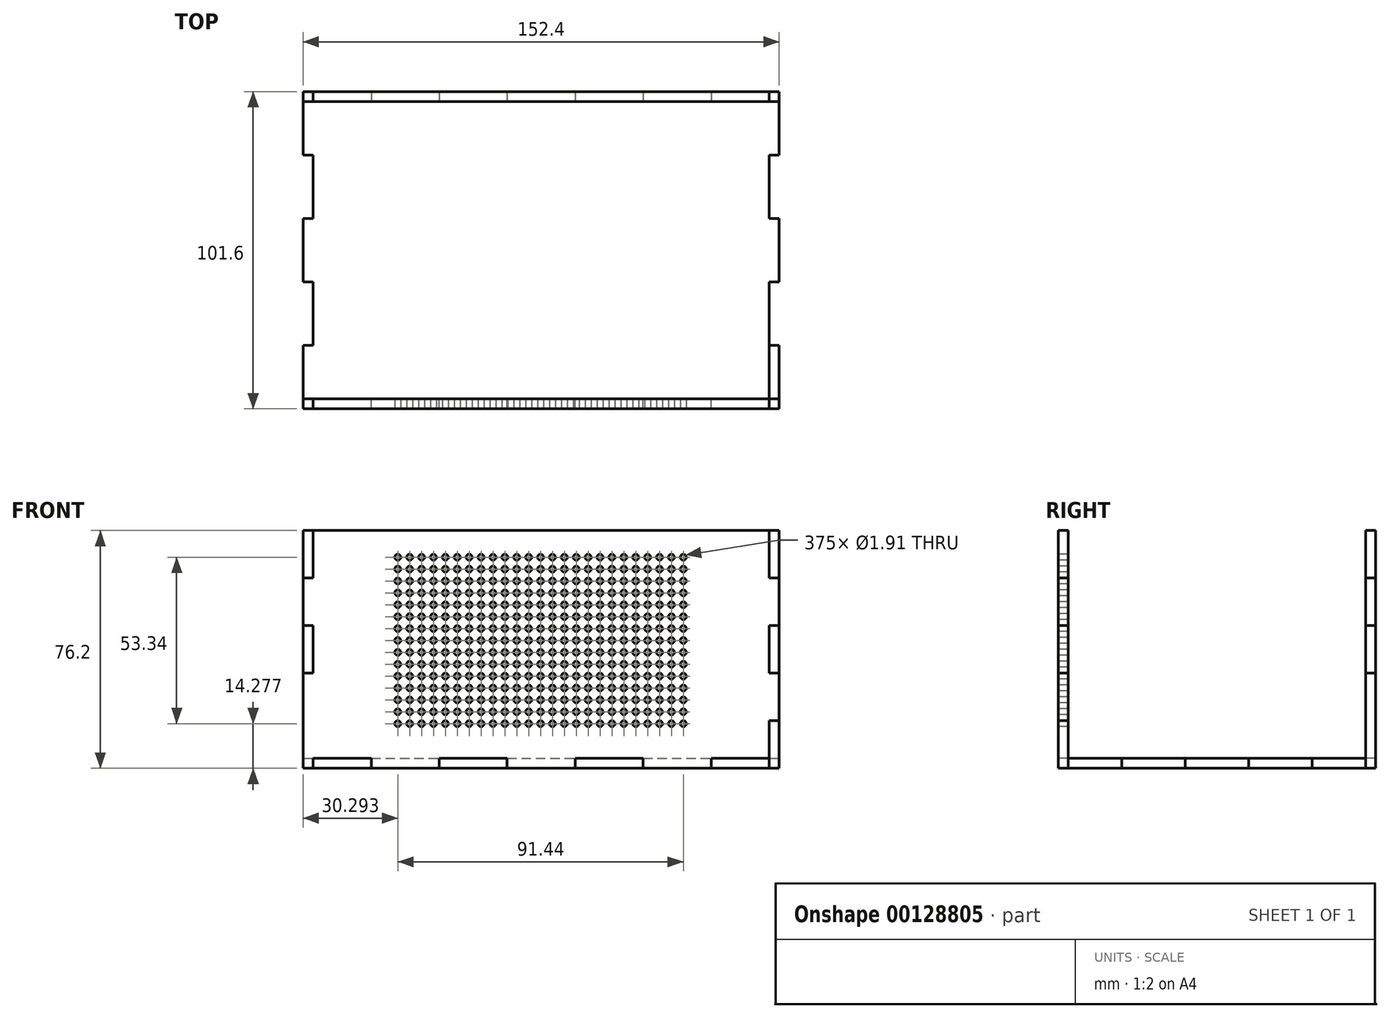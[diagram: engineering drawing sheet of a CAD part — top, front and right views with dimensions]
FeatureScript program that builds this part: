
annotation { "Feature Type Name" : "Feature", "Feature Type Description" : "" }
export const myFeature = defineFeature(function(context is Context, id is Id, definition is map)
    precondition{}
    {
        {
            var Q0;
            Q0=qCreatedBy(makeId("Top.planeOp"),FACE);
            var sketch = newSketch(context, id + "F0", { "sketchPlane" : qUnion([Q0])});
            skLineSegment(sketch, "E0.bottom", {"start": v(76.2, 50.8) * mm, "end": v(-76.2, 50.8) * mm});
            skLineSegment(sketch, "E0.top", {"start": v(76.2, -50.8) * mm, "end": v(-76.2, -50.8) * mm});
            skLineSegment(sketch, "E0.left", {"start": v(76.2, 50.8) * mm, "end": v(76.2, -50.8) * mm});
            skLineSegment(sketch, "E0.right", {"start": v(-76.2, 50.8) * mm, "end": v(-76.2, -50.8) * mm});
            skPoint(sketch, "E0.middle", {"position": v(0, 0) * mm});
            skLineSegment(sketch, "E1", {"start": v(-76.2, 50.8) * mm, "end": v(-76.2, 47.62) * mm});
            skLineSegment(sketch, "E2.1.0.0", {"start": v(-54.43, 50.8) * mm, "end": v(-54.43, 47.62) * mm});
            skLineSegment(sketch, "E2.2.0.0", {"start": v(-32.66, 50.8) * mm, "end": v(-32.66, 47.63) * mm});
            skLineSegment(sketch, "E2.3.0.0", {"start": v(-10.89, 50.8) * mm, "end": v(-10.89, 47.63) * mm});
            skLineSegment(sketch, "E2.4.0.0", {"start": v(10.89, 50.8) * mm, "end": v(10.89, 47.63) * mm});
            skLineSegment(sketch, "E2.5.0.0", {"start": v(32.66, 50.8) * mm, "end": v(32.66, 47.63) * mm});
            skLineSegment(sketch, "E2.6.0.0", {"start": v(54.43, 50.8) * mm, "end": v(54.43, 47.63) * mm});
            skLineSegment(sketch, "E2.7.0.0", {"start": v(76.2, 50.8) * mm, "end": v(76.2, 47.63) * mm});
            skLineSegment(sketch, "E2.direction1", {"start": v(-76.2, 47.63) * mm, "end": v(-54.43, 47.63) * mm, "construction": true});
            skLineSegment(sketch, "E3", {"start": v(-76.2, 47.63) * mm, "end": v(76.2, 47.63) * mm});
            skLineSegment(sketch, "E4.MirrorCS", {"start": v(-76.2, -50.8) * mm, "end": v(-76.2, -47.62) * mm});
            skLineSegment(sketch, "E5.MirrorCS", {"start": v(76.2, -50.8) * mm, "end": v(76.2, -47.63) * mm});
            skLineSegment(sketch, "E6.MirrorCS", {"start": v(54.43, -50.8) * mm, "end": v(54.43, -47.63) * mm});
            skLineSegment(sketch, "E7.MirrorCS", {"start": v(32.66, -50.8) * mm, "end": v(32.66, -47.63) * mm});
            skLineSegment(sketch, "E8.MirrorCS", {"start": v(10.89, -50.8) * mm, "end": v(10.89, -47.63) * mm});
            skLineSegment(sketch, "E9.MirrorCS", {"start": v(-54.43, -50.8) * mm, "end": v(-54.43, -47.62) * mm});
            skLineSegment(sketch, "E10.MirrorCS", {"start": v(-10.89, -50.8) * mm, "end": v(-10.89, -47.63) * mm});
            skLineSegment(sketch, "E11.MirrorCS", {"start": v(-32.66, -50.8) * mm, "end": v(-32.66, -47.63) * mm});
            skLineSegment(sketch, "E12.MirrorCS", {"start": v(-76.2, -47.63) * mm, "end": v(76.2, -47.63) * mm});
            skLineSegment(sketch, "E13.MirrorCS", {"start": v(-76.2, -47.63) * mm, "end": v(-54.43, -47.63) * mm, "construction": true});
            skLineSegment(sketch, "E14", {"start": v(-76.2, 50.8) * mm, "end": v(-73.03, 50.8) * mm});
            skLineSegment(sketch, "E15.0.1.0", {"start": v(-76.2, 30.48) * mm, "end": v(-73.03, 30.48) * mm});
            skLineSegment(sketch, "E15.0.2.0", {"start": v(-76.2, 10.16) * mm, "end": v(-73.03, 10.16) * mm});
            skLineSegment(sketch, "E15.0.3.0", {"start": v(-76.2, -10.16) * mm, "end": v(-73.03, -10.16) * mm});
            skLineSegment(sketch, "E15.0.4.0", {"start": v(-76.2, -30.48) * mm, "end": v(-73.03, -30.48) * mm});
            skLineSegment(sketch, "E15.0.5.0", {"start": v(-76.2, -50.8) * mm, "end": v(-73.03, -50.8) * mm});
            skLineSegment(sketch, "E15.direction1", {"start": v(-76.2, 50.8) * mm, "end": v(-59.4, 50.8) * mm, "construction": true});
            skLineSegment(sketch, "E15.direction2", {"start": v(-76.2, 50.8) * mm, "end": v(-76.2, 30.48) * mm, "construction": true});
            skLineSegment(sketch, "E16", {"start": v(-73.03, 50.8) * mm, "end": v(-73.03, -50.8) * mm});
            skLineSegment(sketch, "E17.MirrorCS", {"start": v(76.2, -50.8) * mm, "end": v(76.2, -47.62) * mm});
            skLineSegment(sketch, "E18.MirrorCS", {"start": v(76.2, 50.8) * mm, "end": v(76.2, 47.62) * mm});
            skLineSegment(sketch, "E19.MirrorCS", {"start": v(76.2, 50.8) * mm, "end": v(73.03, 50.8) * mm});
            skLineSegment(sketch, "E20.MirrorCS", {"start": v(76.2, -50.8) * mm, "end": v(73.03, -50.8) * mm});
            skLineSegment(sketch, "E21.MirrorCS", {"start": v(76.2, -10.16) * mm, "end": v(73.03, -10.16) * mm});
            skLineSegment(sketch, "E22.MirrorCS", {"start": v(76.2, 30.48) * mm, "end": v(73.03, 30.48) * mm});
            skLineSegment(sketch, "E23.MirrorCS", {"start": v(76.2, -30.48) * mm, "end": v(73.03, -30.48) * mm});
            skLineSegment(sketch, "E24.MirrorCS", {"start": v(76.2, 10.16) * mm, "end": v(73.03, 10.16) * mm});
            skLineSegment(sketch, "E25.MirrorCS", {"start": v(73.03, 50.8) * mm, "end": v(73.03, -50.8) * mm});
            skLineSegment(sketch, "E26.MirrorCS", {"start": v(76.2, 50.8) * mm, "end": v(76.2, 30.48) * mm, "construction": true});
            skSolve(sketch);
        }
        {
            var Q0;
            {var subQ3=sQuery(id+"F0.wireOp",EDGE,"E3");var subQ22=makeQuery(id+"F0.imprint","INTERSECT",VERTEX,{"derivedFrom":[sQuery(id+"F0.wireOp",EDGE,"E2.1.0.0"),subQ3]});Q0=makeQuery(id+"F0.imprint","IMPRINT",FACE,{"disambiguationData":[TD([[makeQuery(id+"F0.imprint","IMPRINT",EDGE,{"disambiguationData":[TD([[subQ22,1.0]])],"derivedFrom":subQ3}),-1.0]])]});}
            var Q1;
            {var subQ3=sQuery(id+"F0.wireOp",EDGE,"E2.1.0.0");Q1=makeQuery(id+"F0.imprint","IMPRINT",FACE,{"disambiguationData":[TD([[makeQuery(id+"F0.imprint","IMPRINT",EDGE,{"derivedFrom":subQ3}),-1.0]])]});}
            var Q2;
            {var subQ0=sQuery(id+"F0.wireOp",EDGE,"E1");Q2=makeQuery(id+"F0.imprint","IMPRINT",FACE,{"disambiguationData":[TD([[makeQuery(id+"F0.imprint","IMPRINT",EDGE,{"derivedFrom":subQ0}),1.0]])]});}
            var Q3;
            {var subQ3=sQuery(id+"F0.wireOp",EDGE,"E15.0.1.0");Q3=makeQuery(id+"F0.imprint","IMPRINT",FACE,{"disambiguationData":[TD([[makeQuery(id+"F0.imprint","IMPRINT",EDGE,{"derivedFrom":subQ3}),1.0]])]});}
            var Q4;
            {var subQ0=sQuery(id+"F0.wireOp",EDGE,"E15.0.2.0");Q4=makeQuery(id+"F0.imprint","IMPRINT",FACE,{"disambiguationData":[TD([[makeQuery(id+"F0.imprint","IMPRINT",EDGE,{"derivedFrom":subQ0}),-1.0]])]});}
            var Q5;
            {var subQ3=sQuery(id+"F0.wireOp",EDGE,"E15.0.4.0");Q5=makeQuery(id+"F0.imprint","IMPRINT",FACE,{"disambiguationData":[TD([[makeQuery(id+"F0.imprint","IMPRINT",EDGE,{"derivedFrom":subQ3}),-1.0]])]});}
            var Q6;
            {var subQ0=sQuery(id+"F0.wireOp",EDGE,"E4.MirrorCS");Q6=makeQuery(id+"F0.imprint","IMPRINT",FACE,{"disambiguationData":[TD([[makeQuery(id+"F0.imprint","IMPRINT",EDGE,{"derivedFrom":subQ0}),-1.0]])]});}
            var Q7;
            {var subQ0=sQuery(id+"F0.wireOp",EDGE,"E9.MirrorCS");Q7=makeQuery(id+"F0.imprint","IMPRINT",FACE,{"disambiguationData":[TD([[makeQuery(id+"F0.imprint","IMPRINT",EDGE,{"derivedFrom":subQ0}),1.0]])]});}
            var Q8;
            {var subQ0=sQuery(id+"F0.wireOp",EDGE,"E10.MirrorCS");Q8=makeQuery(id+"F0.imprint","IMPRINT",FACE,{"disambiguationData":[TD([[makeQuery(id+"F0.imprint","IMPRINT",EDGE,{"derivedFrom":subQ0}),1.0]])]});}
            var Q9;
            {var subQ0=sQuery(id+"F0.wireOp",EDGE,"E7.MirrorCS");Q9=makeQuery(id+"F0.imprint","IMPRINT",FACE,{"disambiguationData":[TD([[makeQuery(id+"F0.imprint","IMPRINT",EDGE,{"derivedFrom":subQ0}),1.0]])]});}
            var Q10;
            {var subQ0=sQuery(id+"F0.wireOp",EDGE,"E6.MirrorCS");Q10=makeQuery(id+"F0.imprint","IMPRINT",FACE,{"disambiguationData":[TD([[makeQuery(id+"F0.imprint","IMPRINT",EDGE,{"derivedFrom":subQ0}),-1.0]])]});}
            var Q11;
            {var subQ5=sQuery(id+"F0.wireOp",EDGE,"E20.MirrorCS");Q11=makeQuery(id+"F0.imprint","IMPRINT",FACE,{"disambiguationData":[TD([[makeQuery(id+"F0.imprint","IMPRINT",EDGE,{"derivedFrom":subQ5}),-1.0]])]});}
            var Q12;
            {var subQ5=sQuery(id+"F0.wireOp",EDGE,"E23.MirrorCS");Q12=makeQuery(id+"F0.imprint","IMPRINT",FACE,{"disambiguationData":[TD([[makeQuery(id+"F0.imprint","IMPRINT",EDGE,{"derivedFrom":subQ5}),1.0]])]});}
            var Q13;
            {var subQ0=sQuery(id+"F0.wireOp",EDGE,"E21.MirrorCS");Q13=makeQuery(id+"F0.imprint","IMPRINT",FACE,{"disambiguationData":[TD([[makeQuery(id+"F0.imprint","IMPRINT",EDGE,{"derivedFrom":subQ0}),-1.0]])]});}
            var Q14;
            {var subQ5=sQuery(id+"F0.wireOp",EDGE,"E22.MirrorCS");Q14=makeQuery(id+"F0.imprint","IMPRINT",FACE,{"disambiguationData":[TD([[makeQuery(id+"F0.imprint","IMPRINT",EDGE,{"derivedFrom":subQ5}),-1.0]])]});}
            var Q15;
            {var subQ5=sQuery(id+"F0.wireOp",EDGE,"E19.MirrorCS");Q15=makeQuery(id+"F0.imprint","IMPRINT",FACE,{"disambiguationData":[TD([[makeQuery(id+"F0.imprint","IMPRINT",EDGE,{"derivedFrom":subQ5}),1.0]])]});}
            var Q16;
            {var subQ3=sQuery(id+"F0.wireOp",EDGE,"E2.6.0.0");Q16=makeQuery(id+"F0.imprint","IMPRINT",FACE,{"disambiguationData":[TD([[makeQuery(id+"F0.imprint","IMPRINT",EDGE,{"derivedFrom":subQ3}),1.0]])]});}
            var Q17;
            {var subQ0=sQuery(id+"F0.wireOp",EDGE,"E2.4.0.0");Q17=makeQuery(id+"F0.imprint","IMPRINT",FACE,{"disambiguationData":[TD([[makeQuery(id+"F0.imprint","IMPRINT",EDGE,{"derivedFrom":subQ0}),1.0]])]});}
            var Q18;
            {var subQ0=sQuery(id+"F0.wireOp",EDGE,"E2.2.0.0");Q18=makeQuery(id+"F0.imprint","IMPRINT",FACE,{"disambiguationData":[TD([[makeQuery(id+"F0.imprint","IMPRINT",EDGE,{"derivedFrom":subQ0}),1.0]])]});}
            extrude(context, id + "F1", {"entities" : qUnion([Q0, Q1, Q2, Q3, Q4, Q5, Q6, Q7, Q8, Q9, Q10, Q11, Q12, Q13, Q14, Q15, Q16, Q17, Q18]), "depth" : 3.17 * mm});
        }
        {
            var Q0;
            {var subQ0=sQuery(id+"F0.wireOp",EDGE,"E0.left");var subQ1=makeQuery(id+"F0.imprint","INTERSECT",VERTEX,{"derivedFrom":[sQuery(id+"F0.wireOp",EDGE,"E12.MirrorCS"),subQ0]});Q0=makeQuery(id+"F1.opExtrude","SWEPT_FACE",FACE,{"disambiguationData":[OSD([subQ0]),TDD([makeQuery(id+"F0.imprint","IMPRINT",EDGE,{"disambiguationData":[TD([[subQ1,1.0]])],"derivedFrom":subQ0}),makeQuery(id+"F0.imprint","IMPRINT",EDGE,{"disambiguationData":[TD([[subQ1,-1.0]])],"derivedFrom":subQ0})])]});}
            var sketch = newSketch(context, id + "F2", { "sketchPlane" : qUnion([Q0])});
            skLineSegment(sketch, "E27.bottom", {"start": v(-50.8, 0) * mm, "end": v(50.8, 0) * mm});
            skLineSegment(sketch, "E27.top", {"start": v(-50.8, 76.2) * mm, "end": v(50.8, 76.2) * mm});
            skLineSegment(sketch, "E27.left", {"start": v(-50.8, 0) * mm, "end": v(-50.8, 76.2) * mm});
            skLineSegment(sketch, "E27.right", {"start": v(50.8, 0) * mm, "end": v(50.8, 76.2) * mm});
            skLineSegment(sketch, "E28", {"start": v(-50.8, 76.2) * mm, "end": v(-47.63, 76.2) * mm});
            skLineSegment(sketch, "E29.0.1.0", {"start": v(-50.8, 60.96) * mm, "end": v(-47.63, 60.96) * mm});
            skLineSegment(sketch, "E29.0.2.0", {"start": v(-50.8, 45.72) * mm, "end": v(-47.63, 45.72) * mm});
            skLineSegment(sketch, "E29.0.3.0", {"start": v(-50.8, 30.48) * mm, "end": v(-47.63, 30.48) * mm});
            skLineSegment(sketch, "E29.0.4.0", {"start": v(-50.8, 15.24) * mm, "end": v(-47.63, 15.24) * mm});
            skLineSegment(sketch, "E29.0.5.0", {"start": v(-50.8, 0) * mm, "end": v(-47.63, 0) * mm});
            skLineSegment(sketch, "E29.direction1", {"start": v(-50.8, 76.2) * mm, "end": v(-25.4, 76.2) * mm, "construction": true});
            skLineSegment(sketch, "E29.direction2", {"start": v(-50.8, 76.2) * mm, "end": v(-50.8, 60.96) * mm, "construction": true});
            skLineSegment(sketch, "E30", {"start": v(-47.63, 76.2) * mm, "end": v(-47.63, 0) * mm});
            skLineSegment(sketch, "E31.MirrorCS", {"start": v(50.8, 76.2) * mm, "end": v(47.63, 76.2) * mm});
            skLineSegment(sketch, "E32.MirrorCS", {"start": v(50.8, 0) * mm, "end": v(47.63, 0) * mm});
            skLineSegment(sketch, "E33.MirrorCS", {"start": v(50.8, 45.72) * mm, "end": v(47.63, 45.72) * mm});
            skLineSegment(sketch, "E34.MirrorCS", {"start": v(50.8, 60.96) * mm, "end": v(47.63, 60.96) * mm});
            skLineSegment(sketch, "E35.MirrorCS", {"start": v(50.8, 30.48) * mm, "end": v(47.63, 30.48) * mm});
            skLineSegment(sketch, "E36.MirrorCS", {"start": v(50.8, 15.24) * mm, "end": v(47.63, 15.24) * mm});
            skLineSegment(sketch, "E37.MirrorCS", {"start": v(50.8, 76.2) * mm, "end": v(50.8, 60.96) * mm, "construction": true});
            skLineSegment(sketch, "E38.MirrorCS", {"start": v(47.63, 76.2) * mm, "end": v(47.63, 0) * mm});
            skSolve(sketch);
        }
        {
            var Q0;
            {var subQ3=sQuery(id+"F2.wireOp",EDGE,"E27.top");Q0=makeQuery(id+"F2.imprint","IMPRINT",FACE,{"disambiguationData":[TD([[makeQuery(id+"F2.imprint","IMPRINT",EDGE,{"derivedFrom":subQ3}),-1.0]])]});}
            var Q1;
            {var subQ0=sQuery(id+"F2.wireOp",EDGE,"E28");Q1=makeQuery(id+"F2.imprint","IMPRINT",FACE,{"disambiguationData":[TD([[makeQuery(id+"F2.imprint","IMPRINT",EDGE,{"derivedFrom":subQ0}),-1.0]])]});}
            var Q2;
            {var subQ0=sQuery(id+"F2.wireOp",EDGE,"E29.0.2.0");Q2=makeQuery(id+"F2.imprint","IMPRINT",FACE,{"disambiguationData":[TD([[makeQuery(id+"F2.imprint","IMPRINT",EDGE,{"derivedFrom":subQ0}),-1.0]])]});}
            var Q3;
            {var subQ5=sQuery(id+"F2.wireOp",EDGE,"E29.0.4.0");Q3=makeQuery(id+"F2.imprint","IMPRINT",FACE,{"disambiguationData":[TD([[makeQuery(id+"F2.imprint","IMPRINT",EDGE,{"derivedFrom":subQ5}),-1.0]])]});}
            var Q4;
            {var subQ0=sQuery(id+"F2.wireOp",EDGE,"E32.MirrorCS");Q4=makeQuery(id+"F2.imprint","IMPRINT",FACE,{"disambiguationData":[TD([[makeQuery(id+"F2.imprint","IMPRINT",EDGE,{"derivedFrom":subQ0}),-1.0]])]});}
            var Q5;
            {var subQ0=sQuery(id+"F2.wireOp",EDGE,"E33.MirrorCS");Q5=makeQuery(id+"F2.imprint","IMPRINT",FACE,{"disambiguationData":[TD([[makeQuery(id+"F2.imprint","IMPRINT",EDGE,{"derivedFrom":subQ0}),1.0]])]});}
            var Q6;
            {var subQ0=sQuery(id+"F2.wireOp",EDGE,"E31.MirrorCS");Q6=makeQuery(id+"F2.imprint","IMPRINT",FACE,{"disambiguationData":[TD([[makeQuery(id+"F2.imprint","IMPRINT",EDGE,{"derivedFrom":subQ0}),1.0]])]});}
            var Q7;
            {var subQ1=sQuery(id+"F0.wireOp",EDGE,"E0.left");var subQ2=sQuery(id+"F0.wireOp",EDGE,"E23.MirrorCS");var subQ3=makeQuery(id+"F1.opExtrude","SWEPT_EDGE",EDGE,{"disambiguationData":[OSD([subQ2,subQ1])]});Q7=makeQuery(id+"F2.imprint","IMPRINT",FACE,{"disambiguationData":[TD([[makeQuery(id+"F2.imprint","IMPRINT",EDGE,{"derivedFrom":subQ3}),-1.0]])]});}
            var Q8;
            {var subQ0=sQuery(id+"F2.wireOp",EDGE,"E29.0.5.0");Q8=makeQuery(id+"F2.imprint","IMPRINT",FACE,{"disambiguationData":[TD([[makeQuery(id+"F2.imprint","IMPRINT",EDGE,{"derivedFrom":subQ0}),-1.0]])]});}
            extrude(context, id + "F3", {"entities" : qUnion([Q0, Q1, Q2, Q3, Q4, Q5, Q6, Q7, Q8]), "oppositeDirection" : true, "depth" : 3.17 * mm});
        }
        {
            var Q0;
            Q0=makeQuery(id+"F1.opExtrude","SWEPT_BODY",BODY,{"disambiguationData":[OSD([sQuery(id+"F0.wireOp",EDGE,"E0.bottom"),sQuery(id+"F0.wireOp",EDGE,"E0.right"),sQuery(id+"F0.wireOp",EDGE,"E1"),sQuery(id+"F0.wireOp",EDGE,"E2.1.0.0"),sQuery(id+"F0.wireOp",EDGE,"E2.2.0.0"),sQuery(id+"F0.wireOp",EDGE,"E2.3.0.0"),sQuery(id+"F0.wireOp",EDGE,"E2.4.0.0"),sQuery(id+"F0.wireOp",EDGE,"E2.5.0.0"),sQuery(id+"F0.wireOp",EDGE,"E2.6.0.0"),sQuery(id+"F0.wireOp",EDGE,"E3"),sQuery(id+"F0.wireOp",EDGE,"E4.MirrorCS"),sQuery(id+"F0.wireOp",EDGE,"E6.MirrorCS"),sQuery(id+"F0.wireOp",EDGE,"E7.MirrorCS"),sQuery(id+"F0.wireOp",EDGE,"E8.MirrorCS"),sQuery(id+"F0.wireOp",EDGE,"E9.MirrorCS"),sQuery(id+"F0.wireOp",EDGE,"E10.MirrorCS"),sQuery(id+"F0.wireOp",EDGE,"E11.MirrorCS"),sQuery(id+"F0.wireOp",EDGE,"E12.MirrorCS"),sQuery(id+"F0.wireOp",EDGE,"E0.top"),sQuery(id+"F0.wireOp",EDGE,"E14"),sQuery(id+"F0.wireOp",EDGE,"E15.0.1.0"),sQuery(id+"F0.wireOp",EDGE,"E15.0.2.0"),sQuery(id+"F0.wireOp",EDGE,"E15.0.3.0"),sQuery(id+"F0.wireOp",EDGE,"E15.0.4.0"),sQuery(id+"F0.wireOp",EDGE,"E15.0.5.0"),sQuery(id+"F0.wireOp",EDGE,"E16"),sQuery(id+"F0.wireOp",EDGE,"E19.MirrorCS"),sQuery(id+"F0.wireOp",EDGE,"E20.MirrorCS"),sQuery(id+"F0.wireOp",EDGE,"E21.MirrorCS"),sQuery(id+"F0.wireOp",EDGE,"E22.MirrorCS"),sQuery(id+"F0.wireOp",EDGE,"E23.MirrorCS"),sQuery(id+"F0.wireOp",EDGE,"E24.MirrorCS"),sQuery(id+"F0.wireOp",EDGE,"E25.MirrorCS"),sQuery(id+"F0.wireOp",EDGE,"E0.left")])]});
            var Q1;
            Q1=makeQuery(id+"F3.opExtrude","SWEPT_BODY",BODY,{"disambiguationData":[OSD([sQuery(id+"F2.wireOp",EDGE,"E27.bottom"),sQuery(id+"F2.wireOp",EDGE,"E27.top"),sQuery(id+"F2.wireOp",EDGE,"E27.left"),sQuery(id+"F2.wireOp",EDGE,"E28"),sQuery(id+"F2.wireOp",EDGE,"E29.0.1.0"),sQuery(id+"F2.wireOp",EDGE,"E29.0.2.0"),sQuery(id+"F2.wireOp",EDGE,"E29.0.3.0"),sQuery(id+"F2.wireOp",EDGE,"E29.0.4.0"),sQuery(id+"F2.wireOp",EDGE,"E29.0.5.0"),sQuery(id+"F2.wireOp",EDGE,"E30"),sQuery(id+"F2.wireOp",EDGE,"E31.MirrorCS"),sQuery(id+"F2.wireOp",EDGE,"E32.MirrorCS"),sQuery(id+"F2.wireOp",EDGE,"E33.MirrorCS"),sQuery(id+"F2.wireOp",EDGE,"E34.MirrorCS"),sQuery(id+"F2.wireOp",EDGE,"E35.MirrorCS"),sQuery(id+"F2.wireOp",EDGE,"E36.MirrorCS"),sQuery(id+"F2.wireOp",EDGE,"E38.MirrorCS"),sQuery(id+"F2.wireOp",EDGE,"E27.right")])]});
            booleanBodies(context, id + "F4", {"operationType" : BooleanOperationType.SUBTRACTION, "tools" : qUnion([Q0]), "targets" : qUnion([Q1]), "keepTools" : true});
        }
        {
            var Q0;
            Q0=makeQuery(id+"F3.opExtrude","SWEPT_BODY",BODY,{"disambiguationData":[OSD([sQuery(id+"F2.wireOp",EDGE,"E27.bottom"),sQuery(id+"F2.wireOp",EDGE,"E27.top"),sQuery(id+"F2.wireOp",EDGE,"E27.left"),sQuery(id+"F2.wireOp",EDGE,"E28"),sQuery(id+"F2.wireOp",EDGE,"E29.0.1.0"),sQuery(id+"F2.wireOp",EDGE,"E29.0.2.0"),sQuery(id+"F2.wireOp",EDGE,"E29.0.3.0"),sQuery(id+"F2.wireOp",EDGE,"E29.0.4.0"),sQuery(id+"F2.wireOp",EDGE,"E29.0.5.0"),sQuery(id+"F2.wireOp",EDGE,"E30"),sQuery(id+"F2.wireOp",EDGE,"E31.MirrorCS"),sQuery(id+"F2.wireOp",EDGE,"E32.MirrorCS"),sQuery(id+"F2.wireOp",EDGE,"E33.MirrorCS"),sQuery(id+"F2.wireOp",EDGE,"E34.MirrorCS"),sQuery(id+"F2.wireOp",EDGE,"E35.MirrorCS"),sQuery(id+"F2.wireOp",EDGE,"E36.MirrorCS"),sQuery(id+"F2.wireOp",EDGE,"E38.MirrorCS"),sQuery(id+"F2.wireOp",EDGE,"E27.right")])]});
            var Q1;
            Q1=qCreatedBy(makeId("Right.planeOp"),FACE);
            mirror(context, id + "F5", {"entities" : qUnion([Q0]), "mirrorPlane" : qUnion([Q1])});
        }
        {
            var Q0;
            Q0=makeQuery(id+"F1.opExtrude","SWEPT_FACE",FACE,{"disambiguationData":[OSD([sQuery(id+"F0.wireOp",EDGE,"E0.bottom"),sQuery(id+"F0.wireOp",EDGE,"E19.MirrorCS")])]});
            var sketch = newSketch(context, id + "F6", { "sketchPlane" : qUnion([Q0])});
            skLineSegment(sketch, "E39.bottom", {"start": v(-76.2, 0) * mm, "end": v(76.2, 0) * mm});
            skLineSegment(sketch, "E39.top", {"start": v(-76.2, 76.2) * mm, "end": v(76.2, 76.2) * mm});
            skLineSegment(sketch, "E39.left", {"start": v(-76.2, 0) * mm, "end": v(-76.2, 76.2) * mm});
            skLineSegment(sketch, "E39.right", {"start": v(76.2, 0) * mm, "end": v(76.2, 76.2) * mm});
            skSolve(sketch);
        }
        {
            var Q0;
            {var subQ4=sQuery(id+"F6.wireOp",EDGE,"E39.top");Q0=makeQuery(id+"F6.imprint","IMPRINT",FACE,{"disambiguationData":[TD([[makeQuery(id+"F6.imprint","IMPRINT",EDGE,{"derivedFrom":subQ4}),-1.0]])]});}
            extrude(context, id + "F7", {"entities" : qUnion([Q0]), "oppositeDirection" : true, "depth" : 3.17 * mm});
        }
        {
            var Q0;
            Q0=makeQuery(id+"F5.opPattern","COPY",BODY,{"derivedFrom":makeQuery(id+"F3.opExtrude","SWEPT_BODY",BODY,{"disambiguationData":[OSD([sQuery(id+"F2.wireOp",EDGE,"E27.bottom"),sQuery(id+"F2.wireOp",EDGE,"E27.top"),sQuery(id+"F2.wireOp",EDGE,"E27.left"),sQuery(id+"F2.wireOp",EDGE,"E28"),sQuery(id+"F2.wireOp",EDGE,"E29.0.1.0"),sQuery(id+"F2.wireOp",EDGE,"E29.0.2.0"),sQuery(id+"F2.wireOp",EDGE,"E29.0.3.0"),sQuery(id+"F2.wireOp",EDGE,"E29.0.4.0"),sQuery(id+"F2.wireOp",EDGE,"E29.0.5.0"),sQuery(id+"F2.wireOp",EDGE,"E30"),sQuery(id+"F2.wireOp",EDGE,"E31.MirrorCS"),sQuery(id+"F2.wireOp",EDGE,"E32.MirrorCS"),sQuery(id+"F2.wireOp",EDGE,"E33.MirrorCS"),sQuery(id+"F2.wireOp",EDGE,"E34.MirrorCS"),sQuery(id+"F2.wireOp",EDGE,"E35.MirrorCS"),sQuery(id+"F2.wireOp",EDGE,"E36.MirrorCS"),sQuery(id+"F2.wireOp",EDGE,"E38.MirrorCS"),sQuery(id+"F2.wireOp",EDGE,"E27.right")])]}),"instanceName":"1"});
            var Q1;
            Q1=makeQuery(id+"F1.opExtrude","SWEPT_BODY",BODY,{"disambiguationData":[OSD([sQuery(id+"F0.wireOp",EDGE,"E0.bottom"),sQuery(id+"F0.wireOp",EDGE,"E0.right"),sQuery(id+"F0.wireOp",EDGE,"E1"),sQuery(id+"F0.wireOp",EDGE,"E2.1.0.0"),sQuery(id+"F0.wireOp",EDGE,"E2.2.0.0"),sQuery(id+"F0.wireOp",EDGE,"E2.3.0.0"),sQuery(id+"F0.wireOp",EDGE,"E2.4.0.0"),sQuery(id+"F0.wireOp",EDGE,"E2.5.0.0"),sQuery(id+"F0.wireOp",EDGE,"E2.6.0.0"),sQuery(id+"F0.wireOp",EDGE,"E3"),sQuery(id+"F0.wireOp",EDGE,"E4.MirrorCS"),sQuery(id+"F0.wireOp",EDGE,"E6.MirrorCS"),sQuery(id+"F0.wireOp",EDGE,"E7.MirrorCS"),sQuery(id+"F0.wireOp",EDGE,"E8.MirrorCS"),sQuery(id+"F0.wireOp",EDGE,"E9.MirrorCS"),sQuery(id+"F0.wireOp",EDGE,"E10.MirrorCS"),sQuery(id+"F0.wireOp",EDGE,"E11.MirrorCS"),sQuery(id+"F0.wireOp",EDGE,"E12.MirrorCS"),sQuery(id+"F0.wireOp",EDGE,"E0.top"),sQuery(id+"F0.wireOp",EDGE,"E14"),sQuery(id+"F0.wireOp",EDGE,"E15.0.1.0"),sQuery(id+"F0.wireOp",EDGE,"E15.0.2.0"),sQuery(id+"F0.wireOp",EDGE,"E15.0.3.0"),sQuery(id+"F0.wireOp",EDGE,"E15.0.4.0"),sQuery(id+"F0.wireOp",EDGE,"E15.0.5.0"),sQuery(id+"F0.wireOp",EDGE,"E16"),sQuery(id+"F0.wireOp",EDGE,"E19.MirrorCS"),sQuery(id+"F0.wireOp",EDGE,"E20.MirrorCS"),sQuery(id+"F0.wireOp",EDGE,"E21.MirrorCS"),sQuery(id+"F0.wireOp",EDGE,"E22.MirrorCS"),sQuery(id+"F0.wireOp",EDGE,"E23.MirrorCS"),sQuery(id+"F0.wireOp",EDGE,"E24.MirrorCS"),sQuery(id+"F0.wireOp",EDGE,"E25.MirrorCS"),sQuery(id+"F0.wireOp",EDGE,"E0.left")])]});
            var Q2;
            Q2=makeQuery(id+"F3.opExtrude","SWEPT_BODY",BODY,{"disambiguationData":[OSD([sQuery(id+"F2.wireOp",EDGE,"E27.bottom"),sQuery(id+"F2.wireOp",EDGE,"E27.top"),sQuery(id+"F2.wireOp",EDGE,"E27.left"),sQuery(id+"F2.wireOp",EDGE,"E28"),sQuery(id+"F2.wireOp",EDGE,"E29.0.1.0"),sQuery(id+"F2.wireOp",EDGE,"E29.0.2.0"),sQuery(id+"F2.wireOp",EDGE,"E29.0.3.0"),sQuery(id+"F2.wireOp",EDGE,"E29.0.4.0"),sQuery(id+"F2.wireOp",EDGE,"E29.0.5.0"),sQuery(id+"F2.wireOp",EDGE,"E30"),sQuery(id+"F2.wireOp",EDGE,"E31.MirrorCS"),sQuery(id+"F2.wireOp",EDGE,"E32.MirrorCS"),sQuery(id+"F2.wireOp",EDGE,"E33.MirrorCS"),sQuery(id+"F2.wireOp",EDGE,"E34.MirrorCS"),sQuery(id+"F2.wireOp",EDGE,"E35.MirrorCS"),sQuery(id+"F2.wireOp",EDGE,"E36.MirrorCS"),sQuery(id+"F2.wireOp",EDGE,"E38.MirrorCS"),sQuery(id+"F2.wireOp",EDGE,"E27.right")])]});
            var Q3;
            Q3=makeQuery(id+"F7.opExtrude","SWEPT_BODY",BODY,{"disambiguationData":[OSD([sQuery(id+"F0.wireOp",EDGE,"E0.bottom"),sQuery(id+"F0.wireOp",EDGE,"E2.6.0.0"),sQuery(id+"F0.wireOp",EDGE,"E19.MirrorCS"),sQuery(id+"F6.wireOp",EDGE,"E39.bottom"),sQuery(id+"F6.wireOp",EDGE,"E39.top"),sQuery(id+"F6.wireOp",EDGE,"E39.left"),sQuery(id+"F6.wireOp",EDGE,"E39.right")])]});
            booleanBodies(context, id + "F8", {"operationType" : BooleanOperationType.SUBTRACTION, "tools" : qUnion([Q0, Q1, Q2]), "targets" : qUnion([Q3]), "keepTools" : true});
        }
        {
            var Q0;
            Q0=makeQuery(id+"F7.opExtrude","SWEPT_BODY",BODY,{"disambiguationData":[OSD([sQuery(id+"F0.wireOp",EDGE,"E0.bottom"),sQuery(id+"F0.wireOp",EDGE,"E2.6.0.0"),sQuery(id+"F0.wireOp",EDGE,"E19.MirrorCS"),sQuery(id+"F6.wireOp",EDGE,"E39.bottom"),sQuery(id+"F6.wireOp",EDGE,"E39.top"),sQuery(id+"F6.wireOp",EDGE,"E39.left"),sQuery(id+"F6.wireOp",EDGE,"E39.right")])]});
            var Q1;
            Q1=qCreatedBy(makeId("Front.planeOp"),FACE);
            mirror(context, id + "F9", {"entities" : qUnion([Q0]), "mirrorPlane" : qUnion([Q1])});
        }
        {
            var Q0;
            Q0=makeQuery(id+"F9.opPattern","COPY",FACE,{"derivedFrom":makeQuery(id+"F7.opExtrude","CAP_FACE",FACE,{"disambiguationData":[OSD([sQuery(id+"F0.wireOp",EDGE,"E0.bottom"),sQuery(id+"F0.wireOp",EDGE,"E2.6.0.0"),sQuery(id+"F0.wireOp",EDGE,"E19.MirrorCS"),sQuery(id+"F6.wireOp",EDGE,"E39.bottom"),sQuery(id+"F6.wireOp",EDGE,"E39.top"),sQuery(id+"F6.wireOp",EDGE,"E39.left"),sQuery(id+"F6.wireOp",EDGE,"E39.right")])],"isStart":true}),"instanceName":"1"});
            var sketch = newSketch(context, id + "F10", { "sketchPlane" : qUnion([Q0])});
            skCircle(sketch, "E40", {"center": v(-45.9, 67.62) * mm, "radius": 0.95 * mm});
            skCircle(sketch, "E41.0.1.0", {"center": v(-45.9, 63.8) * mm, "radius": 0.95 * mm});
            skCircle(sketch, "E41.0.2.0", {"center": v(-45.9, 60) * mm, "radius": 0.95 * mm});
            skCircle(sketch, "E41.0.3.0", {"center": v(-45.9, 56.19) * mm, "radius": 0.95 * mm});
            skCircle(sketch, "E41.0.4.0", {"center": v(-45.9, 52.38) * mm, "radius": 0.95 * mm});
            skCircle(sketch, "E41.0.5.0", {"center": v(-45.9, 48.57) * mm, "radius": 0.95 * mm});
            skCircle(sketch, "E41.0.6.0", {"center": v(-45.9, 44.76) * mm, "radius": 0.95 * mm});
            skCircle(sketch, "E41.0.7.0", {"center": v(-45.9, 40.95) * mm, "radius": 0.95 * mm});
            skCircle(sketch, "E41.0.8.0", {"center": v(-45.9, 37.14) * mm, "radius": 0.95 * mm});
            skCircle(sketch, "E41.0.9.0", {"center": v(-45.9, 33.33) * mm, "radius": 0.95 * mm});
            skCircle(sketch, "E41.0.10.0", {"center": v(-45.9, 29.52) * mm, "radius": 0.95 * mm});
            skCircle(sketch, "E41.0.11.0", {"center": v(-45.9, 25.7) * mm, "radius": 0.95 * mm});
            skCircle(sketch, "E41.0.12.0", {"center": v(-45.9, 21.9) * mm, "radius": 0.95 * mm});
            skCircle(sketch, "E41.0.13.0", {"center": v(-45.9, 18.09) * mm, "radius": 0.95 * mm});
            skCircle(sketch, "E41.0.14.0", {"center": v(-45.9, 14.28) * mm, "radius": 0.95 * mm});
            skCircle(sketch, "E41.1.0.0", {"center": v(-42.1, 67.62) * mm, "radius": 0.95 * mm});
            skCircle(sketch, "E41.1.1.0", {"center": v(-42.1, 63.8) * mm, "radius": 0.95 * mm});
            skCircle(sketch, "E41.1.2.0", {"center": v(-42.1, 60) * mm, "radius": 0.95 * mm});
            skCircle(sketch, "E41.1.3.0", {"center": v(-42.1, 56.19) * mm, "radius": 0.95 * mm});
            skCircle(sketch, "E41.1.4.0", {"center": v(-42.1, 52.38) * mm, "radius": 0.95 * mm});
            skCircle(sketch, "E41.1.5.0", {"center": v(-42.1, 48.57) * mm, "radius": 0.95 * mm});
            skCircle(sketch, "E41.1.6.0", {"center": v(-42.1, 44.76) * mm, "radius": 0.95 * mm});
            skCircle(sketch, "E41.1.7.0", {"center": v(-42.1, 40.95) * mm, "radius": 0.95 * mm});
            skCircle(sketch, "E41.1.8.0", {"center": v(-42.1, 37.14) * mm, "radius": 0.95 * mm});
            skCircle(sketch, "E41.1.9.0", {"center": v(-42.1, 33.33) * mm, "radius": 0.95 * mm});
            skCircle(sketch, "E41.1.10.0", {"center": v(-42.1, 29.52) * mm, "radius": 0.95 * mm});
            skCircle(sketch, "E41.1.11.0", {"center": v(-42.1, 25.7) * mm, "radius": 0.95 * mm});
            skCircle(sketch, "E41.1.12.0", {"center": v(-42.1, 21.9) * mm, "radius": 0.95 * mm});
            skCircle(sketch, "E41.1.13.0", {"center": v(-42.1, 18.09) * mm, "radius": 0.95 * mm});
            skCircle(sketch, "E41.1.14.0", {"center": v(-42.1, 14.28) * mm, "radius": 0.95 * mm});
            skCircle(sketch, "E41.2.0.0", {"center": v(-38.29, 67.62) * mm, "radius": 0.95 * mm});
            skCircle(sketch, "E41.2.1.0", {"center": v(-38.29, 63.8) * mm, "radius": 0.95 * mm});
            skCircle(sketch, "E41.2.2.0", {"center": v(-38.29, 60) * mm, "radius": 0.95 * mm});
            skCircle(sketch, "E41.2.3.0", {"center": v(-38.29, 56.19) * mm, "radius": 0.95 * mm});
            skCircle(sketch, "E41.2.4.0", {"center": v(-38.29, 52.38) * mm, "radius": 0.95 * mm});
            skCircle(sketch, "E41.2.5.0", {"center": v(-38.29, 48.57) * mm, "radius": 0.95 * mm});
            skCircle(sketch, "E41.2.6.0", {"center": v(-38.29, 44.76) * mm, "radius": 0.95 * mm});
            skCircle(sketch, "E41.2.7.0", {"center": v(-38.29, 40.95) * mm, "radius": 0.95 * mm});
            skCircle(sketch, "E41.2.8.0", {"center": v(-38.29, 37.14) * mm, "radius": 0.95 * mm});
            skCircle(sketch, "E41.2.9.0", {"center": v(-38.29, 33.33) * mm, "radius": 0.95 * mm});
            skCircle(sketch, "E41.2.10.0", {"center": v(-38.29, 29.52) * mm, "radius": 0.95 * mm});
            skCircle(sketch, "E41.2.11.0", {"center": v(-38.29, 25.7) * mm, "radius": 0.95 * mm});
            skCircle(sketch, "E41.2.12.0", {"center": v(-38.29, 21.9) * mm, "radius": 0.95 * mm});
            skCircle(sketch, "E41.2.13.0", {"center": v(-38.29, 18.09) * mm, "radius": 0.95 * mm});
            skCircle(sketch, "E41.2.14.0", {"center": v(-38.29, 14.28) * mm, "radius": 0.95 * mm});
            skCircle(sketch, "E41.3.0.0", {"center": v(-34.48, 67.62) * mm, "radius": 0.95 * mm});
            skCircle(sketch, "E41.3.1.0", {"center": v(-34.48, 63.8) * mm, "radius": 0.95 * mm});
            skCircle(sketch, "E41.3.2.0", {"center": v(-34.48, 60) * mm, "radius": 0.95 * mm});
            skCircle(sketch, "E41.3.3.0", {"center": v(-34.48, 56.19) * mm, "radius": 0.95 * mm});
            skCircle(sketch, "E41.3.4.0", {"center": v(-34.48, 52.38) * mm, "radius": 0.95 * mm});
            skCircle(sketch, "E41.3.5.0", {"center": v(-34.48, 48.57) * mm, "radius": 0.95 * mm});
            skCircle(sketch, "E41.3.6.0", {"center": v(-34.48, 44.76) * mm, "radius": 0.95 * mm});
            skCircle(sketch, "E41.3.7.0", {"center": v(-34.48, 40.95) * mm, "radius": 0.95 * mm});
            skCircle(sketch, "E41.3.8.0", {"center": v(-34.48, 37.14) * mm, "radius": 0.95 * mm});
            skCircle(sketch, "E41.3.9.0", {"center": v(-34.48, 33.33) * mm, "radius": 0.95 * mm});
            skCircle(sketch, "E41.3.10.0", {"center": v(-34.48, 29.52) * mm, "radius": 0.95 * mm});
            skCircle(sketch, "E41.3.11.0", {"center": v(-34.48, 25.7) * mm, "radius": 0.95 * mm});
            skCircle(sketch, "E41.3.12.0", {"center": v(-34.48, 21.9) * mm, "radius": 0.95 * mm});
            skCircle(sketch, "E41.3.13.0", {"center": v(-34.48, 18.09) * mm, "radius": 0.95 * mm});
            skCircle(sketch, "E41.3.14.0", {"center": v(-34.48, 14.28) * mm, "radius": 0.95 * mm});
            skCircle(sketch, "E41.4.0.0", {"center": v(-30.67, 67.62) * mm, "radius": 0.95 * mm});
            skCircle(sketch, "E41.4.1.0", {"center": v(-30.67, 63.8) * mm, "radius": 0.95 * mm});
            skCircle(sketch, "E41.4.2.0", {"center": v(-30.67, 60) * mm, "radius": 0.95 * mm});
            skCircle(sketch, "E41.4.3.0", {"center": v(-30.67, 56.19) * mm, "radius": 0.95 * mm});
            skCircle(sketch, "E41.4.4.0", {"center": v(-30.67, 52.38) * mm, "radius": 0.95 * mm});
            skCircle(sketch, "E41.4.5.0", {"center": v(-30.67, 48.57) * mm, "radius": 0.95 * mm});
            skCircle(sketch, "E41.4.6.0", {"center": v(-30.67, 44.76) * mm, "radius": 0.95 * mm});
            skCircle(sketch, "E41.4.7.0", {"center": v(-30.67, 40.95) * mm, "radius": 0.95 * mm});
            skCircle(sketch, "E41.4.8.0", {"center": v(-30.67, 37.14) * mm, "radius": 0.95 * mm});
            skCircle(sketch, "E41.4.9.0", {"center": v(-30.67, 33.33) * mm, "radius": 0.95 * mm});
            skCircle(sketch, "E41.4.10.0", {"center": v(-30.67, 29.52) * mm, "radius": 0.95 * mm});
            skCircle(sketch, "E41.4.11.0", {"center": v(-30.67, 25.7) * mm, "radius": 0.95 * mm});
            skCircle(sketch, "E41.4.12.0", {"center": v(-30.67, 21.9) * mm, "radius": 0.95 * mm});
            skCircle(sketch, "E41.4.13.0", {"center": v(-30.67, 18.09) * mm, "radius": 0.95 * mm});
            skCircle(sketch, "E41.4.14.0", {"center": v(-30.67, 14.28) * mm, "radius": 0.95 * mm});
            skCircle(sketch, "E41.5.0.0", {"center": v(-26.86, 67.62) * mm, "radius": 0.95 * mm});
            skCircle(sketch, "E41.5.1.0", {"center": v(-26.86, 63.8) * mm, "radius": 0.95 * mm});
            skCircle(sketch, "E41.5.2.0", {"center": v(-26.86, 60) * mm, "radius": 0.95 * mm});
            skCircle(sketch, "E41.5.3.0", {"center": v(-26.86, 56.19) * mm, "radius": 0.95 * mm});
            skCircle(sketch, "E41.5.4.0", {"center": v(-26.86, 52.38) * mm, "radius": 0.95 * mm});
            skCircle(sketch, "E41.5.5.0", {"center": v(-26.86, 48.57) * mm, "radius": 0.95 * mm});
            skCircle(sketch, "E41.5.6.0", {"center": v(-26.86, 44.76) * mm, "radius": 0.95 * mm});
            skCircle(sketch, "E41.5.7.0", {"center": v(-26.86, 40.95) * mm, "radius": 0.95 * mm});
            skCircle(sketch, "E41.5.8.0", {"center": v(-26.86, 37.14) * mm, "radius": 0.95 * mm});
            skCircle(sketch, "E41.5.9.0", {"center": v(-26.86, 33.33) * mm, "radius": 0.95 * mm});
            skCircle(sketch, "E41.5.10.0", {"center": v(-26.86, 29.52) * mm, "radius": 0.95 * mm});
            skCircle(sketch, "E41.5.11.0", {"center": v(-26.86, 25.7) * mm, "radius": 0.95 * mm});
            skCircle(sketch, "E41.5.12.0", {"center": v(-26.86, 21.9) * mm, "radius": 0.95 * mm});
            skCircle(sketch, "E41.5.13.0", {"center": v(-26.86, 18.09) * mm, "radius": 0.95 * mm});
            skCircle(sketch, "E41.5.14.0", {"center": v(-26.86, 14.28) * mm, "radius": 0.95 * mm});
            skCircle(sketch, "E41.6.0.0", {"center": v(-23.05, 67.62) * mm, "radius": 0.95 * mm});
            skCircle(sketch, "E41.6.1.0", {"center": v(-23.05, 63.8) * mm, "radius": 0.95 * mm});
            skCircle(sketch, "E41.6.2.0", {"center": v(-23.05, 60) * mm, "radius": 0.95 * mm});
            skCircle(sketch, "E41.6.3.0", {"center": v(-23.05, 56.19) * mm, "radius": 0.95 * mm});
            skCircle(sketch, "E41.6.4.0", {"center": v(-23.05, 52.38) * mm, "radius": 0.95 * mm});
            skCircle(sketch, "E41.6.5.0", {"center": v(-23.05, 48.57) * mm, "radius": 0.95 * mm});
            skCircle(sketch, "E41.6.6.0", {"center": v(-23.05, 44.76) * mm, "radius": 0.95 * mm});
            skCircle(sketch, "E41.6.7.0", {"center": v(-23.05, 40.95) * mm, "radius": 0.95 * mm});
            skCircle(sketch, "E41.6.8.0", {"center": v(-23.05, 37.14) * mm, "radius": 0.95 * mm});
            skCircle(sketch, "E41.6.9.0", {"center": v(-23.05, 33.33) * mm, "radius": 0.95 * mm});
            skCircle(sketch, "E41.6.10.0", {"center": v(-23.05, 29.52) * mm, "radius": 0.95 * mm});
            skCircle(sketch, "E41.6.11.0", {"center": v(-23.05, 25.7) * mm, "radius": 0.95 * mm});
            skCircle(sketch, "E41.6.12.0", {"center": v(-23.05, 21.9) * mm, "radius": 0.95 * mm});
            skCircle(sketch, "E41.6.13.0", {"center": v(-23.05, 18.09) * mm, "radius": 0.95 * mm});
            skCircle(sketch, "E41.6.14.0", {"center": v(-23.05, 14.28) * mm, "radius": 0.95 * mm});
            skCircle(sketch, "E41.7.0.0", {"center": v(-19.24, 67.62) * mm, "radius": 0.95 * mm});
            skCircle(sketch, "E41.7.1.0", {"center": v(-19.24, 63.8) * mm, "radius": 0.95 * mm});
            skCircle(sketch, "E41.7.2.0", {"center": v(-19.24, 60) * mm, "radius": 0.95 * mm});
            skCircle(sketch, "E41.7.3.0", {"center": v(-19.24, 56.19) * mm, "radius": 0.95 * mm});
            skCircle(sketch, "E41.7.4.0", {"center": v(-19.24, 52.38) * mm, "radius": 0.95 * mm});
            skCircle(sketch, "E41.7.5.0", {"center": v(-19.24, 48.57) * mm, "radius": 0.95 * mm});
            skCircle(sketch, "E41.7.6.0", {"center": v(-19.24, 44.76) * mm, "radius": 0.95 * mm});
            skCircle(sketch, "E41.7.7.0", {"center": v(-19.24, 40.95) * mm, "radius": 0.95 * mm});
            skCircle(sketch, "E41.7.8.0", {"center": v(-19.24, 37.14) * mm, "radius": 0.95 * mm});
            skCircle(sketch, "E41.7.9.0", {"center": v(-19.24, 33.33) * mm, "radius": 0.95 * mm});
            skCircle(sketch, "E41.7.10.0", {"center": v(-19.24, 29.52) * mm, "radius": 0.95 * mm});
            skCircle(sketch, "E41.7.11.0", {"center": v(-19.24, 25.7) * mm, "radius": 0.95 * mm});
            skCircle(sketch, "E41.7.12.0", {"center": v(-19.24, 21.9) * mm, "radius": 0.95 * mm});
            skCircle(sketch, "E41.7.13.0", {"center": v(-19.24, 18.09) * mm, "radius": 0.95 * mm});
            skCircle(sketch, "E41.7.14.0", {"center": v(-19.24, 14.28) * mm, "radius": 0.95 * mm});
            skCircle(sketch, "E41.8.0.0", {"center": v(-15.43, 67.62) * mm, "radius": 0.95 * mm});
            skCircle(sketch, "E41.8.1.0", {"center": v(-15.43, 63.8) * mm, "radius": 0.95 * mm});
            skCircle(sketch, "E41.8.2.0", {"center": v(-15.43, 60) * mm, "radius": 0.95 * mm});
            skCircle(sketch, "E41.8.3.0", {"center": v(-15.43, 56.19) * mm, "radius": 0.95 * mm});
            skCircle(sketch, "E41.8.4.0", {"center": v(-15.43, 52.38) * mm, "radius": 0.95 * mm});
            skCircle(sketch, "E41.8.5.0", {"center": v(-15.43, 48.57) * mm, "radius": 0.95 * mm});
            skCircle(sketch, "E41.8.6.0", {"center": v(-15.43, 44.76) * mm, "radius": 0.95 * mm});
            skCircle(sketch, "E41.8.7.0", {"center": v(-15.43, 40.95) * mm, "radius": 0.95 * mm});
            skCircle(sketch, "E41.8.8.0", {"center": v(-15.43, 37.14) * mm, "radius": 0.95 * mm});
            skCircle(sketch, "E41.8.9.0", {"center": v(-15.43, 33.33) * mm, "radius": 0.95 * mm});
            skCircle(sketch, "E41.8.10.0", {"center": v(-15.43, 29.52) * mm, "radius": 0.95 * mm});
            skCircle(sketch, "E41.8.11.0", {"center": v(-15.43, 25.7) * mm, "radius": 0.95 * mm});
            skCircle(sketch, "E41.8.12.0", {"center": v(-15.43, 21.9) * mm, "radius": 0.95 * mm});
            skCircle(sketch, "E41.8.13.0", {"center": v(-15.43, 18.09) * mm, "radius": 0.95 * mm});
            skCircle(sketch, "E41.8.14.0", {"center": v(-15.43, 14.28) * mm, "radius": 0.95 * mm});
            skCircle(sketch, "E41.9.0.0", {"center": v(-11.62, 67.62) * mm, "radius": 0.95 * mm});
            skCircle(sketch, "E41.9.1.0", {"center": v(-11.62, 63.8) * mm, "radius": 0.95 * mm});
            skCircle(sketch, "E41.9.2.0", {"center": v(-11.62, 60) * mm, "radius": 0.95 * mm});
            skCircle(sketch, "E41.9.3.0", {"center": v(-11.62, 56.19) * mm, "radius": 0.95 * mm});
            skCircle(sketch, "E41.9.4.0", {"center": v(-11.62, 52.38) * mm, "radius": 0.95 * mm});
            skCircle(sketch, "E41.9.5.0", {"center": v(-11.62, 48.57) * mm, "radius": 0.95 * mm});
            skCircle(sketch, "E41.9.6.0", {"center": v(-11.62, 44.76) * mm, "radius": 0.95 * mm});
            skCircle(sketch, "E41.9.7.0", {"center": v(-11.62, 40.95) * mm, "radius": 0.95 * mm});
            skCircle(sketch, "E41.9.8.0", {"center": v(-11.62, 37.14) * mm, "radius": 0.95 * mm});
            skCircle(sketch, "E41.9.9.0", {"center": v(-11.62, 33.33) * mm, "radius": 0.95 * mm});
            skCircle(sketch, "E41.9.10.0", {"center": v(-11.62, 29.52) * mm, "radius": 0.95 * mm});
            skCircle(sketch, "E41.9.11.0", {"center": v(-11.62, 25.7) * mm, "radius": 0.95 * mm});
            skCircle(sketch, "E41.9.12.0", {"center": v(-11.62, 21.9) * mm, "radius": 0.95 * mm});
            skCircle(sketch, "E41.9.13.0", {"center": v(-11.62, 18.09) * mm, "radius": 0.95 * mm});
            skCircle(sketch, "E41.9.14.0", {"center": v(-11.62, 14.28) * mm, "radius": 0.95 * mm});
            skCircle(sketch, "E41.10.0.0", {"center": v(-7.8, 67.62) * mm, "radius": 0.95 * mm});
            skCircle(sketch, "E41.10.1.0", {"center": v(-7.8, 63.8) * mm, "radius": 0.95 * mm});
            skCircle(sketch, "E41.10.2.0", {"center": v(-7.8, 60) * mm, "radius": 0.95 * mm});
            skCircle(sketch, "E41.10.3.0", {"center": v(-7.8, 56.19) * mm, "radius": 0.95 * mm});
            skCircle(sketch, "E41.10.4.0", {"center": v(-7.8, 52.38) * mm, "radius": 0.95 * mm});
            skCircle(sketch, "E41.10.5.0", {"center": v(-7.8, 48.57) * mm, "radius": 0.95 * mm});
            skCircle(sketch, "E41.10.6.0", {"center": v(-7.8, 44.76) * mm, "radius": 0.95 * mm});
            skCircle(sketch, "E41.10.7.0", {"center": v(-7.8, 40.95) * mm, "radius": 0.95 * mm});
            skCircle(sketch, "E41.10.8.0", {"center": v(-7.8, 37.14) * mm, "radius": 0.95 * mm});
            skCircle(sketch, "E41.10.9.0", {"center": v(-7.8, 33.33) * mm, "radius": 0.95 * mm});
            skCircle(sketch, "E41.10.10.0", {"center": v(-7.8, 29.52) * mm, "radius": 0.95 * mm});
            skCircle(sketch, "E41.10.11.0", {"center": v(-7.8, 25.7) * mm, "radius": 0.95 * mm});
            skCircle(sketch, "E41.10.12.0", {"center": v(-7.8, 21.9) * mm, "radius": 0.95 * mm});
            skCircle(sketch, "E41.10.13.0", {"center": v(-7.8, 18.09) * mm, "radius": 0.95 * mm});
            skCircle(sketch, "E41.10.14.0", {"center": v(-7.8, 14.28) * mm, "radius": 0.95 * mm});
            skCircle(sketch, "E41.11.0.0", {"center": v(-4, 67.62) * mm, "radius": 0.95 * mm});
            skCircle(sketch, "E41.11.1.0", {"center": v(-4, 63.8) * mm, "radius": 0.95 * mm});
            skCircle(sketch, "E41.11.2.0", {"center": v(-4, 60) * mm, "radius": 0.95 * mm});
            skCircle(sketch, "E41.11.3.0", {"center": v(-4, 56.19) * mm, "radius": 0.95 * mm});
            skCircle(sketch, "E41.11.4.0", {"center": v(-4, 52.38) * mm, "radius": 0.95 * mm});
            skCircle(sketch, "E41.11.5.0", {"center": v(-4, 48.57) * mm, "radius": 0.95 * mm});
            skCircle(sketch, "E41.11.6.0", {"center": v(-4, 44.76) * mm, "radius": 0.95 * mm});
            skCircle(sketch, "E41.11.7.0", {"center": v(-4, 40.95) * mm, "radius": 0.95 * mm});
            skCircle(sketch, "E41.11.8.0", {"center": v(-4, 37.14) * mm, "radius": 0.95 * mm});
            skCircle(sketch, "E41.11.9.0", {"center": v(-4, 33.33) * mm, "radius": 0.95 * mm});
            skCircle(sketch, "E41.11.10.0", {"center": v(-4, 29.52) * mm, "radius": 0.95 * mm});
            skCircle(sketch, "E41.11.11.0", {"center": v(-4, 25.7) * mm, "radius": 0.95 * mm});
            skCircle(sketch, "E41.11.12.0", {"center": v(-4, 21.9) * mm, "radius": 0.95 * mm});
            skCircle(sketch, "E41.11.13.0", {"center": v(-4, 18.09) * mm, "radius": 0.95 * mm});
            skCircle(sketch, "E41.11.14.0", {"center": v(-4, 14.28) * mm, "radius": 0.95 * mm});
            skCircle(sketch, "E41.12.0.0", {"center": v(-0.19, 67.62) * mm, "radius": 0.95 * mm});
            skCircle(sketch, "E41.12.1.0", {"center": v(-0.19, 63.8) * mm, "radius": 0.95 * mm});
            skCircle(sketch, "E41.12.2.0", {"center": v(-0.19, 60) * mm, "radius": 0.95 * mm});
            skCircle(sketch, "E41.12.3.0", {"center": v(-0.19, 56.19) * mm, "radius": 0.95 * mm});
            skCircle(sketch, "E41.12.4.0", {"center": v(-0.19, 52.38) * mm, "radius": 0.95 * mm});
            skCircle(sketch, "E41.12.5.0", {"center": v(-0.19, 48.57) * mm, "radius": 0.95 * mm});
            skCircle(sketch, "E41.12.6.0", {"center": v(-0.19, 44.76) * mm, "radius": 0.95 * mm});
            skCircle(sketch, "E41.12.7.0", {"center": v(-0.19, 40.95) * mm, "radius": 0.95 * mm});
            skCircle(sketch, "E41.12.8.0", {"center": v(-0.19, 37.14) * mm, "radius": 0.95 * mm});
            skCircle(sketch, "E41.12.9.0", {"center": v(-0.19, 33.33) * mm, "radius": 0.95 * mm});
            skCircle(sketch, "E41.12.10.0", {"center": v(-0.19, 29.52) * mm, "radius": 0.95 * mm});
            skCircle(sketch, "E41.12.11.0", {"center": v(-0.19, 25.7) * mm, "radius": 0.95 * mm});
            skCircle(sketch, "E41.12.12.0", {"center": v(-0.19, 21.9) * mm, "radius": 0.95 * mm});
            skCircle(sketch, "E41.12.13.0", {"center": v(-0.19, 18.09) * mm, "radius": 0.95 * mm});
            skCircle(sketch, "E41.12.14.0", {"center": v(-0.19, 14.28) * mm, "radius": 0.95 * mm});
            skCircle(sketch, "E41.13.0.0", {"center": v(3.62, 67.62) * mm, "radius": 0.95 * mm});
            skCircle(sketch, "E41.13.1.0", {"center": v(3.62, 63.8) * mm, "radius": 0.95 * mm});
            skCircle(sketch, "E41.13.2.0", {"center": v(3.62, 60) * mm, "radius": 0.95 * mm});
            skCircle(sketch, "E41.13.3.0", {"center": v(3.62, 56.19) * mm, "radius": 0.95 * mm});
            skCircle(sketch, "E41.13.4.0", {"center": v(3.62, 52.38) * mm, "radius": 0.95 * mm});
            skCircle(sketch, "E41.13.5.0", {"center": v(3.62, 48.57) * mm, "radius": 0.95 * mm});
            skCircle(sketch, "E41.13.6.0", {"center": v(3.62, 44.76) * mm, "radius": 0.95 * mm});
            skCircle(sketch, "E41.13.7.0", {"center": v(3.62, 40.95) * mm, "radius": 0.95 * mm});
            skCircle(sketch, "E41.13.8.0", {"center": v(3.62, 37.14) * mm, "radius": 0.95 * mm});
            skCircle(sketch, "E41.13.9.0", {"center": v(3.62, 33.33) * mm, "radius": 0.95 * mm});
            skCircle(sketch, "E41.13.10.0", {"center": v(3.62, 29.52) * mm, "radius": 0.95 * mm});
            skCircle(sketch, "E41.13.11.0", {"center": v(3.62, 25.7) * mm, "radius": 0.95 * mm});
            skCircle(sketch, "E41.13.12.0", {"center": v(3.62, 21.9) * mm, "radius": 0.95 * mm});
            skCircle(sketch, "E41.13.13.0", {"center": v(3.62, 18.09) * mm, "radius": 0.95 * mm});
            skCircle(sketch, "E41.13.14.0", {"center": v(3.62, 14.28) * mm, "radius": 0.95 * mm});
            skCircle(sketch, "E41.14.0.0", {"center": v(7.43, 67.62) * mm, "radius": 0.95 * mm});
            skCircle(sketch, "E41.14.1.0", {"center": v(7.43, 63.8) * mm, "radius": 0.95 * mm});
            skCircle(sketch, "E41.14.2.0", {"center": v(7.43, 60) * mm, "radius": 0.95 * mm});
            skCircle(sketch, "E41.14.3.0", {"center": v(7.43, 56.19) * mm, "radius": 0.95 * mm});
            skCircle(sketch, "E41.14.4.0", {"center": v(7.43, 52.38) * mm, "radius": 0.95 * mm});
            skCircle(sketch, "E41.14.5.0", {"center": v(7.43, 48.57) * mm, "radius": 0.95 * mm});
            skCircle(sketch, "E41.14.6.0", {"center": v(7.43, 44.76) * mm, "radius": 0.95 * mm});
            skCircle(sketch, "E41.14.7.0", {"center": v(7.43, 40.95) * mm, "radius": 0.95 * mm});
            skCircle(sketch, "E41.14.8.0", {"center": v(7.43, 37.14) * mm, "radius": 0.95 * mm});
            skCircle(sketch, "E41.14.9.0", {"center": v(7.43, 33.33) * mm, "radius": 0.95 * mm});
            skCircle(sketch, "E41.14.10.0", {"center": v(7.43, 29.52) * mm, "radius": 0.95 * mm});
            skCircle(sketch, "E41.14.11.0", {"center": v(7.43, 25.7) * mm, "radius": 0.95 * mm});
            skCircle(sketch, "E41.14.12.0", {"center": v(7.43, 21.9) * mm, "radius": 0.95 * mm});
            skCircle(sketch, "E41.14.13.0", {"center": v(7.43, 18.09) * mm, "radius": 0.95 * mm});
            skCircle(sketch, "E41.14.14.0", {"center": v(7.43, 14.28) * mm, "radius": 0.95 * mm});
            skCircle(sketch, "E41.15.0.0", {"center": v(11.24, 67.62) * mm, "radius": 0.95 * mm});
            skCircle(sketch, "E41.15.1.0", {"center": v(11.24, 63.8) * mm, "radius": 0.95 * mm});
            skCircle(sketch, "E41.15.2.0", {"center": v(11.24, 60) * mm, "radius": 0.95 * mm});
            skCircle(sketch, "E41.15.3.0", {"center": v(11.24, 56.19) * mm, "radius": 0.95 * mm});
            skCircle(sketch, "E41.15.4.0", {"center": v(11.24, 52.38) * mm, "radius": 0.95 * mm});
            skCircle(sketch, "E41.15.5.0", {"center": v(11.24, 48.57) * mm, "radius": 0.95 * mm});
            skCircle(sketch, "E41.15.6.0", {"center": v(11.24, 44.76) * mm, "radius": 0.95 * mm});
            skCircle(sketch, "E41.15.7.0", {"center": v(11.24, 40.95) * mm, "radius": 0.95 * mm});
            skCircle(sketch, "E41.15.8.0", {"center": v(11.24, 37.14) * mm, "radius": 0.95 * mm});
            skCircle(sketch, "E41.15.9.0", {"center": v(11.24, 33.33) * mm, "radius": 0.95 * mm});
            skCircle(sketch, "E41.15.10.0", {"center": v(11.24, 29.52) * mm, "radius": 0.95 * mm});
            skCircle(sketch, "E41.15.11.0", {"center": v(11.24, 25.7) * mm, "radius": 0.95 * mm});
            skCircle(sketch, "E41.15.12.0", {"center": v(11.24, 21.9) * mm, "radius": 0.95 * mm});
            skCircle(sketch, "E41.15.13.0", {"center": v(11.24, 18.09) * mm, "radius": 0.95 * mm});
            skCircle(sketch, "E41.15.14.0", {"center": v(11.24, 14.28) * mm, "radius": 0.95 * mm});
            skCircle(sketch, "E41.16.0.0", {"center": v(15.05, 67.62) * mm, "radius": 0.95 * mm});
            skCircle(sketch, "E41.16.1.0", {"center": v(15.05, 63.8) * mm, "radius": 0.95 * mm});
            skCircle(sketch, "E41.16.2.0", {"center": v(15.05, 60) * mm, "radius": 0.95 * mm});
            skCircle(sketch, "E41.16.3.0", {"center": v(15.05, 56.19) * mm, "radius": 0.95 * mm});
            skCircle(sketch, "E41.16.4.0", {"center": v(15.05, 52.38) * mm, "radius": 0.95 * mm});
            skCircle(sketch, "E41.16.5.0", {"center": v(15.05, 48.57) * mm, "radius": 0.95 * mm});
            skCircle(sketch, "E41.16.6.0", {"center": v(15.05, 44.76) * mm, "radius": 0.95 * mm});
            skCircle(sketch, "E41.16.7.0", {"center": v(15.05, 40.95) * mm, "radius": 0.95 * mm});
            skCircle(sketch, "E41.16.8.0", {"center": v(15.05, 37.14) * mm, "radius": 0.95 * mm});
            skCircle(sketch, "E41.16.9.0", {"center": v(15.05, 33.33) * mm, "radius": 0.95 * mm});
            skCircle(sketch, "E41.16.10.0", {"center": v(15.05, 29.52) * mm, "radius": 0.95 * mm});
            skCircle(sketch, "E41.16.11.0", {"center": v(15.05, 25.7) * mm, "radius": 0.95 * mm});
            skCircle(sketch, "E41.16.12.0", {"center": v(15.05, 21.9) * mm, "radius": 0.95 * mm});
            skCircle(sketch, "E41.16.13.0", {"center": v(15.05, 18.09) * mm, "radius": 0.95 * mm});
            skCircle(sketch, "E41.16.14.0", {"center": v(15.05, 14.28) * mm, "radius": 0.95 * mm});
            skCircle(sketch, "E41.17.0.0", {"center": v(18.86, 67.62) * mm, "radius": 0.95 * mm});
            skCircle(sketch, "E41.17.1.0", {"center": v(18.86, 63.8) * mm, "radius": 0.95 * mm});
            skCircle(sketch, "E41.17.2.0", {"center": v(18.86, 60) * mm, "radius": 0.95 * mm});
            skCircle(sketch, "E41.17.3.0", {"center": v(18.86, 56.19) * mm, "radius": 0.95 * mm});
            skCircle(sketch, "E41.17.4.0", {"center": v(18.86, 52.38) * mm, "radius": 0.95 * mm});
            skCircle(sketch, "E41.17.5.0", {"center": v(18.86, 48.57) * mm, "radius": 0.95 * mm});
            skCircle(sketch, "E41.17.6.0", {"center": v(18.86, 44.76) * mm, "radius": 0.95 * mm});
            skCircle(sketch, "E41.17.7.0", {"center": v(18.86, 40.95) * mm, "radius": 0.95 * mm});
            skCircle(sketch, "E41.17.8.0", {"center": v(18.86, 37.14) * mm, "radius": 0.95 * mm});
            skCircle(sketch, "E41.17.9.0", {"center": v(18.86, 33.33) * mm, "radius": 0.95 * mm});
            skCircle(sketch, "E41.17.10.0", {"center": v(18.86, 29.52) * mm, "radius": 0.95 * mm});
            skCircle(sketch, "E41.17.11.0", {"center": v(18.86, 25.7) * mm, "radius": 0.95 * mm});
            skCircle(sketch, "E41.17.12.0", {"center": v(18.86, 21.9) * mm, "radius": 0.95 * mm});
            skCircle(sketch, "E41.17.13.0", {"center": v(18.86, 18.09) * mm, "radius": 0.95 * mm});
            skCircle(sketch, "E41.17.14.0", {"center": v(18.86, 14.28) * mm, "radius": 0.95 * mm});
            skCircle(sketch, "E41.18.0.0", {"center": v(22.67, 67.62) * mm, "radius": 0.95 * mm});
            skCircle(sketch, "E41.18.1.0", {"center": v(22.67, 63.8) * mm, "radius": 0.95 * mm});
            skCircle(sketch, "E41.18.2.0", {"center": v(22.67, 60) * mm, "radius": 0.95 * mm});
            skCircle(sketch, "E41.18.3.0", {"center": v(22.67, 56.19) * mm, "radius": 0.95 * mm});
            skCircle(sketch, "E41.18.4.0", {"center": v(22.67, 52.38) * mm, "radius": 0.95 * mm});
            skCircle(sketch, "E41.18.5.0", {"center": v(22.67, 48.57) * mm, "radius": 0.95 * mm});
            skCircle(sketch, "E41.18.6.0", {"center": v(22.67, 44.76) * mm, "radius": 0.95 * mm});
            skCircle(sketch, "E41.18.7.0", {"center": v(22.67, 40.95) * mm, "radius": 0.95 * mm});
            skCircle(sketch, "E41.18.8.0", {"center": v(22.67, 37.14) * mm, "radius": 0.95 * mm});
            skCircle(sketch, "E41.18.9.0", {"center": v(22.67, 33.33) * mm, "radius": 0.95 * mm});
            skCircle(sketch, "E41.18.10.0", {"center": v(22.67, 29.52) * mm, "radius": 0.95 * mm});
            skCircle(sketch, "E41.18.11.0", {"center": v(22.67, 25.7) * mm, "radius": 0.95 * mm});
            skCircle(sketch, "E41.18.12.0", {"center": v(22.67, 21.9) * mm, "radius": 0.95 * mm});
            skCircle(sketch, "E41.18.13.0", {"center": v(22.67, 18.09) * mm, "radius": 0.95 * mm});
            skCircle(sketch, "E41.18.14.0", {"center": v(22.67, 14.28) * mm, "radius": 0.95 * mm});
            skCircle(sketch, "E41.19.0.0", {"center": v(26.48, 67.62) * mm, "radius": 0.95 * mm});
            skCircle(sketch, "E41.19.1.0", {"center": v(26.48, 63.8) * mm, "radius": 0.95 * mm});
            skCircle(sketch, "E41.19.2.0", {"center": v(26.48, 60) * mm, "radius": 0.95 * mm});
            skCircle(sketch, "E41.19.3.0", {"center": v(26.48, 56.19) * mm, "radius": 0.95 * mm});
            skCircle(sketch, "E41.19.4.0", {"center": v(26.48, 52.38) * mm, "radius": 0.95 * mm});
            skCircle(sketch, "E41.19.5.0", {"center": v(26.48, 48.57) * mm, "radius": 0.95 * mm});
            skCircle(sketch, "E41.19.6.0", {"center": v(26.48, 44.76) * mm, "radius": 0.95 * mm});
            skCircle(sketch, "E41.19.7.0", {"center": v(26.48, 40.95) * mm, "radius": 0.95 * mm});
            skCircle(sketch, "E41.19.8.0", {"center": v(26.48, 37.14) * mm, "radius": 0.95 * mm});
            skCircle(sketch, "E41.19.9.0", {"center": v(26.48, 33.33) * mm, "radius": 0.95 * mm});
            skCircle(sketch, "E41.19.10.0", {"center": v(26.48, 29.52) * mm, "radius": 0.95 * mm});
            skCircle(sketch, "E41.19.11.0", {"center": v(26.48, 25.7) * mm, "radius": 0.95 * mm});
            skCircle(sketch, "E41.19.12.0", {"center": v(26.48, 21.9) * mm, "radius": 0.95 * mm});
            skCircle(sketch, "E41.19.13.0", {"center": v(26.48, 18.09) * mm, "radius": 0.95 * mm});
            skCircle(sketch, "E41.19.14.0", {"center": v(26.48, 14.28) * mm, "radius": 0.95 * mm});
            skCircle(sketch, "E41.20.0.0", {"center": v(30.3, 67.62) * mm, "radius": 0.95 * mm});
            skCircle(sketch, "E41.20.1.0", {"center": v(30.3, 63.8) * mm, "radius": 0.95 * mm});
            skCircle(sketch, "E41.20.2.0", {"center": v(30.3, 60) * mm, "radius": 0.95 * mm});
            skCircle(sketch, "E41.20.3.0", {"center": v(30.3, 56.19) * mm, "radius": 0.95 * mm});
            skCircle(sketch, "E41.20.4.0", {"center": v(30.3, 52.38) * mm, "radius": 0.95 * mm});
            skCircle(sketch, "E41.20.5.0", {"center": v(30.3, 48.57) * mm, "radius": 0.95 * mm});
            skCircle(sketch, "E41.20.6.0", {"center": v(30.3, 44.76) * mm, "radius": 0.95 * mm});
            skCircle(sketch, "E41.20.7.0", {"center": v(30.3, 40.95) * mm, "radius": 0.95 * mm});
            skCircle(sketch, "E41.20.8.0", {"center": v(30.3, 37.14) * mm, "radius": 0.95 * mm});
            skCircle(sketch, "E41.20.9.0", {"center": v(30.3, 33.33) * mm, "radius": 0.95 * mm});
            skCircle(sketch, "E41.20.10.0", {"center": v(30.3, 29.52) * mm, "radius": 0.95 * mm});
            skCircle(sketch, "E41.20.11.0", {"center": v(30.3, 25.7) * mm, "radius": 0.95 * mm});
            skCircle(sketch, "E41.20.12.0", {"center": v(30.3, 21.9) * mm, "radius": 0.95 * mm});
            skCircle(sketch, "E41.20.13.0", {"center": v(30.3, 18.09) * mm, "radius": 0.95 * mm});
            skCircle(sketch, "E41.20.14.0", {"center": v(30.3, 14.28) * mm, "radius": 0.95 * mm});
            skCircle(sketch, "E41.21.0.0", {"center": v(34.1, 67.62) * mm, "radius": 0.95 * mm});
            skCircle(sketch, "E41.21.1.0", {"center": v(34.1, 63.8) * mm, "radius": 0.95 * mm});
            skCircle(sketch, "E41.21.2.0", {"center": v(34.1, 60) * mm, "radius": 0.95 * mm});
            skCircle(sketch, "E41.21.3.0", {"center": v(34.1, 56.19) * mm, "radius": 0.95 * mm});
            skCircle(sketch, "E41.21.4.0", {"center": v(34.1, 52.38) * mm, "radius": 0.95 * mm});
            skCircle(sketch, "E41.21.5.0", {"center": v(34.1, 48.57) * mm, "radius": 0.95 * mm});
            skCircle(sketch, "E41.21.6.0", {"center": v(34.1, 44.76) * mm, "radius": 0.95 * mm});
            skCircle(sketch, "E41.21.7.0", {"center": v(34.1, 40.95) * mm, "radius": 0.95 * mm});
            skCircle(sketch, "E41.21.8.0", {"center": v(34.1, 37.14) * mm, "radius": 0.95 * mm});
            skCircle(sketch, "E41.21.9.0", {"center": v(34.1, 33.33) * mm, "radius": 0.95 * mm});
            skCircle(sketch, "E41.21.10.0", {"center": v(34.1, 29.52) * mm, "radius": 0.95 * mm});
            skCircle(sketch, "E41.21.11.0", {"center": v(34.1, 25.7) * mm, "radius": 0.95 * mm});
            skCircle(sketch, "E41.21.12.0", {"center": v(34.1, 21.9) * mm, "radius": 0.95 * mm});
            skCircle(sketch, "E41.21.13.0", {"center": v(34.1, 18.09) * mm, "radius": 0.95 * mm});
            skCircle(sketch, "E41.21.14.0", {"center": v(34.1, 14.28) * mm, "radius": 0.95 * mm});
            skCircle(sketch, "E41.22.0.0", {"center": v(37.91, 67.62) * mm, "radius": 0.95 * mm});
            skCircle(sketch, "E41.22.1.0", {"center": v(37.91, 63.8) * mm, "radius": 0.95 * mm});
            skCircle(sketch, "E41.22.2.0", {"center": v(37.91, 60) * mm, "radius": 0.95 * mm});
            skCircle(sketch, "E41.22.3.0", {"center": v(37.91, 56.19) * mm, "radius": 0.95 * mm});
            skCircle(sketch, "E41.22.4.0", {"center": v(37.91, 52.38) * mm, "radius": 0.95 * mm});
            skCircle(sketch, "E41.22.5.0", {"center": v(37.91, 48.57) * mm, "radius": 0.95 * mm});
            skCircle(sketch, "E41.22.6.0", {"center": v(37.91, 44.76) * mm, "radius": 0.95 * mm});
            skCircle(sketch, "E41.22.7.0", {"center": v(37.91, 40.95) * mm, "radius": 0.95 * mm});
            skCircle(sketch, "E41.22.8.0", {"center": v(37.91, 37.14) * mm, "radius": 0.95 * mm});
            skCircle(sketch, "E41.22.9.0", {"center": v(37.91, 33.33) * mm, "radius": 0.95 * mm});
            skCircle(sketch, "E41.22.10.0", {"center": v(37.91, 29.52) * mm, "radius": 0.95 * mm});
            skCircle(sketch, "E41.22.11.0", {"center": v(37.91, 25.7) * mm, "radius": 0.95 * mm});
            skCircle(sketch, "E41.22.12.0", {"center": v(37.91, 21.9) * mm, "radius": 0.95 * mm});
            skCircle(sketch, "E41.22.13.0", {"center": v(37.91, 18.09) * mm, "radius": 0.95 * mm});
            skCircle(sketch, "E41.22.14.0", {"center": v(37.91, 14.28) * mm, "radius": 0.95 * mm});
            skCircle(sketch, "E41.23.0.0", {"center": v(41.72, 67.62) * mm, "radius": 0.95 * mm});
            skCircle(sketch, "E41.23.1.0", {"center": v(41.72, 63.8) * mm, "radius": 0.95 * mm});
            skCircle(sketch, "E41.23.2.0", {"center": v(41.72, 60) * mm, "radius": 0.95 * mm});
            skCircle(sketch, "E41.23.3.0", {"center": v(41.72, 56.19) * mm, "radius": 0.95 * mm});
            skCircle(sketch, "E41.23.4.0", {"center": v(41.72, 52.38) * mm, "radius": 0.95 * mm});
            skCircle(sketch, "E41.23.5.0", {"center": v(41.72, 48.57) * mm, "radius": 0.95 * mm});
            skCircle(sketch, "E41.23.6.0", {"center": v(41.72, 44.76) * mm, "radius": 0.95 * mm});
            skCircle(sketch, "E41.23.7.0", {"center": v(41.72, 40.95) * mm, "radius": 0.95 * mm});
            skCircle(sketch, "E41.23.8.0", {"center": v(41.72, 37.14) * mm, "radius": 0.95 * mm});
            skCircle(sketch, "E41.23.9.0", {"center": v(41.72, 33.33) * mm, "radius": 0.95 * mm});
            skCircle(sketch, "E41.23.10.0", {"center": v(41.72, 29.52) * mm, "radius": 0.95 * mm});
            skCircle(sketch, "E41.23.11.0", {"center": v(41.72, 25.7) * mm, "radius": 0.95 * mm});
            skCircle(sketch, "E41.23.12.0", {"center": v(41.72, 21.9) * mm, "radius": 0.95 * mm});
            skCircle(sketch, "E41.23.13.0", {"center": v(41.72, 18.09) * mm, "radius": 0.95 * mm});
            skCircle(sketch, "E41.23.14.0", {"center": v(41.72, 14.28) * mm, "radius": 0.95 * mm});
            skCircle(sketch, "E41.24.0.0", {"center": v(45.53, 67.62) * mm, "radius": 0.95 * mm});
            skCircle(sketch, "E41.24.1.0", {"center": v(45.53, 63.8) * mm, "radius": 0.95 * mm});
            skCircle(sketch, "E41.24.2.0", {"center": v(45.53, 60) * mm, "radius": 0.95 * mm});
            skCircle(sketch, "E41.24.3.0", {"center": v(45.53, 56.19) * mm, "radius": 0.95 * mm});
            skCircle(sketch, "E41.24.4.0", {"center": v(45.53, 52.38) * mm, "radius": 0.95 * mm});
            skCircle(sketch, "E41.24.5.0", {"center": v(45.53, 48.57) * mm, "radius": 0.95 * mm});
            skCircle(sketch, "E41.24.6.0", {"center": v(45.53, 44.76) * mm, "radius": 0.95 * mm});
            skCircle(sketch, "E41.24.7.0", {"center": v(45.53, 40.95) * mm, "radius": 0.95 * mm});
            skCircle(sketch, "E41.24.8.0", {"center": v(45.53, 37.14) * mm, "radius": 0.95 * mm});
            skCircle(sketch, "E41.24.9.0", {"center": v(45.53, 33.33) * mm, "radius": 0.95 * mm});
            skCircle(sketch, "E41.24.10.0", {"center": v(45.53, 29.52) * mm, "radius": 0.95 * mm});
            skCircle(sketch, "E41.24.11.0", {"center": v(45.53, 25.7) * mm, "radius": 0.95 * mm});
            skCircle(sketch, "E41.24.12.0", {"center": v(45.53, 21.9) * mm, "radius": 0.95 * mm});
            skCircle(sketch, "E41.24.13.0", {"center": v(45.53, 18.09) * mm, "radius": 0.95 * mm});
            skCircle(sketch, "E41.24.14.0", {"center": v(45.53, 14.28) * mm, "radius": 0.95 * mm});
            skLineSegment(sketch, "E41.direction1", {"start": v(-45.9, 67.62) * mm, "end": v(-42.1, 67.62) * mm, "construction": true});
            skLineSegment(sketch, "E41.direction2", {"start": v(-45.9, 67.62) * mm, "end": v(-45.9, 63.8) * mm, "construction": true});
            skSolve(sketch);
        }
        {
            var Q0;
            Q0=makeQuery(id+"F10.imprint","IMPRINT",FACE,{"disambiguationData":[TD([[makeQuery(id+"F10.imprint","IMPRINT",EDGE,{"derivedFrom":sQuery(id+"F10.wireOp",EDGE,"E41.5.13.0")}),1.0]])]});
            var Q1;
            Q1=makeQuery(id+"F10.imprint","IMPRINT",FACE,{"disambiguationData":[TD([[makeQuery(id+"F10.imprint","IMPRINT",EDGE,{"derivedFrom":sQuery(id+"F10.wireOp",EDGE,"E41.4.12.0")}),1.0]])]});
            var Q2;
            Q2=makeQuery(id+"F10.imprint","IMPRINT",FACE,{"disambiguationData":[TD([[makeQuery(id+"F10.imprint","IMPRINT",EDGE,{"derivedFrom":sQuery(id+"F10.wireOp",EDGE,"E41.3.11.0")}),1.0]])]});
            var Q3;
            Q3=makeQuery(id+"F10.imprint","IMPRINT",FACE,{"disambiguationData":[TD([[makeQuery(id+"F10.imprint","IMPRINT",EDGE,{"derivedFrom":sQuery(id+"F10.wireOp",EDGE,"E41.11.3.0")}),1.0]])]});
            var Q4;
            Q4=makeQuery(id+"F10.imprint","IMPRINT",FACE,{"disambiguationData":[TD([[makeQuery(id+"F10.imprint","IMPRINT",EDGE,{"derivedFrom":sQuery(id+"F10.wireOp",EDGE,"E41.10.2.0")}),1.0]])]});
            var Q5;
            Q5=makeQuery(id+"F10.imprint","IMPRINT",FACE,{"disambiguationData":[TD([[makeQuery(id+"F10.imprint","IMPRINT",EDGE,{"derivedFrom":sQuery(id+"F10.wireOp",EDGE,"E41.9.1.0")}),1.0]])]});
            var Q6;
            Q6=makeQuery(id+"F10.imprint","IMPRINT",FACE,{"disambiguationData":[TD([[makeQuery(id+"F10.imprint","IMPRINT",EDGE,{"derivedFrom":sQuery(id+"F10.wireOp",EDGE,"E41.8.0.0")}),1.0]])]});
            var Q7;
            Q7=makeQuery(id+"F10.imprint","IMPRINT",FACE,{"disambiguationData":[TD([[makeQuery(id+"F10.imprint","IMPRINT",EDGE,{"derivedFrom":sQuery(id+"F10.wireOp",EDGE,"E41.15.7.0")}),1.0]])]});
            var Q8;
            Q8=makeQuery(id+"F10.imprint","IMPRINT",FACE,{"disambiguationData":[TD([[makeQuery(id+"F10.imprint","IMPRINT",EDGE,{"derivedFrom":sQuery(id+"F10.wireOp",EDGE,"E41.14.6.0")}),1.0]])]});
            var Q9;
            Q9=makeQuery(id+"F10.imprint","IMPRINT",FACE,{"disambiguationData":[TD([[makeQuery(id+"F10.imprint","IMPRINT",EDGE,{"derivedFrom":sQuery(id+"F10.wireOp",EDGE,"E41.13.5.0")}),1.0]])]});
            var Q10;
            Q10=makeQuery(id+"F10.imprint","IMPRINT",FACE,{"disambiguationData":[TD([[makeQuery(id+"F10.imprint","IMPRINT",EDGE,{"derivedFrom":sQuery(id+"F10.wireOp",EDGE,"E41.12.4.0")}),1.0]])]});
            var Q11;
            Q11=makeQuery(id+"F10.imprint","IMPRINT",FACE,{"disambiguationData":[TD([[makeQuery(id+"F10.imprint","IMPRINT",EDGE,{"derivedFrom":sQuery(id+"F10.wireOp",EDGE,"E41.19.11.0")}),1.0]])]});
            var Q12;
            Q12=makeQuery(id+"F10.imprint","IMPRINT",FACE,{"disambiguationData":[TD([[makeQuery(id+"F10.imprint","IMPRINT",EDGE,{"derivedFrom":sQuery(id+"F10.wireOp",EDGE,"E41.18.10.0")}),1.0]])]});
            var Q13;
            Q13=makeQuery(id+"F10.imprint","IMPRINT",FACE,{"disambiguationData":[TD([[makeQuery(id+"F10.imprint","IMPRINT",EDGE,{"derivedFrom":sQuery(id+"F10.wireOp",EDGE,"E41.16.8.0")}),1.0]])]});
            var Q14;
            Q14=makeQuery(id+"F10.imprint","IMPRINT",FACE,{"disambiguationData":[TD([[makeQuery(id+"F10.imprint","IMPRINT",EDGE,{"derivedFrom":sQuery(id+"F10.wireOp",EDGE,"E41.24.0.0")}),1.0]])]});
            var Q15;
            Q15=makeQuery(id+"F10.imprint","IMPRINT",FACE,{"disambiguationData":[TD([[makeQuery(id+"F10.imprint","IMPRINT",EDGE,{"derivedFrom":sQuery(id+"F10.wireOp",EDGE,"E41.21.13.0")}),1.0]])]});
            var Q16;
            Q16=makeQuery(id+"F10.imprint","IMPRINT",FACE,{"disambiguationData":[TD([[makeQuery(id+"F10.imprint","IMPRINT",EDGE,{"derivedFrom":sQuery(id+"F10.wireOp",EDGE,"E41.20.12.0")}),1.0]])]});
            var Q17;
            Q17=makeQuery(id+"F10.imprint","IMPRINT",FACE,{"disambiguationData":[TD([[makeQuery(id+"F10.imprint","IMPRINT",EDGE,{"derivedFrom":sQuery(id+"F10.wireOp",EDGE,"E41.0.13.0")}),1.0]])]});
            var Q18;
            Q18=makeQuery(id+"F10.imprint","IMPRINT",FACE,{"disambiguationData":[TD([[makeQuery(id+"F10.imprint","IMPRINT",EDGE,{"derivedFrom":sQuery(id+"F10.wireOp",EDGE,"E41.0.2.0")}),1.0]])]});
            var Q19;
            Q19=makeQuery(id+"F10.imprint","IMPRINT",FACE,{"disambiguationData":[TD([[makeQuery(id+"F10.imprint","IMPRINT",EDGE,{"derivedFrom":sQuery(id+"F10.wireOp",EDGE,"E41.0.3.0")}),1.0]])]});
            var Q20;
            Q20=makeQuery(id+"F10.imprint","IMPRINT",FACE,{"disambiguationData":[TD([[makeQuery(id+"F10.imprint","IMPRINT",EDGE,{"derivedFrom":sQuery(id+"F10.wireOp",EDGE,"E41.0.4.0")}),1.0]])]});
            var Q21;
            Q21=makeQuery(id+"F10.imprint","IMPRINT",FACE,{"disambiguationData":[TD([[makeQuery(id+"F10.imprint","IMPRINT",EDGE,{"derivedFrom":sQuery(id+"F10.wireOp",EDGE,"E41.0.7.0")}),1.0]])]});
            var Q22;
            Q22=makeQuery(id+"F10.imprint","IMPRINT",FACE,{"disambiguationData":[TD([[makeQuery(id+"F10.imprint","IMPRINT",EDGE,{"derivedFrom":sQuery(id+"F10.wireOp",EDGE,"E41.0.8.0")}),1.0]])]});
            var Q23;
            Q23=makeQuery(id+"F10.imprint","IMPRINT",FACE,{"disambiguationData":[TD([[makeQuery(id+"F10.imprint","IMPRINT",EDGE,{"derivedFrom":sQuery(id+"F10.wireOp",EDGE,"E41.0.12.0")}),1.0]])]});
            var Q24;
            Q24=makeQuery(id+"F10.imprint","IMPRINT",FACE,{"disambiguationData":[TD([[makeQuery(id+"F10.imprint","IMPRINT",EDGE,{"derivedFrom":sQuery(id+"F10.wireOp",EDGE,"E41.4.13.0")}),1.0]])]});
            var Q25;
            Q25=makeQuery(id+"F10.imprint","IMPRINT",FACE,{"disambiguationData":[TD([[makeQuery(id+"F10.imprint","IMPRINT",EDGE,{"derivedFrom":sQuery(id+"F10.wireOp",EDGE,"E41.3.12.0")}),1.0]])]});
            var Q26;
            Q26=makeQuery(id+"F10.imprint","IMPRINT",FACE,{"disambiguationData":[TD([[makeQuery(id+"F10.imprint","IMPRINT",EDGE,{"derivedFrom":sQuery(id+"F10.wireOp",EDGE,"E41.11.4.0")}),1.0]])]});
            var Q27;
            Q27=makeQuery(id+"F10.imprint","IMPRINT",FACE,{"disambiguationData":[TD([[makeQuery(id+"F10.imprint","IMPRINT",EDGE,{"derivedFrom":sQuery(id+"F10.wireOp",EDGE,"E41.10.3.0")}),1.0]])]});
            var Q28;
            Q28=makeQuery(id+"F10.imprint","IMPRINT",FACE,{"disambiguationData":[TD([[makeQuery(id+"F10.imprint","IMPRINT",EDGE,{"derivedFrom":sQuery(id+"F10.wireOp",EDGE,"E41.9.2.0")}),1.0]])]});
            var Q29;
            Q29=makeQuery(id+"F10.imprint","IMPRINT",FACE,{"disambiguationData":[TD([[makeQuery(id+"F10.imprint","IMPRINT",EDGE,{"derivedFrom":sQuery(id+"F10.wireOp",EDGE,"E41.8.1.0")}),1.0]])]});
            var Q30;
            Q30=makeQuery(id+"F10.imprint","IMPRINT",FACE,{"disambiguationData":[TD([[makeQuery(id+"F10.imprint","IMPRINT",EDGE,{"derivedFrom":sQuery(id+"F10.wireOp",EDGE,"E41.15.8.0")}),1.0]])]});
            var Q31;
            Q31=makeQuery(id+"F10.imprint","IMPRINT",FACE,{"disambiguationData":[TD([[makeQuery(id+"F10.imprint","IMPRINT",EDGE,{"derivedFrom":sQuery(id+"F10.wireOp",EDGE,"E41.14.7.0")}),1.0]])]});
            var Q32;
            Q32=makeQuery(id+"F10.imprint","IMPRINT",FACE,{"disambiguationData":[TD([[makeQuery(id+"F10.imprint","IMPRINT",EDGE,{"derivedFrom":sQuery(id+"F10.wireOp",EDGE,"E41.13.6.0")}),1.0]])]});
            var Q33;
            Q33=makeQuery(id+"F10.imprint","IMPRINT",FACE,{"disambiguationData":[TD([[makeQuery(id+"F10.imprint","IMPRINT",EDGE,{"derivedFrom":sQuery(id+"F10.wireOp",EDGE,"E41.19.12.0")}),1.0]])]});
            var Q34;
            Q34=makeQuery(id+"F10.imprint","IMPRINT",FACE,{"disambiguationData":[TD([[makeQuery(id+"F10.imprint","IMPRINT",EDGE,{"derivedFrom":sQuery(id+"F10.wireOp",EDGE,"E41.18.11.0")}),1.0]])]});
            var Q35;
            Q35=makeQuery(id+"F10.imprint","IMPRINT",FACE,{"disambiguationData":[TD([[makeQuery(id+"F10.imprint","IMPRINT",EDGE,{"derivedFrom":sQuery(id+"F10.wireOp",EDGE,"E41.24.1.0")}),1.0]])]});
            var Q36;
            Q36=makeQuery(id+"F10.imprint","IMPRINT",FACE,{"disambiguationData":[TD([[makeQuery(id+"F10.imprint","IMPRINT",EDGE,{"derivedFrom":sQuery(id+"F10.wireOp",EDGE,"E41.23.0.0")}),1.0]])]});
            var Q37;
            Q37=makeQuery(id+"F10.imprint","IMPRINT",FACE,{"disambiguationData":[TD([[makeQuery(id+"F10.imprint","IMPRINT",EDGE,{"derivedFrom":sQuery(id+"F10.wireOp",EDGE,"E41.20.13.0")}),1.0]])]});
            var Q38;
            Q38=makeQuery(id+"F10.imprint","IMPRINT",FACE,{"disambiguationData":[TD([[makeQuery(id+"F10.imprint","IMPRINT",EDGE,{"derivedFrom":sQuery(id+"F10.wireOp",EDGE,"E41.10.4.0")}),1.0]])]});
            var Q39;
            Q39=makeQuery(id+"F10.imprint","IMPRINT",FACE,{"disambiguationData":[TD([[makeQuery(id+"F10.imprint","IMPRINT",EDGE,{"derivedFrom":sQuery(id+"F10.wireOp",EDGE,"E41.9.3.0")}),1.0]])]});
            var Q40;
            Q40=makeQuery(id+"F10.imprint","IMPRINT",FACE,{"disambiguationData":[TD([[makeQuery(id+"F10.imprint","IMPRINT",EDGE,{"derivedFrom":sQuery(id+"F10.wireOp",EDGE,"E41.8.2.0")}),1.0]])]});
            var Q41;
            Q41=makeQuery(id+"F10.imprint","IMPRINT",FACE,{"disambiguationData":[TD([[makeQuery(id+"F10.imprint","IMPRINT",EDGE,{"derivedFrom":sQuery(id+"F10.wireOp",EDGE,"E41.14.8.0")}),1.0]])]});
            var Q42;
            Q42=makeQuery(id+"F10.imprint","IMPRINT",FACE,{"disambiguationData":[TD([[makeQuery(id+"F10.imprint","IMPRINT",EDGE,{"derivedFrom":sQuery(id+"F10.wireOp",EDGE,"E41.13.7.0")}),1.0]])]});
            var Q43;
            Q43=makeQuery(id+"F10.imprint","IMPRINT",FACE,{"disambiguationData":[TD([[makeQuery(id+"F10.imprint","IMPRINT",EDGE,{"derivedFrom":sQuery(id+"F10.wireOp",EDGE,"E41.19.13.0")}),1.0]])]});
            var Q44;
            Q44=makeQuery(id+"F10.imprint","IMPRINT",FACE,{"disambiguationData":[TD([[makeQuery(id+"F10.imprint","IMPRINT",EDGE,{"derivedFrom":sQuery(id+"F10.wireOp",EDGE,"E41.18.12.0")}),1.0]])]});
            var Q45;
            Q45=makeQuery(id+"F10.imprint","IMPRINT",FACE,{"disambiguationData":[TD([[makeQuery(id+"F10.imprint","IMPRINT",EDGE,{"derivedFrom":sQuery(id+"F10.wireOp",EDGE,"E41.24.2.0")}),1.0]])]});
            var Q46;
            Q46=makeQuery(id+"F10.imprint","IMPRINT",FACE,{"disambiguationData":[TD([[makeQuery(id+"F10.imprint","IMPRINT",EDGE,{"derivedFrom":sQuery(id+"F10.wireOp",EDGE,"E41.23.1.0")}),1.0]])]});
            var Q47;
            Q47=makeQuery(id+"F10.imprint","IMPRINT",FACE,{"disambiguationData":[TD([[makeQuery(id+"F10.imprint","IMPRINT",EDGE,{"derivedFrom":sQuery(id+"F10.wireOp",EDGE,"E41.2.12.0")}),1.0]])]});
            var Q48;
            Q48=makeQuery(id+"F10.imprint","IMPRINT",FACE,{"disambiguationData":[TD([[makeQuery(id+"F10.imprint","IMPRINT",EDGE,{"derivedFrom":sQuery(id+"F10.wireOp",EDGE,"E41.4.14.0")}),1.0]])]});
            var Q49;
            Q49=makeQuery(id+"F10.imprint","IMPRINT",FACE,{"disambiguationData":[TD([[makeQuery(id+"F10.imprint","IMPRINT",EDGE,{"derivedFrom":sQuery(id+"F10.wireOp",EDGE,"E41.3.13.0")}),1.0]])]});
            var Q50;
            Q50=makeQuery(id+"F10.imprint","IMPRINT",FACE,{"disambiguationData":[TD([[makeQuery(id+"F10.imprint","IMPRINT",EDGE,{"derivedFrom":sQuery(id+"F10.wireOp",EDGE,"E41.14.9.0")}),1.0]])]});
            var Q51;
            Q51=makeQuery(id+"F10.imprint","IMPRINT",FACE,{"disambiguationData":[TD([[makeQuery(id+"F10.imprint","IMPRINT",EDGE,{"derivedFrom":sQuery(id+"F10.wireOp",EDGE,"E41.13.8.0")}),1.0]])]});
            var Q52;
            Q52=makeQuery(id+"F10.imprint","IMPRINT",FACE,{"disambiguationData":[TD([[makeQuery(id+"F10.imprint","IMPRINT",EDGE,{"derivedFrom":sQuery(id+"F10.wireOp",EDGE,"E41.12.7.0")}),1.0]])]});
            var Q53;
            Q53=makeQuery(id+"F10.imprint","IMPRINT",FACE,{"disambiguationData":[TD([[makeQuery(id+"F10.imprint","IMPRINT",EDGE,{"derivedFrom":sQuery(id+"F10.wireOp",EDGE,"E41.19.14.0")}),1.0]])]});
            var Q54;
            Q54=makeQuery(id+"F10.imprint","IMPRINT",FACE,{"disambiguationData":[TD([[makeQuery(id+"F10.imprint","IMPRINT",EDGE,{"derivedFrom":sQuery(id+"F10.wireOp",EDGE,"E41.18.13.0")}),1.0]])]});
            var Q55;
            Q55=makeQuery(id+"F10.imprint","IMPRINT",FACE,{"disambiguationData":[TD([[makeQuery(id+"F10.imprint","IMPRINT",EDGE,{"derivedFrom":sQuery(id+"F10.wireOp",EDGE,"E41.17.12.0")}),1.0]])]});
            var Q56;
            Q56=makeQuery(id+"F10.imprint","IMPRINT",FACE,{"disambiguationData":[TD([[makeQuery(id+"F10.imprint","IMPRINT",EDGE,{"derivedFrom":sQuery(id+"F10.wireOp",EDGE,"E41.24.3.0")}),1.0]])]});
            var Q57;
            Q57=makeQuery(id+"F10.imprint","IMPRINT",FACE,{"disambiguationData":[TD([[makeQuery(id+"F10.imprint","IMPRINT",EDGE,{"derivedFrom":sQuery(id+"F10.wireOp",EDGE,"E41.23.2.0")}),1.0]])]});
            var Q58;
            Q58=makeQuery(id+"F10.imprint","IMPRINT",FACE,{"disambiguationData":[TD([[makeQuery(id+"F10.imprint","IMPRINT",EDGE,{"derivedFrom":sQuery(id+"F10.wireOp",EDGE,"E41.2.13.0")}),1.0]])]});
            var Q59;
            Q59=makeQuery(id+"F10.imprint","IMPRINT",FACE,{"disambiguationData":[TD([[makeQuery(id+"F10.imprint","IMPRINT",EDGE,{"derivedFrom":sQuery(id+"F10.wireOp",EDGE,"E41.1.12.0")}),1.0]])]});
            var Q60;
            Q60=makeQuery(id+"F10.imprint","IMPRINT",FACE,{"disambiguationData":[TD([[makeQuery(id+"F10.imprint","IMPRINT",EDGE,{"derivedFrom":sQuery(id+"F10.wireOp",EDGE,"E41.3.14.0")}),1.0]])]});
            var Q61;
            Q61=makeQuery(id+"F10.imprint","IMPRINT",FACE,{"disambiguationData":[TD([[makeQuery(id+"F10.imprint","IMPRINT",EDGE,{"derivedFrom":sQuery(id+"F10.wireOp",EDGE,"E41.9.4.0")}),1.0]])]});
            var Q62;
            Q62=makeQuery(id+"F10.imprint","IMPRINT",FACE,{"disambiguationData":[TD([[makeQuery(id+"F10.imprint","IMPRINT",EDGE,{"derivedFrom":sQuery(id+"F10.wireOp",EDGE,"E41.8.3.0")}),1.0]])]});
            var Q63;
            Q63=makeQuery(id+"F10.imprint","IMPRINT",FACE,{"disambiguationData":[TD([[makeQuery(id+"F10.imprint","IMPRINT",EDGE,{"derivedFrom":sQuery(id+"F10.wireOp",EDGE,"E41.18.14.0")}),1.0]])]});
            var Q64;
            Q64=makeQuery(id+"F10.imprint","IMPRINT",FACE,{"disambiguationData":[TD([[makeQuery(id+"F10.imprint","IMPRINT",EDGE,{"derivedFrom":sQuery(id+"F10.wireOp",EDGE,"E41.17.13.0")}),1.0]])]});
            var Q65;
            Q65=makeQuery(id+"F10.imprint","IMPRINT",FACE,{"disambiguationData":[TD([[makeQuery(id+"F10.imprint","IMPRINT",EDGE,{"derivedFrom":sQuery(id+"F10.wireOp",EDGE,"E41.16.12.0")}),1.0]])]});
            var Q66;
            Q66=makeQuery(id+"F10.imprint","IMPRINT",FACE,{"disambiguationData":[TD([[makeQuery(id+"F10.imprint","IMPRINT",EDGE,{"derivedFrom":sQuery(id+"F10.wireOp",EDGE,"E41.24.4.0")}),1.0]])]});
            var Q67;
            Q67=makeQuery(id+"F10.imprint","IMPRINT",FACE,{"disambiguationData":[TD([[makeQuery(id+"F10.imprint","IMPRINT",EDGE,{"derivedFrom":sQuery(id+"F10.wireOp",EDGE,"E41.23.3.0")}),1.0]])]});
            var Q68;
            Q68=makeQuery(id+"F10.imprint","IMPRINT",FACE,{"disambiguationData":[TD([[makeQuery(id+"F10.imprint","IMPRINT",EDGE,{"derivedFrom":sQuery(id+"F10.wireOp",EDGE,"E41.1.13.0")}),1.0]])]});
            var Q69;
            Q69=makeQuery(id+"F10.imprint","IMPRINT",FACE,{"disambiguationData":[TD([[makeQuery(id+"F10.imprint","IMPRINT",EDGE,{"derivedFrom":sQuery(id+"F10.wireOp",EDGE,"E41.7.3.0")}),1.0]])]});
            var Q70;
            Q70=makeQuery(id+"F10.imprint","IMPRINT",FACE,{"disambiguationData":[TD([[makeQuery(id+"F10.imprint","IMPRINT",EDGE,{"derivedFrom":sQuery(id+"F10.wireOp",EDGE,"E41.4.0.0")}),1.0]])]});
            var Q71;
            Q71=makeQuery(id+"F10.imprint","IMPRINT",FACE,{"disambiguationData":[TD([[makeQuery(id+"F10.imprint","IMPRINT",EDGE,{"derivedFrom":sQuery(id+"F10.wireOp",EDGE,"E41.11.7.0")}),1.0]])]});
            var Q72;
            Q72=makeQuery(id+"F10.imprint","IMPRINT",FACE,{"disambiguationData":[TD([[makeQuery(id+"F10.imprint","IMPRINT",EDGE,{"derivedFrom":sQuery(id+"F10.wireOp",EDGE,"E41.9.5.0")}),1.0]])]});
            var Q73;
            Q73=makeQuery(id+"F10.imprint","IMPRINT",FACE,{"disambiguationData":[TD([[makeQuery(id+"F10.imprint","IMPRINT",EDGE,{"derivedFrom":sQuery(id+"F10.wireOp",EDGE,"E41.8.4.0")}),1.0]])]});
            var Q74;
            Q74=makeQuery(id+"F10.imprint","IMPRINT",FACE,{"disambiguationData":[TD([[makeQuery(id+"F10.imprint","IMPRINT",EDGE,{"derivedFrom":sQuery(id+"F10.wireOp",EDGE,"E41.14.10.0")}),1.0]])]});
            var Q75;
            Q75=makeQuery(id+"F10.imprint","IMPRINT",FACE,{"disambiguationData":[TD([[makeQuery(id+"F10.imprint","IMPRINT",EDGE,{"derivedFrom":sQuery(id+"F10.wireOp",EDGE,"E41.13.9.0")}),1.0]])]});
            var Q76;
            Q76=makeQuery(id+"F10.imprint","IMPRINT",FACE,{"disambiguationData":[TD([[makeQuery(id+"F10.imprint","IMPRINT",EDGE,{"derivedFrom":sQuery(id+"F10.wireOp",EDGE,"E41.12.8.0")}),1.0]])]});
            var Q77;
            Q77=makeQuery(id+"F10.imprint","IMPRINT",FACE,{"disambiguationData":[TD([[makeQuery(id+"F10.imprint","IMPRINT",EDGE,{"derivedFrom":sQuery(id+"F10.wireOp",EDGE,"E41.4.6.0")}),1.0]])]});
            var Q78;
            Q78=makeQuery(id+"F10.imprint","IMPRINT",FACE,{"disambiguationData":[TD([[makeQuery(id+"F10.imprint","IMPRINT",EDGE,{"derivedFrom":sQuery(id+"F10.wireOp",EDGE,"E41.3.5.0")}),1.0]])]});
            var Q79;
            Q79=makeQuery(id+"F10.imprint","IMPRINT",FACE,{"disambiguationData":[TD([[makeQuery(id+"F10.imprint","IMPRINT",EDGE,{"derivedFrom":sQuery(id+"F10.wireOp",EDGE,"E41.2.4.0")}),1.0]])]});
            var Q80;
            Q80=makeQuery(id+"F10.imprint","IMPRINT",FACE,{"disambiguationData":[TD([[makeQuery(id+"F10.imprint","IMPRINT",EDGE,{"derivedFrom":sQuery(id+"F10.wireOp",EDGE,"E41.1.3.0")}),1.0]])]});
            var Q81;
            Q81=makeQuery(id+"F10.imprint","IMPRINT",FACE,{"disambiguationData":[TD([[makeQuery(id+"F10.imprint","IMPRINT",EDGE,{"derivedFrom":sQuery(id+"F10.wireOp",EDGE,"E41.8.10.0")}),1.0]])]});
            var Q82;
            Q82=makeQuery(id+"F10.imprint","IMPRINT",FACE,{"disambiguationData":[TD([[makeQuery(id+"F10.imprint","IMPRINT",EDGE,{"derivedFrom":sQuery(id+"F10.wireOp",EDGE,"E41.6.8.0")}),1.0]])]});
            var Q83;
            Q83=makeQuery(id+"F10.imprint","IMPRINT",FACE,{"disambiguationData":[TD([[makeQuery(id+"F10.imprint","IMPRINT",EDGE,{"derivedFrom":sQuery(id+"F10.wireOp",EDGE,"E41.5.7.0")}),1.0]])]});
            var Q84;
            Q84=makeQuery(id+"F10.imprint","IMPRINT",FACE,{"disambiguationData":[TD([[makeQuery(id+"F10.imprint","IMPRINT",EDGE,{"derivedFrom":sQuery(id+"F10.wireOp",EDGE,"E41.11.13.0")}),1.0]])]});
            var Q85;
            Q85=makeQuery(id+"F10.imprint","IMPRINT",FACE,{"disambiguationData":[TD([[makeQuery(id+"F10.imprint","IMPRINT",EDGE,{"derivedFrom":sQuery(id+"F10.wireOp",EDGE,"E41.10.12.0")}),1.0]])]});
            var Q86;
            Q86=makeQuery(id+"F10.imprint","IMPRINT",FACE,{"disambiguationData":[TD([[makeQuery(id+"F10.imprint","IMPRINT",EDGE,{"derivedFrom":sQuery(id+"F10.wireOp",EDGE,"E41.9.11.0")}),1.0]])]});
            var Q87;
            Q87=makeQuery(id+"F10.imprint","IMPRINT",FACE,{"disambiguationData":[TD([[makeQuery(id+"F10.imprint","IMPRINT",EDGE,{"derivedFrom":sQuery(id+"F10.wireOp",EDGE,"E41.17.3.0")}),1.0]])]});
            var Q88;
            Q88=makeQuery(id+"F10.imprint","IMPRINT",FACE,{"disambiguationData":[TD([[makeQuery(id+"F10.imprint","IMPRINT",EDGE,{"derivedFrom":sQuery(id+"F10.wireOp",EDGE,"E41.14.0.0")}),1.0]])]});
            var Q89;
            Q89=makeQuery(id+"F10.imprint","IMPRINT",FACE,{"disambiguationData":[TD([[makeQuery(id+"F10.imprint","IMPRINT",EDGE,{"derivedFrom":sQuery(id+"F10.wireOp",EDGE,"E41.21.7.0")}),1.0]])]});
            var Q90;
            Q90=makeQuery(id+"F10.imprint","IMPRINT",FACE,{"disambiguationData":[TD([[makeQuery(id+"F10.imprint","IMPRINT",EDGE,{"derivedFrom":sQuery(id+"F10.wireOp",EDGE,"E41.19.5.0")}),1.0]])]});
            var Q91;
            Q91=makeQuery(id+"F10.imprint","IMPRINT",FACE,{"disambiguationData":[TD([[makeQuery(id+"F10.imprint","IMPRINT",EDGE,{"derivedFrom":sQuery(id+"F10.wireOp",EDGE,"E41.18.4.0")}),1.0]])]});
            var Q92;
            Q92=makeQuery(id+"F10.imprint","IMPRINT",FACE,{"disambiguationData":[TD([[makeQuery(id+"F10.imprint","IMPRINT",EDGE,{"derivedFrom":sQuery(id+"F10.wireOp",EDGE,"E41.24.10.0")}),1.0]])]});
            var Q93;
            Q93=makeQuery(id+"F10.imprint","IMPRINT",FACE,{"disambiguationData":[TD([[makeQuery(id+"F10.imprint","IMPRINT",EDGE,{"derivedFrom":sQuery(id+"F10.wireOp",EDGE,"E41.23.9.0")}),1.0]])]});
            var Q94;
            Q94=makeQuery(id+"F10.imprint","IMPRINT",FACE,{"disambiguationData":[TD([[makeQuery(id+"F10.imprint","IMPRINT",EDGE,{"derivedFrom":sQuery(id+"F10.wireOp",EDGE,"E41.22.8.0")}),1.0]])]});
            var Q95;
            Q95=makeQuery(id+"F10.imprint","IMPRINT",FACE,{"disambiguationData":[TD([[makeQuery(id+"F10.imprint","IMPRINT",EDGE,{"derivedFrom":sQuery(id+"F10.wireOp",EDGE,"E41.4.7.0")}),1.0]])]});
            var Q96;
            Q96=makeQuery(id+"F10.imprint","IMPRINT",FACE,{"disambiguationData":[TD([[makeQuery(id+"F10.imprint","IMPRINT",EDGE,{"derivedFrom":sQuery(id+"F10.wireOp",EDGE,"E41.3.6.0")}),1.0]])]});
            var Q97;
            Q97=makeQuery(id+"F10.imprint","IMPRINT",FACE,{"disambiguationData":[TD([[makeQuery(id+"F10.imprint","IMPRINT",EDGE,{"derivedFrom":sQuery(id+"F10.wireOp",EDGE,"E41.1.4.0")}),1.0]])]});
            var Q98;
            Q98=makeQuery(id+"F10.imprint","IMPRINT",FACE,{"disambiguationData":[TD([[makeQuery(id+"F10.imprint","IMPRINT",EDGE,{"derivedFrom":sQuery(id+"F10.wireOp",EDGE,"E41.5.4.0")}),1.0]])]});
            var Q99;
            Q99=makeQuery(id+"F10.imprint","IMPRINT",FACE,{"disambiguationData":[TD([[makeQuery(id+"F10.imprint","IMPRINT",EDGE,{"derivedFrom":sQuery(id+"F10.wireOp",EDGE,"E41.4.3.0")}),1.0]])]});
            var Q100;
            Q100=makeQuery(id+"F10.imprint","IMPRINT",FACE,{"disambiguationData":[TD([[makeQuery(id+"F10.imprint","IMPRINT",EDGE,{"derivedFrom":sQuery(id+"F10.wireOp",EDGE,"E41.3.2.0")}),1.0]])]});
            var Q101;
            Q101=makeQuery(id+"F10.imprint","IMPRINT",FACE,{"disambiguationData":[TD([[makeQuery(id+"F10.imprint","IMPRINT",EDGE,{"derivedFrom":sQuery(id+"F10.wireOp",EDGE,"E41.9.8.0")}),1.0]])]});
            var Q102;
            Q102=makeQuery(id+"F10.imprint","IMPRINT",FACE,{"disambiguationData":[TD([[makeQuery(id+"F10.imprint","IMPRINT",EDGE,{"derivedFrom":sQuery(id+"F10.wireOp",EDGE,"E41.8.7.0")}),1.0]])]});
            var Q103;
            Q103=makeQuery(id+"F10.imprint","IMPRINT",FACE,{"disambiguationData":[TD([[makeQuery(id+"F10.imprint","IMPRINT",EDGE,{"derivedFrom":sQuery(id+"F10.wireOp",EDGE,"E41.13.12.0")}),1.0]])]});
            var Q104;
            Q104=makeQuery(id+"F10.imprint","IMPRINT",FACE,{"disambiguationData":[TD([[makeQuery(id+"F10.imprint","IMPRINT",EDGE,{"derivedFrom":sQuery(id+"F10.wireOp",EDGE,"E41.18.1.0")}),1.0]])]});
            var Q105;
            Q105=makeQuery(id+"F10.imprint","IMPRINT",FACE,{"disambiguationData":[TD([[makeQuery(id+"F10.imprint","IMPRINT",EDGE,{"derivedFrom":sQuery(id+"F10.wireOp",EDGE,"E41.14.13.0")}),1.0]])]});
            var Q106;
            Q106=makeQuery(id+"F10.imprint","IMPRINT",FACE,{"disambiguationData":[TD([[makeQuery(id+"F10.imprint","IMPRINT",EDGE,{"derivedFrom":sQuery(id+"F10.wireOp",EDGE,"E41.21.4.0")}),1.0]])]});
            var Q107;
            Q107=makeQuery(id+"F10.imprint","IMPRINT",FACE,{"disambiguationData":[TD([[makeQuery(id+"F10.imprint","IMPRINT",EDGE,{"derivedFrom":sQuery(id+"F10.wireOp",EDGE,"E41.20.3.0")}),1.0]])]});
            var Q108;
            Q108=makeQuery(id+"F10.imprint","IMPRINT",FACE,{"disambiguationData":[TD([[makeQuery(id+"F10.imprint","IMPRINT",EDGE,{"derivedFrom":sQuery(id+"F10.wireOp",EDGE,"E41.19.2.0")}),1.0]])]});
            var Q109;
            Q109=makeQuery(id+"F10.imprint","IMPRINT",FACE,{"disambiguationData":[TD([[makeQuery(id+"F10.imprint","IMPRINT",EDGE,{"derivedFrom":sQuery(id+"F10.wireOp",EDGE,"E41.24.7.0")}),1.0]])]});
            var Q110;
            Q110=makeQuery(id+"F10.imprint","IMPRINT",FACE,{"disambiguationData":[TD([[makeQuery(id+"F10.imprint","IMPRINT",EDGE,{"derivedFrom":sQuery(id+"F10.wireOp",EDGE,"E41.23.6.0")}),1.0]])]});
            var Q111;
            Q111=makeQuery(id+"F10.imprint","IMPRINT",FACE,{"disambiguationData":[TD([[makeQuery(id+"F10.imprint","IMPRINT",EDGE,{"derivedFrom":sQuery(id+"F10.wireOp",EDGE,"E41.8.11.0")}),1.0]])]});
            var Q112;
            Q112=makeQuery(id+"F10.imprint","IMPRINT",FACE,{"disambiguationData":[TD([[makeQuery(id+"F10.imprint","IMPRINT",EDGE,{"derivedFrom":sQuery(id+"F10.wireOp",EDGE,"E41.5.8.0")}),1.0]])]});
            var Q113;
            Q113=makeQuery(id+"F10.imprint","IMPRINT",FACE,{"disambiguationData":[TD([[makeQuery(id+"F10.imprint","IMPRINT",EDGE,{"derivedFrom":sQuery(id+"F10.wireOp",EDGE,"E41.13.0.0")}),1.0]])]});
            var Q114;
            Q114=makeQuery(id+"F10.imprint","IMPRINT",FACE,{"disambiguationData":[TD([[makeQuery(id+"F10.imprint","IMPRINT",EDGE,{"derivedFrom":sQuery(id+"F10.wireOp",EDGE,"E41.4.1.0")}),1.0]])]});
            var Q115;
            Q115=makeQuery(id+"F10.imprint","IMPRINT",FACE,{"disambiguationData":[TD([[makeQuery(id+"F10.imprint","IMPRINT",EDGE,{"derivedFrom":sQuery(id+"F10.wireOp",EDGE,"E41.10.13.0")}),1.0]])]});
            var Q116;
            Q116=makeQuery(id+"F10.imprint","IMPRINT",FACE,{"disambiguationData":[TD([[makeQuery(id+"F10.imprint","IMPRINT",EDGE,{"derivedFrom":sQuery(id+"F10.wireOp",EDGE,"E41.3.0.0")}),1.0]])]});
            var Q117;
            Q117=makeQuery(id+"F10.imprint","IMPRINT",FACE,{"disambiguationData":[TD([[makeQuery(id+"F10.imprint","IMPRINT",EDGE,{"derivedFrom":sQuery(id+"F10.wireOp",EDGE,"E41.9.12.0")}),1.0]])]});
            var Q118;
            Q118=makeQuery(id+"F10.imprint","IMPRINT",FACE,{"disambiguationData":[TD([[makeQuery(id+"F10.imprint","IMPRINT",EDGE,{"derivedFrom":sQuery(id+"F10.wireOp",EDGE,"E41.8.5.0")}),1.0]])]});
            var Q119;
            Q119=makeQuery(id+"F10.imprint","IMPRINT",FACE,{"disambiguationData":[TD([[makeQuery(id+"F10.imprint","IMPRINT",EDGE,{"derivedFrom":sQuery(id+"F10.wireOp",EDGE,"E41.7.4.0")}),1.0]])]});
            var Q120;
            Q120=makeQuery(id+"F10.imprint","IMPRINT",FACE,{"disambiguationData":[TD([[makeQuery(id+"F10.imprint","IMPRINT",EDGE,{"derivedFrom":sQuery(id+"F10.wireOp",EDGE,"E41.6.3.0")}),1.0]])]});
            var Q121;
            Q121=makeQuery(id+"F10.imprint","IMPRINT",FACE,{"disambiguationData":[TD([[makeQuery(id+"F10.imprint","IMPRINT",EDGE,{"derivedFrom":sQuery(id+"F10.wireOp",EDGE,"E41.5.2.0")}),1.0]])]});
            var Q122;
            Q122=makeQuery(id+"F10.imprint","IMPRINT",FACE,{"disambiguationData":[TD([[makeQuery(id+"F10.imprint","IMPRINT",EDGE,{"derivedFrom":sQuery(id+"F10.wireOp",EDGE,"E41.17.4.0")}),1.0]])]});
            var Q123;
            Q123=makeQuery(id+"F10.imprint","IMPRINT",FACE,{"disambiguationData":[TD([[makeQuery(id+"F10.imprint","IMPRINT",EDGE,{"derivedFrom":sQuery(id+"F10.wireOp",EDGE,"E41.16.3.0")}),1.0]])]});
            var Q124;
            Q124=makeQuery(id+"F10.imprint","IMPRINT",FACE,{"disambiguationData":[TD([[makeQuery(id+"F10.imprint","IMPRINT",EDGE,{"derivedFrom":sQuery(id+"F10.wireOp",EDGE,"E41.15.2.0")}),1.0]])]});
            var Q125;
            Q125=makeQuery(id+"F10.imprint","IMPRINT",FACE,{"disambiguationData":[TD([[makeQuery(id+"F10.imprint","IMPRINT",EDGE,{"derivedFrom":sQuery(id+"F10.wireOp",EDGE,"E41.11.8.0")}),1.0]])]});
            var Q126;
            Q126=makeQuery(id+"F10.imprint","IMPRINT",FACE,{"disambiguationData":[TD([[makeQuery(id+"F10.imprint","IMPRINT",EDGE,{"derivedFrom":sQuery(id+"F10.wireOp",EDGE,"E41.10.7.0")}),1.0]])]});
            var Q127;
            Q127=makeQuery(id+"F10.imprint","IMPRINT",FACE,{"disambiguationData":[TD([[makeQuery(id+"F10.imprint","IMPRINT",EDGE,{"derivedFrom":sQuery(id+"F10.wireOp",EDGE,"E41.9.6.0")}),1.0]])]});
            var Q128;
            Q128=makeQuery(id+"F10.imprint","IMPRINT",FACE,{"disambiguationData":[TD([[makeQuery(id+"F10.imprint","IMPRINT",EDGE,{"derivedFrom":sQuery(id+"F10.wireOp",EDGE,"E41.16.13.0")}),1.0]])]});
            var Q129;
            Q129=makeQuery(id+"F10.imprint","IMPRINT",FACE,{"disambiguationData":[TD([[makeQuery(id+"F10.imprint","IMPRINT",EDGE,{"derivedFrom":sQuery(id+"F10.wireOp",EDGE,"E41.15.12.0")}),1.0]])]});
            var Q130;
            Q130=makeQuery(id+"F10.imprint","IMPRINT",FACE,{"disambiguationData":[TD([[makeQuery(id+"F10.imprint","IMPRINT",EDGE,{"derivedFrom":sQuery(id+"F10.wireOp",EDGE,"E41.14.11.0")}),1.0]])]});
            var Q131;
            Q131=makeQuery(id+"F10.imprint","IMPRINT",FACE,{"disambiguationData":[TD([[makeQuery(id+"F10.imprint","IMPRINT",EDGE,{"derivedFrom":sQuery(id+"F10.wireOp",EDGE,"E41.13.10.0")}),1.0]])]});
            var Q132;
            Q132=makeQuery(id+"F10.imprint","IMPRINT",FACE,{"disambiguationData":[TD([[makeQuery(id+"F10.imprint","IMPRINT",EDGE,{"derivedFrom":sQuery(id+"F10.wireOp",EDGE,"E41.19.0.0")}),1.0]])]});
            var Q133;
            Q133=makeQuery(id+"F10.imprint","IMPRINT",FACE,{"disambiguationData":[TD([[makeQuery(id+"F10.imprint","IMPRINT",EDGE,{"derivedFrom":sQuery(id+"F10.wireOp",EDGE,"E41.24.5.0")}),1.0]])]});
            var Q134;
            Q134=makeQuery(id+"F10.imprint","IMPRINT",FACE,{"disambiguationData":[TD([[makeQuery(id+"F10.imprint","IMPRINT",EDGE,{"derivedFrom":sQuery(id+"F10.wireOp",EDGE,"E41.23.4.0")}),1.0]])]});
            var Q135;
            Q135=makeQuery(id+"F10.imprint","IMPRINT",FACE,{"disambiguationData":[TD([[makeQuery(id+"F10.imprint","IMPRINT",EDGE,{"derivedFrom":sQuery(id+"F10.wireOp",EDGE,"E41.14.1.0")}),1.0]])]});
            var Q136;
            Q136=makeQuery(id+"F10.imprint","IMPRINT",FACE,{"disambiguationData":[TD([[makeQuery(id+"F10.imprint","IMPRINT",EDGE,{"derivedFrom":sQuery(id+"F10.wireOp",EDGE,"E41.21.8.0")}),1.0]])]});
            var Q137;
            Q137=makeQuery(id+"F10.imprint","IMPRINT",FACE,{"disambiguationData":[TD([[makeQuery(id+"F10.imprint","IMPRINT",EDGE,{"derivedFrom":sQuery(id+"F10.wireOp",EDGE,"E41.20.7.0")}),1.0]])]});
            var Q138;
            Q138=makeQuery(id+"F10.imprint","IMPRINT",FACE,{"disambiguationData":[TD([[makeQuery(id+"F10.imprint","IMPRINT",EDGE,{"derivedFrom":sQuery(id+"F10.wireOp",EDGE,"E41.22.3.0")}),1.0]])]});
            var Q139;
            Q139=makeQuery(id+"F10.imprint","IMPRINT",FACE,{"disambiguationData":[TD([[makeQuery(id+"F10.imprint","IMPRINT",EDGE,{"derivedFrom":sQuery(id+"F10.wireOp",EDGE,"E41.19.6.0")}),1.0]])]});
            var Q140;
            Q140=makeQuery(id+"F10.imprint","IMPRINT",FACE,{"disambiguationData":[TD([[makeQuery(id+"F10.imprint","IMPRINT",EDGE,{"derivedFrom":sQuery(id+"F10.wireOp",EDGE,"E41.18.5.0")}),1.0]])]});
            var Q141;
            Q141=makeQuery(id+"F10.imprint","IMPRINT",FACE,{"disambiguationData":[TD([[makeQuery(id+"F10.imprint","IMPRINT",EDGE,{"derivedFrom":sQuery(id+"F10.wireOp",EDGE,"E41.24.11.0")}),1.0]])]});
            var Q142;
            Q142=makeQuery(id+"F10.imprint","IMPRINT",FACE,{"disambiguationData":[TD([[makeQuery(id+"F10.imprint","IMPRINT",EDGE,{"derivedFrom":sQuery(id+"F10.wireOp",EDGE,"E41.23.10.0")}),1.0]])]});
            var Q143;
            Q143=makeQuery(id+"F10.imprint","IMPRINT",FACE,{"disambiguationData":[TD([[makeQuery(id+"F10.imprint","IMPRINT",EDGE,{"derivedFrom":sQuery(id+"F10.wireOp",EDGE,"E41.4.2.0")}),1.0]])]});
            var Q144;
            Q144=makeQuery(id+"F10.imprint","IMPRINT",FACE,{"disambiguationData":[TD([[makeQuery(id+"F10.imprint","IMPRINT",EDGE,{"derivedFrom":sQuery(id+"F10.wireOp",EDGE,"E41.3.1.0")}),1.0]])]});
            var Q145;
            Q145=makeQuery(id+"F10.imprint","IMPRINT",FACE,{"disambiguationData":[TD([[makeQuery(id+"F10.imprint","IMPRINT",EDGE,{"derivedFrom":sQuery(id+"F10.wireOp",EDGE,"E41.4.8.0")}),1.0]])]});
            var Q146;
            Q146=makeQuery(id+"F10.imprint","IMPRINT",FACE,{"disambiguationData":[TD([[makeQuery(id+"F10.imprint","IMPRINT",EDGE,{"derivedFrom":sQuery(id+"F10.wireOp",EDGE,"E41.8.6.0")}),1.0]])]});
            var Q147;
            Q147=makeQuery(id+"F10.imprint","IMPRINT",FACE,{"disambiguationData":[TD([[makeQuery(id+"F10.imprint","IMPRINT",EDGE,{"derivedFrom":sQuery(id+"F10.wireOp",EDGE,"E41.6.4.0")}),1.0]])]});
            var Q148;
            Q148=makeQuery(id+"F10.imprint","IMPRINT",FACE,{"disambiguationData":[TD([[makeQuery(id+"F10.imprint","IMPRINT",EDGE,{"derivedFrom":sQuery(id+"F10.wireOp",EDGE,"E41.5.3.0")}),1.0]])]});
            var Q149;
            Q149=makeQuery(id+"F10.imprint","IMPRINT",FACE,{"disambiguationData":[TD([[makeQuery(id+"F10.imprint","IMPRINT",EDGE,{"derivedFrom":sQuery(id+"F10.wireOp",EDGE,"E41.10.8.0")}),1.0]])]});
            var Q150;
            Q150=makeQuery(id+"F10.imprint","IMPRINT",FACE,{"disambiguationData":[TD([[makeQuery(id+"F10.imprint","IMPRINT",EDGE,{"derivedFrom":sQuery(id+"F10.wireOp",EDGE,"E41.9.7.0")}),1.0]])]});
            var Q151;
            Q151=makeQuery(id+"F10.imprint","IMPRINT",FACE,{"disambiguationData":[TD([[makeQuery(id+"F10.imprint","IMPRINT",EDGE,{"derivedFrom":sQuery(id+"F10.wireOp",EDGE,"E41.3.7.0")}),1.0]])]});
            var Q152;
            Q152=makeQuery(id+"F10.imprint","IMPRINT",FACE,{"disambiguationData":[TD([[makeQuery(id+"F10.imprint","IMPRINT",EDGE,{"derivedFrom":sQuery(id+"F10.wireOp",EDGE,"E41.8.12.0")}),1.0]])]});
            var Q153;
            Q153=makeQuery(id+"F10.imprint","IMPRINT",FACE,{"disambiguationData":[TD([[makeQuery(id+"F10.imprint","IMPRINT",EDGE,{"derivedFrom":sQuery(id+"F10.wireOp",EDGE,"E41.15.13.0")}),1.0]])]});
            var Q154;
            Q154=makeQuery(id+"F10.imprint","IMPRINT",FACE,{"disambiguationData":[TD([[makeQuery(id+"F10.imprint","IMPRINT",EDGE,{"derivedFrom":sQuery(id+"F10.wireOp",EDGE,"E41.14.12.0")}),1.0]])]});
            var Q155;
            Q155=makeQuery(id+"F10.imprint","IMPRINT",FACE,{"disambiguationData":[TD([[makeQuery(id+"F10.imprint","IMPRINT",EDGE,{"derivedFrom":sQuery(id+"F10.wireOp",EDGE,"E41.13.11.0")}),1.0]])]});
            var Q156;
            Q156=makeQuery(id+"F10.imprint","IMPRINT",FACE,{"disambiguationData":[TD([[makeQuery(id+"F10.imprint","IMPRINT",EDGE,{"derivedFrom":sQuery(id+"F10.wireOp",EDGE,"E41.21.3.0")}),1.0]])]});
            var Q157;
            Q157=makeQuery(id+"F10.imprint","IMPRINT",FACE,{"disambiguationData":[TD([[makeQuery(id+"F10.imprint","IMPRINT",EDGE,{"derivedFrom":sQuery(id+"F10.wireOp",EDGE,"E41.20.2.0")}),1.0]])]});
            var Q158;
            Q158=makeQuery(id+"F10.imprint","IMPRINT",FACE,{"disambiguationData":[TD([[makeQuery(id+"F10.imprint","IMPRINT",EDGE,{"derivedFrom":sQuery(id+"F10.wireOp",EDGE,"E41.19.1.0")}),1.0]])]});
            var Q159;
            Q159=makeQuery(id+"F10.imprint","IMPRINT",FACE,{"disambiguationData":[TD([[makeQuery(id+"F10.imprint","IMPRINT",EDGE,{"derivedFrom":sQuery(id+"F10.wireOp",EDGE,"E41.18.0.0")}),1.0]])]});
            var Q160;
            Q160=makeQuery(id+"F10.imprint","IMPRINT",FACE,{"disambiguationData":[TD([[makeQuery(id+"F10.imprint","IMPRINT",EDGE,{"derivedFrom":sQuery(id+"F10.wireOp",EDGE,"E41.24.6.0")}),1.0]])]});
            var Q161;
            Q161=makeQuery(id+"F10.imprint","IMPRINT",FACE,{"disambiguationData":[TD([[makeQuery(id+"F10.imprint","IMPRINT",EDGE,{"derivedFrom":sQuery(id+"F10.wireOp",EDGE,"E41.23.5.0")}),1.0]])]});
            var Q162;
            Q162=makeQuery(id+"F10.imprint","IMPRINT",FACE,{"disambiguationData":[TD([[makeQuery(id+"F10.imprint","IMPRINT",EDGE,{"derivedFrom":sQuery(id+"F10.wireOp",EDGE,"E41.22.4.0")}),1.0]])]});
            var Q163;
            Q163=makeQuery(id+"F10.imprint","IMPRINT",FACE,{"disambiguationData":[TD([[makeQuery(id+"F10.imprint","IMPRINT",EDGE,{"derivedFrom":sQuery(id+"F10.wireOp",EDGE,"E41.4.4.0")}),1.0]])]});
            var Q164;
            Q164=makeQuery(id+"F10.imprint","IMPRINT",FACE,{"disambiguationData":[TD([[makeQuery(id+"F10.imprint","IMPRINT",EDGE,{"derivedFrom":sQuery(id+"F10.wireOp",EDGE,"E41.3.3.0")}),1.0]])]});
            var Q165;
            Q165=makeQuery(id+"F10.imprint","IMPRINT",FACE,{"disambiguationData":[TD([[makeQuery(id+"F10.imprint","IMPRINT",EDGE,{"derivedFrom":sQuery(id+"F10.wireOp",EDGE,"E41.8.8.0")}),1.0]])]});
            var Q166;
            Q166=makeQuery(id+"F10.imprint","IMPRINT",FACE,{"disambiguationData":[TD([[makeQuery(id+"F10.imprint","IMPRINT",EDGE,{"derivedFrom":sQuery(id+"F10.wireOp",EDGE,"E41.7.7.0")}),1.0]])]});
            var Q167;
            Q167=makeQuery(id+"F10.imprint","IMPRINT",FACE,{"disambiguationData":[TD([[makeQuery(id+"F10.imprint","IMPRINT",EDGE,{"derivedFrom":sQuery(id+"F10.wireOp",EDGE,"E41.12.12.0")}),1.0]])]});
            var Q168;
            Q168=makeQuery(id+"F10.imprint","IMPRINT",FACE,{"disambiguationData":[TD([[makeQuery(id+"F10.imprint","IMPRINT",EDGE,{"derivedFrom":sQuery(id+"F10.wireOp",EDGE,"E41.9.9.0")}),1.0]])]});
            var Q169;
            Q169=makeQuery(id+"F10.imprint","IMPRINT",FACE,{"disambiguationData":[TD([[makeQuery(id+"F10.imprint","IMPRINT",EDGE,{"derivedFrom":sQuery(id+"F10.wireOp",EDGE,"E41.14.14.0")}),1.0]])]});
            var Q170;
            Q170=makeQuery(id+"F10.imprint","IMPRINT",FACE,{"disambiguationData":[TD([[makeQuery(id+"F10.imprint","IMPRINT",EDGE,{"derivedFrom":sQuery(id+"F10.wireOp",EDGE,"E41.13.13.0")}),1.0]])]});
            var Q171;
            Q171=makeQuery(id+"F10.imprint","IMPRINT",FACE,{"disambiguationData":[TD([[makeQuery(id+"F10.imprint","IMPRINT",EDGE,{"derivedFrom":sQuery(id+"F10.wireOp",EDGE,"E41.20.4.0")}),1.0]])]});
            var Q172;
            Q172=makeQuery(id+"F10.imprint","IMPRINT",FACE,{"disambiguationData":[TD([[makeQuery(id+"F10.imprint","IMPRINT",EDGE,{"derivedFrom":sQuery(id+"F10.wireOp",EDGE,"E41.19.3.0")}),1.0]])]});
            var Q173;
            Q173=makeQuery(id+"F10.imprint","IMPRINT",FACE,{"disambiguationData":[TD([[makeQuery(id+"F10.imprint","IMPRINT",EDGE,{"derivedFrom":sQuery(id+"F10.wireOp",EDGE,"E41.18.2.0")}),1.0]])]});
            var Q174;
            Q174=makeQuery(id+"F10.imprint","IMPRINT",FACE,{"disambiguationData":[TD([[makeQuery(id+"F10.imprint","IMPRINT",EDGE,{"derivedFrom":sQuery(id+"F10.wireOp",EDGE,"E41.23.7.0")}),1.0]])]});
            var Q175;
            Q175=makeQuery(id+"F10.imprint","IMPRINT",FACE,{"disambiguationData":[TD([[makeQuery(id+"F10.imprint","IMPRINT",EDGE,{"derivedFrom":sQuery(id+"F10.wireOp",EDGE,"E41.24.8.0")}),1.0]])]});
            var Q176;
            Q176=makeQuery(id+"F10.imprint","IMPRINT",FACE,{"disambiguationData":[TD([[makeQuery(id+"F10.imprint","IMPRINT",EDGE,{"derivedFrom":sQuery(id+"F10.wireOp",EDGE,"E41.13.1.0")}),1.0]])]});
            var Q177;
            Q177=makeQuery(id+"F10.imprint","IMPRINT",FACE,{"disambiguationData":[TD([[makeQuery(id+"F10.imprint","IMPRINT",EDGE,{"derivedFrom":sQuery(id+"F10.wireOp",EDGE,"E41.4.5.0")}),1.0]])]});
            var Q178;
            Q178=makeQuery(id+"F10.imprint","IMPRINT",FACE,{"disambiguationData":[TD([[makeQuery(id+"F10.imprint","IMPRINT",EDGE,{"derivedFrom":sQuery(id+"F10.wireOp",EDGE,"E41.3.4.0")}),1.0]])]});
            var Q179;
            Q179=makeQuery(id+"F10.imprint","IMPRINT",FACE,{"disambiguationData":[TD([[makeQuery(id+"F10.imprint","IMPRINT",EDGE,{"derivedFrom":sQuery(id+"F10.wireOp",EDGE,"E41.2.3.0")}),1.0]])]});
            var Q180;
            Q180=makeQuery(id+"F10.imprint","IMPRINT",FACE,{"disambiguationData":[TD([[makeQuery(id+"F10.imprint","IMPRINT",EDGE,{"derivedFrom":sQuery(id+"F10.wireOp",EDGE,"E41.9.13.0")}),1.0]])]});
            var Q181;
            Q181=makeQuery(id+"F10.imprint","IMPRINT",FACE,{"disambiguationData":[TD([[makeQuery(id+"F10.imprint","IMPRINT",EDGE,{"derivedFrom":sQuery(id+"F10.wireOp",EDGE,"E41.16.4.0")}),1.0]])]});
            var Q182;
            Q182=makeQuery(id+"F10.imprint","IMPRINT",FACE,{"disambiguationData":[TD([[makeQuery(id+"F10.imprint","IMPRINT",EDGE,{"derivedFrom":sQuery(id+"F10.wireOp",EDGE,"E41.15.3.0")}),1.0]])]});
            var Q183;
            Q183=makeQuery(id+"F10.imprint","IMPRINT",FACE,{"disambiguationData":[TD([[makeQuery(id+"F10.imprint","IMPRINT",EDGE,{"derivedFrom":sQuery(id+"F10.wireOp",EDGE,"E41.14.2.0")}),1.0]])]});
            var Q184;
            Q184=makeQuery(id+"F10.imprint","IMPRINT",FACE,{"disambiguationData":[TD([[makeQuery(id+"F10.imprint","IMPRINT",EDGE,{"derivedFrom":sQuery(id+"F10.wireOp",EDGE,"E41.20.8.0")}),1.0]])]});
            var Q185;
            Q185=makeQuery(id+"F10.imprint","IMPRINT",FACE,{"disambiguationData":[TD([[makeQuery(id+"F10.imprint","IMPRINT",EDGE,{"derivedFrom":sQuery(id+"F10.wireOp",EDGE,"E41.19.7.0")}),1.0]])]});
            var Q186;
            Q186=makeQuery(id+"F10.imprint","IMPRINT",FACE,{"disambiguationData":[TD([[makeQuery(id+"F10.imprint","IMPRINT",EDGE,{"derivedFrom":sQuery(id+"F10.wireOp",EDGE,"E41.18.6.0")}),1.0]])]});
            var Q187;
            Q187=makeQuery(id+"F10.imprint","IMPRINT",FACE,{"disambiguationData":[TD([[makeQuery(id+"F10.imprint","IMPRINT",EDGE,{"derivedFrom":sQuery(id+"F10.wireOp",EDGE,"E41.24.12.0")}),1.0]])]});
            var Q188;
            Q188=makeQuery(id+"F10.imprint","IMPRINT",FACE,{"disambiguationData":[TD([[makeQuery(id+"F10.imprint","IMPRINT",EDGE,{"derivedFrom":sQuery(id+"F10.wireOp",EDGE,"E41.23.11.0")}),1.0]])]});
            var Q189;
            Q189=makeQuery(id+"F10.imprint","IMPRINT",FACE,{"disambiguationData":[TD([[makeQuery(id+"F10.imprint","IMPRINT",EDGE,{"derivedFrom":sQuery(id+"F10.wireOp",EDGE,"E41.8.9.0")}),1.0]])]});
            var Q190;
            Q190=makeQuery(id+"F10.imprint","IMPRINT",FACE,{"disambiguationData":[TD([[makeQuery(id+"F10.imprint","IMPRINT",EDGE,{"derivedFrom":sQuery(id+"F10.wireOp",EDGE,"E41.7.8.0")}),1.0]])]});
            var Q191;
            Q191=makeQuery(id+"F10.imprint","IMPRINT",FACE,{"disambiguationData":[TD([[makeQuery(id+"F10.imprint","IMPRINT",EDGE,{"derivedFrom":sQuery(id+"F10.wireOp",EDGE,"E41.6.7.0")}),1.0]])]});
            var Q192;
            Q192=makeQuery(id+"F10.imprint","IMPRINT",FACE,{"disambiguationData":[TD([[makeQuery(id+"F10.imprint","IMPRINT",EDGE,{"derivedFrom":sQuery(id+"F10.wireOp",EDGE,"E41.12.13.0")}),1.0]])]});
            var Q193;
            Q193=makeQuery(id+"F10.imprint","IMPRINT",FACE,{"disambiguationData":[TD([[makeQuery(id+"F10.imprint","IMPRINT",EDGE,{"derivedFrom":sQuery(id+"F10.wireOp",EDGE,"E41.11.12.0")}),1.0]])]});
            var Q194;
            Q194=makeQuery(id+"F10.imprint","IMPRINT",FACE,{"disambiguationData":[TD([[makeQuery(id+"F10.imprint","IMPRINT",EDGE,{"derivedFrom":sQuery(id+"F10.wireOp",EDGE,"E41.9.10.0")}),1.0]])]});
            var Q195;
            Q195=makeQuery(id+"F10.imprint","IMPRINT",FACE,{"disambiguationData":[TD([[makeQuery(id+"F10.imprint","IMPRINT",EDGE,{"derivedFrom":sQuery(id+"F10.wireOp",EDGE,"E41.13.14.0")}),1.0]])]});
            var Q196;
            Q196=makeQuery(id+"F10.imprint","IMPRINT",FACE,{"disambiguationData":[TD([[makeQuery(id+"F10.imprint","IMPRINT",EDGE,{"derivedFrom":sQuery(id+"F10.wireOp",EDGE,"E41.19.4.0")}),1.0]])]});
            var Q197;
            Q197=makeQuery(id+"F10.imprint","IMPRINT",FACE,{"disambiguationData":[TD([[makeQuery(id+"F10.imprint","IMPRINT",EDGE,{"derivedFrom":sQuery(id+"F10.wireOp",EDGE,"E41.18.3.0")}),1.0]])]});
            var Q198;
            Q198=makeQuery(id+"F10.imprint","IMPRINT",FACE,{"disambiguationData":[TD([[makeQuery(id+"F10.imprint","IMPRINT",EDGE,{"derivedFrom":sQuery(id+"F10.wireOp",EDGE,"E41.24.9.0")}),1.0]])]});
            var Q199;
            Q199=makeQuery(id+"F10.imprint","IMPRINT",FACE,{"disambiguationData":[TD([[makeQuery(id+"F10.imprint","IMPRINT",EDGE,{"derivedFrom":sQuery(id+"F10.wireOp",EDGE,"E41.23.8.0")}),1.0]])]});
            var Q200;
            Q200=makeQuery(id+"F10.imprint","IMPRINT",FACE,{"disambiguationData":[TD([[makeQuery(id+"F10.imprint","IMPRINT",EDGE,{"derivedFrom":sQuery(id+"F10.wireOp",EDGE,"E41.22.7.0")}),1.0]])]});
            var Q201;
            Q201=makeQuery(id+"F10.imprint","IMPRINT",FACE,{"disambiguationData":[TD([[makeQuery(id+"F10.imprint","IMPRINT",EDGE,{"derivedFrom":sQuery(id+"F10.wireOp",EDGE,"E41.4.9.0")}),1.0]])]});
            var Q202;
            Q202=makeQuery(id+"F10.imprint","IMPRINT",FACE,{"disambiguationData":[TD([[makeQuery(id+"F10.imprint","IMPRINT",EDGE,{"derivedFrom":sQuery(id+"F10.wireOp",EDGE,"E41.3.8.0")}),1.0]])]});
            var Q203;
            Q203=makeQuery(id+"F10.imprint","IMPRINT",FACE,{"disambiguationData":[TD([[makeQuery(id+"F10.imprint","IMPRINT",EDGE,{"derivedFrom":sQuery(id+"F10.wireOp",EDGE,"E41.2.7.0")}),1.0]])]});
            var Q204;
            Q204=makeQuery(id+"F10.imprint","IMPRINT",FACE,{"disambiguationData":[TD([[makeQuery(id+"F10.imprint","IMPRINT",EDGE,{"derivedFrom":sQuery(id+"F10.wireOp",EDGE,"E41.8.13.0")}),1.0]])]});
            var Q205;
            Q205=makeQuery(id+"F10.imprint","IMPRINT",FACE,{"disambiguationData":[TD([[makeQuery(id+"F10.imprint","IMPRINT",EDGE,{"derivedFrom":sQuery(id+"F10.wireOp",EDGE,"E41.7.12.0")}),1.0]])]});
            var Q206;
            Q206=makeQuery(id+"F10.imprint","IMPRINT",FACE,{"disambiguationData":[TD([[makeQuery(id+"F10.imprint","IMPRINT",EDGE,{"derivedFrom":sQuery(id+"F10.wireOp",EDGE,"E41.13.2.0")}),1.0]])]});
            var Q207;
            Q207=makeQuery(id+"F10.imprint","IMPRINT",FACE,{"disambiguationData":[TD([[makeQuery(id+"F10.imprint","IMPRINT",EDGE,{"derivedFrom":sQuery(id+"F10.wireOp",EDGE,"E41.9.14.0")}),1.0]])]});
            var Q208;
            Q208=makeQuery(id+"F10.imprint","IMPRINT",FACE,{"disambiguationData":[TD([[makeQuery(id+"F10.imprint","IMPRINT",EDGE,{"derivedFrom":sQuery(id+"F10.wireOp",EDGE,"E41.15.4.0")}),1.0]])]});
            var Q209;
            Q209=makeQuery(id+"F10.imprint","IMPRINT",FACE,{"disambiguationData":[TD([[makeQuery(id+"F10.imprint","IMPRINT",EDGE,{"derivedFrom":sQuery(id+"F10.wireOp",EDGE,"E41.14.3.0")}),1.0]])]});
            var Q210;
            Q210=makeQuery(id+"F10.imprint","IMPRINT",FACE,{"disambiguationData":[TD([[makeQuery(id+"F10.imprint","IMPRINT",EDGE,{"derivedFrom":sQuery(id+"F10.wireOp",EDGE,"E41.19.8.0")}),1.0]])]});
            var Q211;
            Q211=makeQuery(id+"F10.imprint","IMPRINT",FACE,{"disambiguationData":[TD([[makeQuery(id+"F10.imprint","IMPRINT",EDGE,{"derivedFrom":sQuery(id+"F10.wireOp",EDGE,"E41.18.7.0")}),1.0]])]});
            var Q212;
            Q212=makeQuery(id+"F10.imprint","IMPRINT",FACE,{"disambiguationData":[TD([[makeQuery(id+"F10.imprint","IMPRINT",EDGE,{"derivedFrom":sQuery(id+"F10.wireOp",EDGE,"E41.24.13.0")}),1.0]])]});
            var Q213;
            Q213=makeQuery(id+"F10.imprint","IMPRINT",FACE,{"disambiguationData":[TD([[makeQuery(id+"F10.imprint","IMPRINT",EDGE,{"derivedFrom":sQuery(id+"F10.wireOp",EDGE,"E41.23.12.0")}),1.0]])]});
            var Q214;
            Q214=makeQuery(id+"F10.imprint","IMPRINT",FACE,{"disambiguationData":[TD([[makeQuery(id+"F10.imprint","IMPRINT",EDGE,{"derivedFrom":sQuery(id+"F10.wireOp",EDGE,"E41.2.8.0")}),1.0]])]});
            var Q215;
            Q215=makeQuery(id+"F10.imprint","IMPRINT",FACE,{"disambiguationData":[TD([[makeQuery(id+"F10.imprint","IMPRINT",EDGE,{"derivedFrom":sQuery(id+"F10.wireOp",EDGE,"E41.1.7.0")}),1.0]])]});
            var Q216;
            Q216=makeQuery(id+"F10.imprint","IMPRINT",FACE,{"disambiguationData":[TD([[makeQuery(id+"F10.imprint","IMPRINT",EDGE,{"derivedFrom":sQuery(id+"F10.wireOp",EDGE,"E41.6.12.0")}),1.0]])]});
            var Q217;
            Q217=makeQuery(id+"F10.imprint","IMPRINT",FACE,{"disambiguationData":[TD([[makeQuery(id+"F10.imprint","IMPRINT",EDGE,{"derivedFrom":sQuery(id+"F10.wireOp",EDGE,"E41.4.10.0")}),1.0]])]});
            var Q218;
            Q218=makeQuery(id+"F10.imprint","IMPRINT",FACE,{"disambiguationData":[TD([[makeQuery(id+"F10.imprint","IMPRINT",EDGE,{"derivedFrom":sQuery(id+"F10.wireOp",EDGE,"E41.3.9.0")}),1.0]])]});
            var Q219;
            Q219=makeQuery(id+"F10.imprint","IMPRINT",FACE,{"disambiguationData":[TD([[makeQuery(id+"F10.imprint","IMPRINT",EDGE,{"derivedFrom":sQuery(id+"F10.wireOp",EDGE,"E41.8.14.0")}),1.0]])]});
            var Q220;
            Q220=makeQuery(id+"F10.imprint","IMPRINT",FACE,{"disambiguationData":[TD([[makeQuery(id+"F10.imprint","IMPRINT",EDGE,{"derivedFrom":sQuery(id+"F10.wireOp",EDGE,"E41.7.13.0")}),1.0]])]});
            var Q221;
            Q221=makeQuery(id+"F10.imprint","IMPRINT",FACE,{"disambiguationData":[TD([[makeQuery(id+"F10.imprint","IMPRINT",EDGE,{"derivedFrom":sQuery(id+"F10.wireOp",EDGE,"E41.14.4.0")}),1.0]])]});
            var Q222;
            Q222=makeQuery(id+"F10.imprint","IMPRINT",FACE,{"disambiguationData":[TD([[makeQuery(id+"F10.imprint","IMPRINT",EDGE,{"derivedFrom":sQuery(id+"F10.wireOp",EDGE,"E41.13.3.0")}),1.0]])]});
            var Q223;
            Q223=makeQuery(id+"F10.imprint","IMPRINT",FACE,{"disambiguationData":[TD([[makeQuery(id+"F10.imprint","IMPRINT",EDGE,{"derivedFrom":sQuery(id+"F10.wireOp",EDGE,"E41.19.9.0")}),1.0]])]});
            var Q224;
            Q224=makeQuery(id+"F10.imprint","IMPRINT",FACE,{"disambiguationData":[TD([[makeQuery(id+"F10.imprint","IMPRINT",EDGE,{"derivedFrom":sQuery(id+"F10.wireOp",EDGE,"E41.18.8.0")}),1.0]])]});
            var Q225;
            Q225=makeQuery(id+"F10.imprint","IMPRINT",FACE,{"disambiguationData":[TD([[makeQuery(id+"F10.imprint","IMPRINT",EDGE,{"derivedFrom":sQuery(id+"F10.wireOp",EDGE,"E41.17.7.0")}),1.0]])]});
            var Q226;
            Q226=makeQuery(id+"F10.imprint","IMPRINT",FACE,{"disambiguationData":[TD([[makeQuery(id+"F10.imprint","IMPRINT",EDGE,{"derivedFrom":sQuery(id+"F10.wireOp",EDGE,"E41.23.13.0")}),1.0]])]});
            var Q227;
            Q227=makeQuery(id+"F10.imprint","IMPRINT",FACE,{"disambiguationData":[TD([[makeQuery(id+"F10.imprint","IMPRINT",EDGE,{"derivedFrom":sQuery(id+"F10.wireOp",EDGE,"E41.22.12.0")}),1.0]])]});
            var Q228;
            Q228=makeQuery(id+"F10.imprint","IMPRINT",FACE,{"disambiguationData":[TD([[makeQuery(id+"F10.imprint","IMPRINT",EDGE,{"derivedFrom":sQuery(id+"F10.wireOp",EDGE,"E41.24.14.0")}),1.0]])]});
            var Q229;
            Q229=makeQuery(id+"F10.imprint","IMPRINT",FACE,{"disambiguationData":[TD([[makeQuery(id+"F10.imprint","IMPRINT",EDGE,{"derivedFrom":sQuery(id+"F10.wireOp",EDGE,"E41.6.13.0")}),1.0]])]});
            var Q230;
            Q230=makeQuery(id+"F10.imprint","IMPRINT",FACE,{"disambiguationData":[TD([[makeQuery(id+"F10.imprint","IMPRINT",EDGE,{"derivedFrom":sQuery(id+"F10.wireOp",EDGE,"E41.1.8.0")}),1.0]])]});
            var Q231;
            Q231=makeQuery(id+"F10.imprint","IMPRINT",FACE,{"disambiguationData":[TD([[makeQuery(id+"F10.imprint","IMPRINT",EDGE,{"derivedFrom":sQuery(id+"F10.wireOp",EDGE,"E41.5.12.0")}),1.0]])]});
            var Q232;
            Q232=makeQuery(id+"F10.imprint","IMPRINT",FACE,{"disambiguationData":[TD([[makeQuery(id+"F10.imprint","IMPRINT",EDGE,{"derivedFrom":sQuery(id+"F10.wireOp",EDGE,"E41.4.11.0")}),1.0]])]});
            var Q233;
            Q233=makeQuery(id+"F10.imprint","IMPRINT",FACE,{"disambiguationData":[TD([[makeQuery(id+"F10.imprint","IMPRINT",EDGE,{"derivedFrom":sQuery(id+"F10.wireOp",EDGE,"E41.3.10.0")}),1.0]])]});
            var Q234;
            Q234=makeQuery(id+"F10.imprint","IMPRINT",FACE,{"disambiguationData":[TD([[makeQuery(id+"F10.imprint","IMPRINT",EDGE,{"derivedFrom":sQuery(id+"F10.wireOp",EDGE,"E41.9.0.0")}),1.0]])]});
            var Q235;
            Q235=makeQuery(id+"F10.imprint","IMPRINT",FACE,{"disambiguationData":[TD([[makeQuery(id+"F10.imprint","IMPRINT",EDGE,{"derivedFrom":sQuery(id+"F10.wireOp",EDGE,"E41.14.5.0")}),1.0]])]});
            var Q236;
            Q236=makeQuery(id+"F10.imprint","IMPRINT",FACE,{"disambiguationData":[TD([[makeQuery(id+"F10.imprint","IMPRINT",EDGE,{"derivedFrom":sQuery(id+"F10.wireOp",EDGE,"E41.13.4.0")}),1.0]])]});
            var Q237;
            Q237=makeQuery(id+"F10.imprint","IMPRINT",FACE,{"disambiguationData":[TD([[makeQuery(id+"F10.imprint","IMPRINT",EDGE,{"derivedFrom":sQuery(id+"F10.wireOp",EDGE,"E41.19.10.0")}),1.0]])]});
            var Q238;
            Q238=makeQuery(id+"F10.imprint","IMPRINT",FACE,{"disambiguationData":[TD([[makeQuery(id+"F10.imprint","IMPRINT",EDGE,{"derivedFrom":sQuery(id+"F10.wireOp",EDGE,"E41.12.3.0")}),1.0]])]});
            var Q239;
            Q239=makeQuery(id+"F10.imprint","IMPRINT",FACE,{"disambiguationData":[TD([[makeQuery(id+"F10.imprint","IMPRINT",EDGE,{"derivedFrom":sQuery(id+"F10.wireOp",EDGE,"E41.18.9.0")}),1.0]])]});
            var Q240;
            Q240=makeQuery(id+"F10.imprint","IMPRINT",FACE,{"disambiguationData":[TD([[makeQuery(id+"F10.imprint","IMPRINT",EDGE,{"derivedFrom":sQuery(id+"F10.wireOp",EDGE,"E41.17.8.0")}),1.0]])]});
            var Q241;
            Q241=makeQuery(id+"F10.imprint","IMPRINT",FACE,{"disambiguationData":[TD([[makeQuery(id+"F10.imprint","IMPRINT",EDGE,{"derivedFrom":sQuery(id+"F10.wireOp",EDGE,"E41.16.7.0")}),1.0]])]});
            var Q242;
            Q242=makeQuery(id+"F10.imprint","IMPRINT",FACE,{"disambiguationData":[TD([[makeQuery(id+"F10.imprint","IMPRINT",EDGE,{"derivedFrom":sQuery(id+"F10.wireOp",EDGE,"E41.23.14.0")}),1.0]])]});
            var Q243;
            Q243=makeQuery(id+"F10.imprint","IMPRINT",FACE,{"disambiguationData":[TD([[makeQuery(id+"F10.imprint","IMPRINT",EDGE,{"derivedFrom":sQuery(id+"F10.wireOp",EDGE,"E41.22.13.0")}),1.0]])]});
            var Q244;
            Q244=makeQuery(id+"F10.imprint","IMPRINT",FACE,{"disambiguationData":[TD([[makeQuery(id+"F10.imprint","IMPRINT",EDGE,{"derivedFrom":sQuery(id+"F10.wireOp",EDGE,"E41.21.12.0")}),1.0]])]});
            var Q245;
            Q245=makeQuery(id+"F10.imprint","IMPRINT",FACE,{"disambiguationData":[TD([[makeQuery(id+"F10.imprint","IMPRINT",EDGE,{"derivedFrom":sQuery(id+"F10.wireOp",EDGE,"E41.2.10.0")}),1.0]])]});
            var Q246;
            Q246=makeQuery(id+"F10.imprint","IMPRINT",FACE,{"disambiguationData":[TD([[makeQuery(id+"F10.imprint","IMPRINT",EDGE,{"derivedFrom":sQuery(id+"F10.wireOp",EDGE,"E41.1.9.0")}),1.0]])]});
            var Q247;
            Q247=makeQuery(id+"F10.imprint","IMPRINT",FACE,{"disambiguationData":[TD([[makeQuery(id+"F10.imprint","IMPRINT",EDGE,{"derivedFrom":sQuery(id+"F10.wireOp",EDGE,"E41.6.14.0")}),1.0]])]});
            var Q248;
            Q248=makeQuery(id+"F10.imprint","IMPRINT",FACE,{"disambiguationData":[TD([[makeQuery(id+"F10.imprint","IMPRINT",EDGE,{"derivedFrom":sQuery(id+"F10.wireOp",EDGE,"E41.17.9.0")}),1.0]])]});
            var Q249;
            Q249=makeQuery(id+"F10.imprint","IMPRINT",FACE,{"disambiguationData":[TD([[makeQuery(id+"F10.imprint","IMPRINT",EDGE,{"derivedFrom":sQuery(id+"F10.wireOp",EDGE,"E41.22.14.0")}),1.0]])]});
            var Q250;
            Q250=makeQuery(id+"F10.imprint","IMPRINT",FACE,{"disambiguationData":[TD([[makeQuery(id+"F10.imprint","IMPRINT",EDGE,{"derivedFrom":sQuery(id+"F10.wireOp",EDGE,"E41.1.0.0")}),1.0]])]});
            var Q251;
            Q251=makeQuery(id+"F10.imprint","IMPRINT",FACE,{"disambiguationData":[TD([[makeQuery(id+"F10.imprint","IMPRINT",EDGE,{"derivedFrom":sQuery(id+"F10.wireOp",EDGE,"E41.0.14.0")}),1.0]])]});
            var Q252;
            Q252=makeQuery(id+"F10.imprint","IMPRINT",FACE,{"disambiguationData":[TD([[makeQuery(id+"F10.imprint","IMPRINT",EDGE,{"derivedFrom":sQuery(id+"F10.wireOp",EDGE,"E40")}),1.0]])]});
            var Q253;
            Q253=makeQuery(id+"F10.imprint","IMPRINT",FACE,{"disambiguationData":[TD([[makeQuery(id+"F10.imprint","IMPRINT",EDGE,{"derivedFrom":sQuery(id+"F10.wireOp",EDGE,"E41.0.1.0")}),1.0]])]});
            var Q254;
            Q254=makeQuery(id+"F10.imprint","IMPRINT",FACE,{"disambiguationData":[TD([[makeQuery(id+"F10.imprint","IMPRINT",EDGE,{"derivedFrom":sQuery(id+"F10.wireOp",EDGE,"E41.0.5.0")}),1.0]])]});
            var Q255;
            Q255=makeQuery(id+"F10.imprint","IMPRINT",FACE,{"disambiguationData":[TD([[makeQuery(id+"F10.imprint","IMPRINT",EDGE,{"derivedFrom":sQuery(id+"F10.wireOp",EDGE,"E41.0.6.0")}),1.0]])]});
            var Q256;
            Q256=makeQuery(id+"F10.imprint","IMPRINT",FACE,{"disambiguationData":[TD([[makeQuery(id+"F10.imprint","IMPRINT",EDGE,{"derivedFrom":sQuery(id+"F10.wireOp",EDGE,"E41.0.9.0")}),1.0]])]});
            var Q257;
            Q257=makeQuery(id+"F10.imprint","IMPRINT",FACE,{"disambiguationData":[TD([[makeQuery(id+"F10.imprint","IMPRINT",EDGE,{"derivedFrom":sQuery(id+"F10.wireOp",EDGE,"E41.0.10.0")}),1.0]])]});
            var Q258;
            Q258=makeQuery(id+"F10.imprint","IMPRINT",FACE,{"disambiguationData":[TD([[makeQuery(id+"F10.imprint","IMPRINT",EDGE,{"derivedFrom":sQuery(id+"F10.wireOp",EDGE,"E41.0.11.0")}),1.0]])]});
            var Q259;
            Q259=makeQuery(id+"F10.imprint","IMPRINT",FACE,{"disambiguationData":[TD([[makeQuery(id+"F10.imprint","IMPRINT",EDGE,{"derivedFrom":sQuery(id+"F10.wireOp",EDGE,"E41.7.0.0")}),1.0]])]});
            var Q260;
            Q260=makeQuery(id+"F10.imprint","IMPRINT",FACE,{"disambiguationData":[TD([[makeQuery(id+"F10.imprint","IMPRINT",EDGE,{"derivedFrom":sQuery(id+"F10.wireOp",EDGE,"E41.5.14.0")}),1.0]])]});
            var Q261;
            Q261=makeQuery(id+"F10.imprint","IMPRINT",FACE,{"disambiguationData":[TD([[makeQuery(id+"F10.imprint","IMPRINT",EDGE,{"derivedFrom":sQuery(id+"F10.wireOp",EDGE,"E41.12.5.0")}),1.0]])]});
            var Q262;
            Q262=makeQuery(id+"F10.imprint","IMPRINT",FACE,{"disambiguationData":[TD([[makeQuery(id+"F10.imprint","IMPRINT",EDGE,{"derivedFrom":sQuery(id+"F10.wireOp",EDGE,"E41.17.10.0")}),1.0]])]});
            var Q263;
            Q263=makeQuery(id+"F10.imprint","IMPRINT",FACE,{"disambiguationData":[TD([[makeQuery(id+"F10.imprint","IMPRINT",EDGE,{"derivedFrom":sQuery(id+"F10.wireOp",EDGE,"E41.16.9.0")}),1.0]])]});
            var Q264;
            Q264=makeQuery(id+"F10.imprint","IMPRINT",FACE,{"disambiguationData":[TD([[makeQuery(id+"F10.imprint","IMPRINT",EDGE,{"derivedFrom":sQuery(id+"F10.wireOp",EDGE,"E41.21.14.0")}),1.0]])]});
            var Q265;
            Q265=makeQuery(id+"F10.imprint","IMPRINT",FACE,{"disambiguationData":[TD([[makeQuery(id+"F10.imprint","IMPRINT",EDGE,{"derivedFrom":sQuery(id+"F10.wireOp",EDGE,"E41.1.10.0")}),1.0]])]});
            var Q266;
            Q266=makeQuery(id+"F10.imprint","IMPRINT",FACE,{"disambiguationData":[TD([[makeQuery(id+"F10.imprint","IMPRINT",EDGE,{"derivedFrom":sQuery(id+"F10.wireOp",EDGE,"E41.2.11.0")}),1.0]])]});
            var Q267;
            Q267=makeQuery(id+"F10.imprint","IMPRINT",FACE,{"disambiguationData":[TD([[makeQuery(id+"F10.imprint","IMPRINT",EDGE,{"derivedFrom":sQuery(id+"F10.wireOp",EDGE,"E41.11.5.0")}),1.0]])]});
            var Q268;
            Q268=makeQuery(id+"F10.imprint","IMPRINT",FACE,{"disambiguationData":[TD([[makeQuery(id+"F10.imprint","IMPRINT",EDGE,{"derivedFrom":sQuery(id+"F10.wireOp",EDGE,"E41.15.9.0")}),1.0]])]});
            var Q269;
            Q269=makeQuery(id+"F10.imprint","IMPRINT",FACE,{"disambiguationData":[TD([[makeQuery(id+"F10.imprint","IMPRINT",EDGE,{"derivedFrom":sQuery(id+"F10.wireOp",EDGE,"E41.12.6.0")}),1.0]])]});
            var Q270;
            Q270=makeQuery(id+"F10.imprint","IMPRINT",FACE,{"disambiguationData":[TD([[makeQuery(id+"F10.imprint","IMPRINT",EDGE,{"derivedFrom":sQuery(id+"F10.wireOp",EDGE,"E41.17.11.0")}),1.0]])]});
            var Q271;
            Q271=makeQuery(id+"F10.imprint","IMPRINT",FACE,{"disambiguationData":[TD([[makeQuery(id+"F10.imprint","IMPRINT",EDGE,{"derivedFrom":sQuery(id+"F10.wireOp",EDGE,"E41.16.10.0")}),1.0]])]});
            var Q272;
            Q272=makeQuery(id+"F10.imprint","IMPRINT",FACE,{"disambiguationData":[TD([[makeQuery(id+"F10.imprint","IMPRINT",EDGE,{"derivedFrom":sQuery(id+"F10.wireOp",EDGE,"E41.22.0.0")}),1.0]])]});
            var Q273;
            Q273=makeQuery(id+"F10.imprint","IMPRINT",FACE,{"disambiguationData":[TD([[makeQuery(id+"F10.imprint","IMPRINT",EDGE,{"derivedFrom":sQuery(id+"F10.wireOp",EDGE,"E41.20.14.0")}),1.0]])]});
            var Q274;
            Q274=makeQuery(id+"F10.imprint","IMPRINT",FACE,{"disambiguationData":[TD([[makeQuery(id+"F10.imprint","IMPRINT",EDGE,{"derivedFrom":sQuery(id+"F10.wireOp",EDGE,"E41.1.11.0")}),1.0]])]});
            var Q275;
            Q275=makeQuery(id+"F10.imprint","IMPRINT",FACE,{"disambiguationData":[TD([[makeQuery(id+"F10.imprint","IMPRINT",EDGE,{"derivedFrom":sQuery(id+"F10.wireOp",EDGE,"E41.7.1.0")}),1.0]])]});
            var Q276;
            Q276=makeQuery(id+"F10.imprint","IMPRINT",FACE,{"disambiguationData":[TD([[makeQuery(id+"F10.imprint","IMPRINT",EDGE,{"derivedFrom":sQuery(id+"F10.wireOp",EDGE,"E41.6.0.0")}),1.0]])]});
            var Q277;
            Q277=makeQuery(id+"F10.imprint","IMPRINT",FACE,{"disambiguationData":[TD([[makeQuery(id+"F10.imprint","IMPRINT",EDGE,{"derivedFrom":sQuery(id+"F10.wireOp",EDGE,"E41.15.10.0")}),1.0]])]});
            var Q278;
            Q278=makeQuery(id+"F10.imprint","IMPRINT",FACE,{"disambiguationData":[TD([[makeQuery(id+"F10.imprint","IMPRINT",EDGE,{"derivedFrom":sQuery(id+"F10.wireOp",EDGE,"E41.16.11.0")}),1.0]])]});
            var Q279;
            Q279=makeQuery(id+"F10.imprint","IMPRINT",FACE,{"disambiguationData":[TD([[makeQuery(id+"F10.imprint","IMPRINT",EDGE,{"derivedFrom":sQuery(id+"F10.wireOp",EDGE,"E41.22.1.0")}),1.0]])]});
            var Q280;
            Q280=makeQuery(id+"F10.imprint","IMPRINT",FACE,{"disambiguationData":[TD([[makeQuery(id+"F10.imprint","IMPRINT",EDGE,{"derivedFrom":sQuery(id+"F10.wireOp",EDGE,"E41.21.0.0")}),1.0]])]});
            var Q281;
            Q281=makeQuery(id+"F10.imprint","IMPRINT",FACE,{"disambiguationData":[TD([[makeQuery(id+"F10.imprint","IMPRINT",EDGE,{"derivedFrom":sQuery(id+"F10.wireOp",EDGE,"E41.7.2.0")}),1.0]])]});
            var Q282;
            Q282=makeQuery(id+"F10.imprint","IMPRINT",FACE,{"disambiguationData":[TD([[makeQuery(id+"F10.imprint","IMPRINT",EDGE,{"derivedFrom":sQuery(id+"F10.wireOp",EDGE,"E41.6.1.0")}),1.0]])]});
            var Q283;
            Q283=makeQuery(id+"F10.imprint","IMPRINT",FACE,{"disambiguationData":[TD([[makeQuery(id+"F10.imprint","IMPRINT",EDGE,{"derivedFrom":sQuery(id+"F10.wireOp",EDGE,"E41.5.0.0")}),1.0]])]});
            var Q284;
            Q284=makeQuery(id+"F10.imprint","IMPRINT",FACE,{"disambiguationData":[TD([[makeQuery(id+"F10.imprint","IMPRINT",EDGE,{"derivedFrom":sQuery(id+"F10.wireOp",EDGE,"E41.11.6.0")}),1.0]])]});
            var Q285;
            Q285=makeQuery(id+"F10.imprint","IMPRINT",FACE,{"disambiguationData":[TD([[makeQuery(id+"F10.imprint","IMPRINT",EDGE,{"derivedFrom":sQuery(id+"F10.wireOp",EDGE,"E41.10.5.0")}),1.0]])]});
            var Q286;
            Q286=makeQuery(id+"F10.imprint","IMPRINT",FACE,{"disambiguationData":[TD([[makeQuery(id+"F10.imprint","IMPRINT",EDGE,{"derivedFrom":sQuery(id+"F10.wireOp",EDGE,"E41.20.0.0")}),1.0]])]});
            var Q287;
            Q287=makeQuery(id+"F10.imprint","IMPRINT",FACE,{"disambiguationData":[TD([[makeQuery(id+"F10.imprint","IMPRINT",EDGE,{"derivedFrom":sQuery(id+"F10.wireOp",EDGE,"E41.22.2.0")}),1.0]])]});
            var Q288;
            Q288=makeQuery(id+"F10.imprint","IMPRINT",FACE,{"disambiguationData":[TD([[makeQuery(id+"F10.imprint","IMPRINT",EDGE,{"derivedFrom":sQuery(id+"F10.wireOp",EDGE,"E41.21.1.0")}),1.0]])]});
            var Q289;
            Q289=makeQuery(id+"F10.imprint","IMPRINT",FACE,{"disambiguationData":[TD([[makeQuery(id+"F10.imprint","IMPRINT",EDGE,{"derivedFrom":sQuery(id+"F10.wireOp",EDGE,"E41.2.14.0")}),1.0]])]});
            var Q290;
            Q290=makeQuery(id+"F10.imprint","IMPRINT",FACE,{"disambiguationData":[TD([[makeQuery(id+"F10.imprint","IMPRINT",EDGE,{"derivedFrom":sQuery(id+"F10.wireOp",EDGE,"E41.6.2.0")}),1.0]])]});
            var Q291;
            Q291=makeQuery(id+"F10.imprint","IMPRINT",FACE,{"disambiguationData":[TD([[makeQuery(id+"F10.imprint","IMPRINT",EDGE,{"derivedFrom":sQuery(id+"F10.wireOp",EDGE,"E41.5.1.0")}),1.0]])]});
            var Q292;
            Q292=makeQuery(id+"F10.imprint","IMPRINT",FACE,{"disambiguationData":[TD([[makeQuery(id+"F10.imprint","IMPRINT",EDGE,{"derivedFrom":sQuery(id+"F10.wireOp",EDGE,"E41.10.6.0")}),1.0]])]});
            var Q293;
            Q293=makeQuery(id+"F10.imprint","IMPRINT",FACE,{"disambiguationData":[TD([[makeQuery(id+"F10.imprint","IMPRINT",EDGE,{"derivedFrom":sQuery(id+"F10.wireOp",EDGE,"E41.15.11.0")}),1.0]])]});
            var Q294;
            Q294=makeQuery(id+"F10.imprint","IMPRINT",FACE,{"disambiguationData":[TD([[makeQuery(id+"F10.imprint","IMPRINT",EDGE,{"derivedFrom":sQuery(id+"F10.wireOp",EDGE,"E41.7.9.0")}),1.0]])]});
            var Q295;
            Q295=makeQuery(id+"F10.imprint","IMPRINT",FACE,{"disambiguationData":[TD([[makeQuery(id+"F10.imprint","IMPRINT",EDGE,{"derivedFrom":sQuery(id+"F10.wireOp",EDGE,"E41.12.14.0")}),1.0]])]});
            var Q296;
            Q296=makeQuery(id+"F10.imprint","IMPRINT",FACE,{"disambiguationData":[TD([[makeQuery(id+"F10.imprint","IMPRINT",EDGE,{"derivedFrom":sQuery(id+"F10.wireOp",EDGE,"E41.16.2.0")}),1.0]])]});
            var Q297;
            Q297=makeQuery(id+"F10.imprint","IMPRINT",FACE,{"disambiguationData":[TD([[makeQuery(id+"F10.imprint","IMPRINT",EDGE,{"derivedFrom":sQuery(id+"F10.wireOp",EDGE,"E41.15.1.0")}),1.0]])]});
            var Q298;
            Q298=makeQuery(id+"F10.imprint","IMPRINT",FACE,{"disambiguationData":[TD([[makeQuery(id+"F10.imprint","IMPRINT",EDGE,{"derivedFrom":sQuery(id+"F10.wireOp",EDGE,"E41.20.6.0")}),1.0]])]});
            var Q299;
            Q299=makeQuery(id+"F10.imprint","IMPRINT",FACE,{"disambiguationData":[TD([[makeQuery(id+"F10.imprint","IMPRINT",EDGE,{"derivedFrom":sQuery(id+"F10.wireOp",EDGE,"E41.2.5.0")}),1.0]])]});
            var Q300;
            Q300=makeQuery(id+"F10.imprint","IMPRINT",FACE,{"disambiguationData":[TD([[makeQuery(id+"F10.imprint","IMPRINT",EDGE,{"derivedFrom":sQuery(id+"F10.wireOp",EDGE,"E41.2.1.0")}),1.0]])]});
            var Q301;
            Q301=makeQuery(id+"F10.imprint","IMPRINT",FACE,{"disambiguationData":[TD([[makeQuery(id+"F10.imprint","IMPRINT",EDGE,{"derivedFrom":sQuery(id+"F10.wireOp",EDGE,"E41.7.6.0")}),1.0]])]});
            var Q302;
            Q302=makeQuery(id+"F10.imprint","IMPRINT",FACE,{"disambiguationData":[TD([[makeQuery(id+"F10.imprint","IMPRINT",EDGE,{"derivedFrom":sQuery(id+"F10.wireOp",EDGE,"E41.6.5.0")}),1.0]])]});
            var Q303;
            Q303=makeQuery(id+"F10.imprint","IMPRINT",FACE,{"disambiguationData":[TD([[makeQuery(id+"F10.imprint","IMPRINT",EDGE,{"derivedFrom":sQuery(id+"F10.wireOp",EDGE,"E41.12.11.0")}),1.0]])]});
            var Q304;
            Q304=makeQuery(id+"F10.imprint","IMPRINT",FACE,{"disambiguationData":[TD([[makeQuery(id+"F10.imprint","IMPRINT",EDGE,{"derivedFrom":sQuery(id+"F10.wireOp",EDGE,"E41.11.10.0")}),1.0]])]});
            var Q305;
            Q305=makeQuery(id+"F10.imprint","IMPRINT",FACE,{"disambiguationData":[TD([[makeQuery(id+"F10.imprint","IMPRINT",EDGE,{"derivedFrom":sQuery(id+"F10.wireOp",EDGE,"E41.10.9.0")}),1.0]])]});
            var Q306;
            Q306=makeQuery(id+"F10.imprint","IMPRINT",FACE,{"disambiguationData":[TD([[makeQuery(id+"F10.imprint","IMPRINT",EDGE,{"derivedFrom":sQuery(id+"F10.wireOp",EDGE,"E41.17.0.0")}),1.0]])]});
            var Q307;
            Q307=makeQuery(id+"F10.imprint","IMPRINT",FACE,{"disambiguationData":[TD([[makeQuery(id+"F10.imprint","IMPRINT",EDGE,{"derivedFrom":sQuery(id+"F10.wireOp",EDGE,"E41.15.14.0")}),1.0]])]});
            var Q308;
            Q308=makeQuery(id+"F10.imprint","IMPRINT",FACE,{"disambiguationData":[TD([[makeQuery(id+"F10.imprint","IMPRINT",EDGE,{"derivedFrom":sQuery(id+"F10.wireOp",EDGE,"E41.22.5.0")}),1.0]])]});
            var Q309;
            Q309=makeQuery(id+"F10.imprint","IMPRINT",FACE,{"disambiguationData":[TD([[makeQuery(id+"F10.imprint","IMPRINT",EDGE,{"derivedFrom":sQuery(id+"F10.wireOp",EDGE,"E41.7.10.0")}),1.0]])]});
            var Q310;
            Q310=makeQuery(id+"F10.imprint","IMPRINT",FACE,{"disambiguationData":[TD([[makeQuery(id+"F10.imprint","IMPRINT",EDGE,{"derivedFrom":sQuery(id+"F10.wireOp",EDGE,"E41.6.9.0")}),1.0]])]});
            var Q311;
            Q311=makeQuery(id+"F10.imprint","IMPRINT",FACE,{"disambiguationData":[TD([[makeQuery(id+"F10.imprint","IMPRINT",EDGE,{"derivedFrom":sQuery(id+"F10.wireOp",EDGE,"E41.11.14.0")}),1.0]])]});
            var Q312;
            Q312=makeQuery(id+"F10.imprint","IMPRINT",FACE,{"disambiguationData":[TD([[makeQuery(id+"F10.imprint","IMPRINT",EDGE,{"derivedFrom":sQuery(id+"F10.wireOp",EDGE,"E41.1.14.0")}),1.0]])]});
            var Q313;
            Q313=makeQuery(id+"F10.imprint","IMPRINT",FACE,{"disambiguationData":[TD([[makeQuery(id+"F10.imprint","IMPRINT",EDGE,{"derivedFrom":sQuery(id+"F10.wireOp",EDGE,"E41.12.9.0")}),1.0]])]});
            var Q314;
            Q314=makeQuery(id+"F10.imprint","IMPRINT",FACE,{"disambiguationData":[TD([[makeQuery(id+"F10.imprint","IMPRINT",EDGE,{"derivedFrom":sQuery(id+"F10.wireOp",EDGE,"E41.21.2.0")}),1.0]])]});
            var Q315;
            Q315=makeQuery(id+"F10.imprint","IMPRINT",FACE,{"disambiguationData":[TD([[makeQuery(id+"F10.imprint","IMPRINT",EDGE,{"derivedFrom":sQuery(id+"F10.wireOp",EDGE,"E41.20.1.0")}),1.0]])]});
            var Q316;
            Q316=makeQuery(id+"F10.imprint","IMPRINT",FACE,{"disambiguationData":[TD([[makeQuery(id+"F10.imprint","IMPRINT",EDGE,{"derivedFrom":sQuery(id+"F10.wireOp",EDGE,"E41.17.14.0")}),1.0]])]});
            var Q317;
            Q317=makeQuery(id+"F10.imprint","IMPRINT",FACE,{"disambiguationData":[TD([[makeQuery(id+"F10.imprint","IMPRINT",EDGE,{"derivedFrom":sQuery(id+"F10.wireOp",EDGE,"E41.22.9.0")}),1.0]])]});
            var Q318;
            Q318=makeQuery(id+"F10.imprint","IMPRINT",FACE,{"disambiguationData":[TD([[makeQuery(id+"F10.imprint","IMPRINT",EDGE,{"derivedFrom":sQuery(id+"F10.wireOp",EDGE,"E41.2.0.0")}),1.0]])]});
            var Q319;
            Q319=makeQuery(id+"F10.imprint","IMPRINT",FACE,{"disambiguationData":[TD([[makeQuery(id+"F10.imprint","IMPRINT",EDGE,{"derivedFrom":sQuery(id+"F10.wireOp",EDGE,"E41.7.5.0")}),1.0]])]});
            var Q320;
            Q320=makeQuery(id+"F10.imprint","IMPRINT",FACE,{"disambiguationData":[TD([[makeQuery(id+"F10.imprint","IMPRINT",EDGE,{"derivedFrom":sQuery(id+"F10.wireOp",EDGE,"E41.12.10.0")}),1.0]])]});
            var Q321;
            Q321=makeQuery(id+"F10.imprint","IMPRINT",FACE,{"disambiguationData":[TD([[makeQuery(id+"F10.imprint","IMPRINT",EDGE,{"derivedFrom":sQuery(id+"F10.wireOp",EDGE,"E41.11.9.0")}),1.0]])]});
            var Q322;
            Q322=makeQuery(id+"F10.imprint","IMPRINT",FACE,{"disambiguationData":[TD([[makeQuery(id+"F10.imprint","IMPRINT",EDGE,{"derivedFrom":sQuery(id+"F10.wireOp",EDGE,"E41.2.6.0")}),1.0]])]});
            var Q323;
            Q323=makeQuery(id+"F10.imprint","IMPRINT",FACE,{"disambiguationData":[TD([[makeQuery(id+"F10.imprint","IMPRINT",EDGE,{"derivedFrom":sQuery(id+"F10.wireOp",EDGE,"E41.1.5.0")}),1.0]])]});
            var Q324;
            Q324=makeQuery(id+"F10.imprint","IMPRINT",FACE,{"disambiguationData":[TD([[makeQuery(id+"F10.imprint","IMPRINT",EDGE,{"derivedFrom":sQuery(id+"F10.wireOp",EDGE,"E41.7.11.0")}),1.0]])]});
            var Q325;
            Q325=makeQuery(id+"F10.imprint","IMPRINT",FACE,{"disambiguationData":[TD([[makeQuery(id+"F10.imprint","IMPRINT",EDGE,{"derivedFrom":sQuery(id+"F10.wireOp",EDGE,"E41.16.14.0")}),1.0]])]});
            var Q326;
            Q326=makeQuery(id+"F10.imprint","IMPRINT",FACE,{"disambiguationData":[TD([[makeQuery(id+"F10.imprint","IMPRINT",EDGE,{"derivedFrom":sQuery(id+"F10.wireOp",EDGE,"E41.6.10.0")}),1.0]])]});
            var Q327;
            Q327=makeQuery(id+"F10.imprint","IMPRINT",FACE,{"disambiguationData":[TD([[makeQuery(id+"F10.imprint","IMPRINT",EDGE,{"derivedFrom":sQuery(id+"F10.wireOp",EDGE,"E41.5.9.0")}),1.0]])]});
            var Q328;
            Q328=makeQuery(id+"F10.imprint","IMPRINT",FACE,{"disambiguationData":[TD([[makeQuery(id+"F10.imprint","IMPRINT",EDGE,{"derivedFrom":sQuery(id+"F10.wireOp",EDGE,"E41.2.2.0")}),1.0]])]});
            var Q329;
            Q329=makeQuery(id+"F10.imprint","IMPRINT",FACE,{"disambiguationData":[TD([[makeQuery(id+"F10.imprint","IMPRINT",EDGE,{"derivedFrom":sQuery(id+"F10.wireOp",EDGE,"E41.1.1.0")}),1.0]])]});
            var Q330;
            Q330=makeQuery(id+"F10.imprint","IMPRINT",FACE,{"disambiguationData":[TD([[makeQuery(id+"F10.imprint","IMPRINT",EDGE,{"derivedFrom":sQuery(id+"F10.wireOp",EDGE,"E41.6.6.0")}),1.0]])]});
            var Q331;
            Q331=makeQuery(id+"F10.imprint","IMPRINT",FACE,{"disambiguationData":[TD([[makeQuery(id+"F10.imprint","IMPRINT",EDGE,{"derivedFrom":sQuery(id+"F10.wireOp",EDGE,"E41.5.5.0")}),1.0]])]});
            var Q332;
            Q332=makeQuery(id+"F10.imprint","IMPRINT",FACE,{"disambiguationData":[TD([[makeQuery(id+"F10.imprint","IMPRINT",EDGE,{"derivedFrom":sQuery(id+"F10.wireOp",EDGE,"E41.11.11.0")}),1.0]])]});
            var Q333;
            Q333=makeQuery(id+"F10.imprint","IMPRINT",FACE,{"disambiguationData":[TD([[makeQuery(id+"F10.imprint","IMPRINT",EDGE,{"derivedFrom":sQuery(id+"F10.wireOp",EDGE,"E41.10.10.0")}),1.0]])]});
            var Q334;
            Q334=makeQuery(id+"F10.imprint","IMPRINT",FACE,{"disambiguationData":[TD([[makeQuery(id+"F10.imprint","IMPRINT",EDGE,{"derivedFrom":sQuery(id+"F10.wireOp",EDGE,"E41.17.1.0")}),1.0]])]});
            var Q335;
            Q335=makeQuery(id+"F10.imprint","IMPRINT",FACE,{"disambiguationData":[TD([[makeQuery(id+"F10.imprint","IMPRINT",EDGE,{"derivedFrom":sQuery(id+"F10.wireOp",EDGE,"E41.16.0.0")}),1.0]])]});
            var Q336;
            Q336=makeQuery(id+"F10.imprint","IMPRINT",FACE,{"disambiguationData":[TD([[makeQuery(id+"F10.imprint","IMPRINT",EDGE,{"derivedFrom":sQuery(id+"F10.wireOp",EDGE,"E41.21.5.0")}),1.0]])]});
            var Q337;
            Q337=makeQuery(id+"F10.imprint","IMPRINT",FACE,{"disambiguationData":[TD([[makeQuery(id+"F10.imprint","IMPRINT",EDGE,{"derivedFrom":sQuery(id+"F10.wireOp",EDGE,"E41.22.6.0")}),1.0]])]});
            var Q338;
            Q338=makeQuery(id+"F10.imprint","IMPRINT",FACE,{"disambiguationData":[TD([[makeQuery(id+"F10.imprint","IMPRINT",EDGE,{"derivedFrom":sQuery(id+"F10.wireOp",EDGE,"E41.12.0.0")}),1.0]])]});
            var Q339;
            Q339=makeQuery(id+"F10.imprint","IMPRINT",FACE,{"disambiguationData":[TD([[makeQuery(id+"F10.imprint","IMPRINT",EDGE,{"derivedFrom":sQuery(id+"F10.wireOp",EDGE,"E41.10.14.0")}),1.0]])]});
            var Q340;
            Q340=makeQuery(id+"F10.imprint","IMPRINT",FACE,{"disambiguationData":[TD([[makeQuery(id+"F10.imprint","IMPRINT",EDGE,{"derivedFrom":sQuery(id+"F10.wireOp",EDGE,"E41.1.2.0")}),1.0]])]});
            var Q341;
            Q341=makeQuery(id+"F10.imprint","IMPRINT",FACE,{"disambiguationData":[TD([[makeQuery(id+"F10.imprint","IMPRINT",EDGE,{"derivedFrom":sQuery(id+"F10.wireOp",EDGE,"E41.17.5.0")}),1.0]])]});
            var Q342;
            Q342=makeQuery(id+"F10.imprint","IMPRINT",FACE,{"disambiguationData":[TD([[makeQuery(id+"F10.imprint","IMPRINT",EDGE,{"derivedFrom":sQuery(id+"F10.wireOp",EDGE,"E41.21.9.0")}),1.0]])]});
            var Q343;
            Q343=makeQuery(id+"F10.imprint","IMPRINT",FACE,{"disambiguationData":[TD([[makeQuery(id+"F10.imprint","IMPRINT",EDGE,{"derivedFrom":sQuery(id+"F10.wireOp",EDGE,"E41.22.10.0")}),1.0]])]});
            var Q344;
            Q344=makeQuery(id+"F10.imprint","IMPRINT",FACE,{"disambiguationData":[TD([[makeQuery(id+"F10.imprint","IMPRINT",EDGE,{"derivedFrom":sQuery(id+"F10.wireOp",EDGE,"E41.5.6.0")}),1.0]])]});
            var Q345;
            Q345=makeQuery(id+"F10.imprint","IMPRINT",FACE,{"disambiguationData":[TD([[makeQuery(id+"F10.imprint","IMPRINT",EDGE,{"derivedFrom":sQuery(id+"F10.wireOp",EDGE,"E41.10.11.0")}),1.0]])]});
            var Q346;
            Q346=makeQuery(id+"F10.imprint","IMPRINT",FACE,{"disambiguationData":[TD([[makeQuery(id+"F10.imprint","IMPRINT",EDGE,{"derivedFrom":sQuery(id+"F10.wireOp",EDGE,"E41.17.2.0")}),1.0]])]});
            var Q347;
            Q347=makeQuery(id+"F10.imprint","IMPRINT",FACE,{"disambiguationData":[TD([[makeQuery(id+"F10.imprint","IMPRINT",EDGE,{"derivedFrom":sQuery(id+"F10.wireOp",EDGE,"E41.16.1.0")}),1.0]])]});
            var Q348;
            Q348=makeQuery(id+"F10.imprint","IMPRINT",FACE,{"disambiguationData":[TD([[makeQuery(id+"F10.imprint","IMPRINT",EDGE,{"derivedFrom":sQuery(id+"F10.wireOp",EDGE,"E41.15.0.0")}),1.0]])]});
            var Q349;
            Q349=makeQuery(id+"F10.imprint","IMPRINT",FACE,{"disambiguationData":[TD([[makeQuery(id+"F10.imprint","IMPRINT",EDGE,{"derivedFrom":sQuery(id+"F10.wireOp",EDGE,"E41.21.6.0")}),1.0]])]});
            var Q350;
            Q350=makeQuery(id+"F10.imprint","IMPRINT",FACE,{"disambiguationData":[TD([[makeQuery(id+"F10.imprint","IMPRINT",EDGE,{"derivedFrom":sQuery(id+"F10.wireOp",EDGE,"E41.20.5.0")}),1.0]])]});
            var Q351;
            Q351=makeQuery(id+"F10.imprint","IMPRINT",FACE,{"disambiguationData":[TD([[makeQuery(id+"F10.imprint","IMPRINT",EDGE,{"derivedFrom":sQuery(id+"F10.wireOp",EDGE,"E41.1.6.0")}),1.0]])]});
            var Q352;
            Q352=makeQuery(id+"F10.imprint","IMPRINT",FACE,{"disambiguationData":[TD([[makeQuery(id+"F10.imprint","IMPRINT",EDGE,{"derivedFrom":sQuery(id+"F10.wireOp",EDGE,"E41.6.11.0")}),1.0]])]});
            var Q353;
            Q353=makeQuery(id+"F10.imprint","IMPRINT",FACE,{"disambiguationData":[TD([[makeQuery(id+"F10.imprint","IMPRINT",EDGE,{"derivedFrom":sQuery(id+"F10.wireOp",EDGE,"E41.5.10.0")}),1.0]])]});
            var Q354;
            Q354=makeQuery(id+"F10.imprint","IMPRINT",FACE,{"disambiguationData":[TD([[makeQuery(id+"F10.imprint","IMPRINT",EDGE,{"derivedFrom":sQuery(id+"F10.wireOp",EDGE,"E41.12.1.0")}),1.0]])]});
            var Q355;
            Q355=makeQuery(id+"F10.imprint","IMPRINT",FACE,{"disambiguationData":[TD([[makeQuery(id+"F10.imprint","IMPRINT",EDGE,{"derivedFrom":sQuery(id+"F10.wireOp",EDGE,"E41.11.0.0")}),1.0]])]});
            var Q356;
            Q356=makeQuery(id+"F10.imprint","IMPRINT",FACE,{"disambiguationData":[TD([[makeQuery(id+"F10.imprint","IMPRINT",EDGE,{"derivedFrom":sQuery(id+"F10.wireOp",EDGE,"E41.17.6.0")}),1.0]])]});
            var Q357;
            Q357=makeQuery(id+"F10.imprint","IMPRINT",FACE,{"disambiguationData":[TD([[makeQuery(id+"F10.imprint","IMPRINT",EDGE,{"derivedFrom":sQuery(id+"F10.wireOp",EDGE,"E41.16.5.0")}),1.0]])]});
            var Q358;
            Q358=makeQuery(id+"F10.imprint","IMPRINT",FACE,{"disambiguationData":[TD([[makeQuery(id+"F10.imprint","IMPRINT",EDGE,{"derivedFrom":sQuery(id+"F10.wireOp",EDGE,"E41.21.10.0")}),1.0]])]});
            var Q359;
            Q359=makeQuery(id+"F10.imprint","IMPRINT",FACE,{"disambiguationData":[TD([[makeQuery(id+"F10.imprint","IMPRINT",EDGE,{"derivedFrom":sQuery(id+"F10.wireOp",EDGE,"E41.20.9.0")}),1.0]])]});
            var Q360;
            Q360=makeQuery(id+"F10.imprint","IMPRINT",FACE,{"disambiguationData":[TD([[makeQuery(id+"F10.imprint","IMPRINT",EDGE,{"derivedFrom":sQuery(id+"F10.wireOp",EDGE,"E41.22.11.0")}),1.0]])]});
            var Q361;
            Q361=makeQuery(id+"F10.imprint","IMPRINT",FACE,{"disambiguationData":[TD([[makeQuery(id+"F10.imprint","IMPRINT",EDGE,{"derivedFrom":sQuery(id+"F10.wireOp",EDGE,"E41.5.11.0")}),1.0]])]});
            var Q362;
            Q362=makeQuery(id+"F10.imprint","IMPRINT",FACE,{"disambiguationData":[TD([[makeQuery(id+"F10.imprint","IMPRINT",EDGE,{"derivedFrom":sQuery(id+"F10.wireOp",EDGE,"E41.11.1.0")}),1.0]])]});
            var Q363;
            Q363=makeQuery(id+"F10.imprint","IMPRINT",FACE,{"disambiguationData":[TD([[makeQuery(id+"F10.imprint","IMPRINT",EDGE,{"derivedFrom":sQuery(id+"F10.wireOp",EDGE,"E41.10.0.0")}),1.0]])]});
            var Q364;
            Q364=makeQuery(id+"F10.imprint","IMPRINT",FACE,{"disambiguationData":[TD([[makeQuery(id+"F10.imprint","IMPRINT",EDGE,{"derivedFrom":sQuery(id+"F10.wireOp",EDGE,"E41.15.5.0")}),1.0]])]});
            var Q365;
            Q365=makeQuery(id+"F10.imprint","IMPRINT",FACE,{"disambiguationData":[TD([[makeQuery(id+"F10.imprint","IMPRINT",EDGE,{"derivedFrom":sQuery(id+"F10.wireOp",EDGE,"E41.12.2.0")}),1.0]])]});
            var Q366;
            Q366=makeQuery(id+"F10.imprint","IMPRINT",FACE,{"disambiguationData":[TD([[makeQuery(id+"F10.imprint","IMPRINT",EDGE,{"derivedFrom":sQuery(id+"F10.wireOp",EDGE,"E41.16.6.0")}),1.0]])]});
            var Q367;
            Q367=makeQuery(id+"F10.imprint","IMPRINT",FACE,{"disambiguationData":[TD([[makeQuery(id+"F10.imprint","IMPRINT",EDGE,{"derivedFrom":sQuery(id+"F10.wireOp",EDGE,"E41.21.11.0")}),1.0]])]});
            var Q368;
            Q368=makeQuery(id+"F10.imprint","IMPRINT",FACE,{"disambiguationData":[TD([[makeQuery(id+"F10.imprint","IMPRINT",EDGE,{"derivedFrom":sQuery(id+"F10.wireOp",EDGE,"E41.20.10.0")}),1.0]])]});
            var Q369;
            Q369=makeQuery(id+"F10.imprint","IMPRINT",FACE,{"disambiguationData":[TD([[makeQuery(id+"F10.imprint","IMPRINT",EDGE,{"derivedFrom":sQuery(id+"F10.wireOp",EDGE,"E41.2.9.0")}),1.0]])]});
            var Q370;
            Q370=makeQuery(id+"F10.imprint","IMPRINT",FACE,{"disambiguationData":[TD([[makeQuery(id+"F10.imprint","IMPRINT",EDGE,{"derivedFrom":sQuery(id+"F10.wireOp",EDGE,"E41.11.2.0")}),1.0]])]});
            var Q371;
            Q371=makeQuery(id+"F10.imprint","IMPRINT",FACE,{"disambiguationData":[TD([[makeQuery(id+"F10.imprint","IMPRINT",EDGE,{"derivedFrom":sQuery(id+"F10.wireOp",EDGE,"E41.10.1.0")}),1.0]])]});
            var Q372;
            Q372=makeQuery(id+"F10.imprint","IMPRINT",FACE,{"disambiguationData":[TD([[makeQuery(id+"F10.imprint","IMPRINT",EDGE,{"derivedFrom":sQuery(id+"F10.wireOp",EDGE,"E41.7.14.0")}),1.0]])]});
            var Q373;
            Q373=makeQuery(id+"F10.imprint","IMPRINT",FACE,{"disambiguationData":[TD([[makeQuery(id+"F10.imprint","IMPRINT",EDGE,{"derivedFrom":sQuery(id+"F10.wireOp",EDGE,"E41.15.6.0")}),1.0]])]});
            var Q374;
            Q374=makeQuery(id+"F10.imprint","IMPRINT",FACE,{"disambiguationData":[TD([[makeQuery(id+"F10.imprint","IMPRINT",EDGE,{"derivedFrom":sQuery(id+"F10.wireOp",EDGE,"E41.20.11.0")}),1.0]])]});
            extrude(context, id + "F11", {"entities" : qUnion([Q0, Q1, Q2, Q3, Q4, Q5, Q6, Q7, Q8, Q9, Q10, Q11, Q12, Q13, Q14, Q15, Q16, Q17, Q18, Q19, Q20, Q21, Q22, Q23, Q24, Q25, Q26, Q27, Q28, Q29, Q30, Q31, Q32, Q33, Q34, Q35, Q36, Q37, Q38, Q39, Q40, Q41, Q42, Q43, Q44, Q45, Q46, Q47, Q48, Q49, Q50, Q51, Q52, Q53, Q54, Q55, Q56, Q57, Q58, Q59, Q60, Q61, Q62, Q63, Q64, Q65, Q66, Q67, Q68, Q69, Q70, Q71, Q72, Q73, Q74, Q75, Q76, Q77, Q78, Q79, Q80, Q81, Q82, Q83, Q84, Q85, Q86, Q87, Q88, Q89, Q90, Q91, Q92, Q93, Q94, Q95, Q96, Q97, Q98, Q99, Q100, Q101, Q102, Q103, Q104, Q105, Q106, Q107, Q108, Q109, Q110, Q111, Q112, Q113, Q114, Q115, Q116, Q117, Q118, Q119, Q120, Q121, Q122, Q123, Q124, Q125, Q126, Q127, Q128, Q129, Q130, Q131, Q132, Q133, Q134, Q135, Q136, Q137, Q138, Q139, Q140, Q141, Q142, Q143, Q144, Q145, Q146, Q147, Q148, Q149, Q150, Q151, Q152, Q153, Q154, Q155, Q156, Q157, Q158, Q159, Q160, Q161, Q162, Q163, Q164, Q165, Q166, Q167, Q168, Q169, Q170, Q171, Q172, Q173, Q174, Q175, Q176, Q177, Q178, Q179, Q180, Q181, Q182, Q183, Q184, Q185, Q186, Q187, Q188, Q189, Q190, Q191, Q192, Q193, Q194, Q195, Q196, Q197, Q198, Q199, Q200, Q201, Q202, Q203, Q204, Q205, Q206, Q207, Q208, Q209, Q210, Q211, Q212, Q213, Q214, Q215, Q216, Q217, Q218, Q219, Q220, Q221, Q222, Q223, Q224, Q225, Q226, Q227, Q228, Q229, Q230, Q231, Q232, Q233, Q234, Q235, Q236, Q237, Q238, Q239, Q240, Q241, Q242, Q243, Q244, Q245, Q246, Q247, Q248, Q249, Q250, Q251, Q252, Q253, Q254, Q255, Q256, Q257, Q258, Q259, Q260, Q261, Q262, Q263, Q264, Q265, Q266, Q267, Q268, Q269, Q270, Q271, Q272, Q273, Q274, Q275, Q276, Q277, Q278, Q279, Q280, Q281, Q282, Q283, Q284, Q285, Q286, Q287, Q288, Q289, Q290, Q291, Q292, Q293, Q294, Q295, Q296, Q297, Q298, Q299, Q300, Q301, Q302, Q303, Q304, Q305, Q306, Q307, Q308, Q309, Q310, Q311, Q312, Q313, Q314, Q315, Q316, Q317, Q318, Q319, Q320, Q321, Q322, Q323, Q324, Q325, Q326, Q327, Q328, Q329, Q330, Q331, Q332, Q333, Q334, Q335, Q336, Q337, Q338, Q339, Q340, Q341, Q342, Q343, Q344, Q345, Q346, Q347, Q348, Q349, Q350, Q351, Q352, Q353, Q354, Q355, Q356, Q357, Q358, Q359, Q360, Q361, Q362, Q363, Q364, Q365, Q366, Q367, Q368, Q369, Q370, Q371, Q372, Q373, Q374]), "operationType" : NewBodyOperationType.REMOVE, "oppositeDirection" : true, "depth" : 25.4 * mm});
        }
    });
